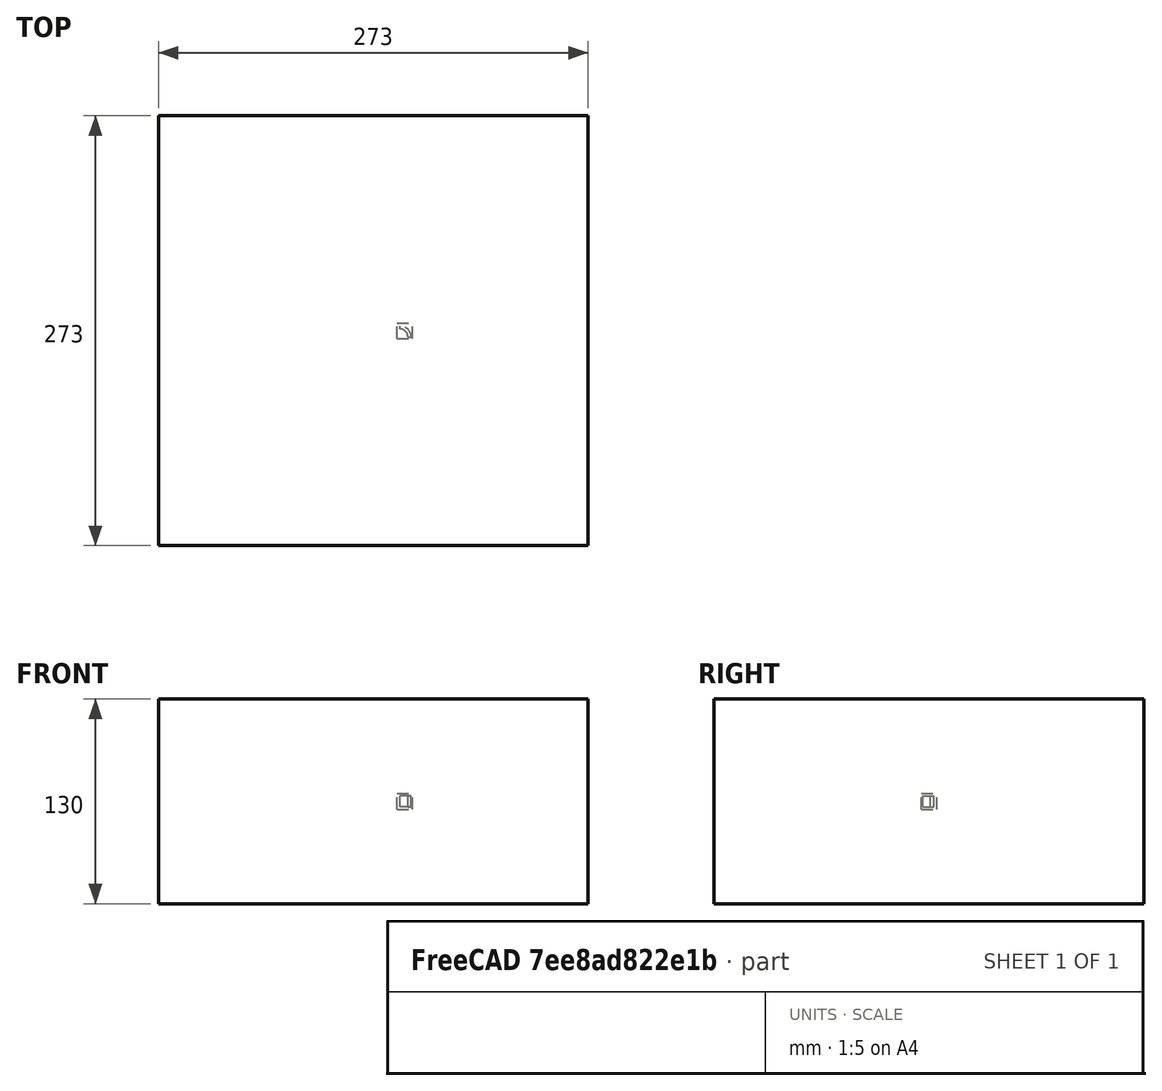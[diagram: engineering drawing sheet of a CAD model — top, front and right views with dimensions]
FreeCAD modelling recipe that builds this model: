
FCSTD DOCUMENT  (FreeCAD 0.21R33694 (Git))
Label: polarArray-of-Part
License: All rights reserved
LicenseURL: http://en.wikipedia.org/wiki/All_rights_reserved
objects: App::DocumentObjectGroupPython×1251, Part::FeaturePython×4, App::Part×4
note: 3 computed .brp shape members not serialized (recipe doc carries the construction recipe); baked Part::Feature solids carry a one-line shape summary decoded from their .brp

FEATURE [App::DocumentObjectGroupPython] HALFPI  # scripted group (container) (typed FeaturePython)
  name = HALFPI
  value = pi/2.
FEATURE [App::DocumentObjectGroupPython] PI  # scripted group (container) (typed FeaturePython)
  name = PI
  value = 1.*pi
FEATURE [App::DocumentObjectGroupPython] TWOPI  # scripted group (container) (typed FeaturePython)
  name = TWOPI
  value = 2.*pi
FEATURE [App::DocumentObjectGroupPython] Constants  # scripted group (container) (typed FeaturePython)
  Group = -> [HALFPI,PI,TWOPI]
FEATURE [App::DocumentObjectGroupPython] Variables  # scripted group (container) (typed FeaturePython)
FEATURE [App::DocumentObjectGroupPython] Quantities  # scripted group (container) (typed FeaturePython)
FEATURE [App::DocumentObjectGroupPython] Isotopes  # scripted group (container) (typed FeaturePython)
FEATURE [App::DocumentObjectGroupPython] Elements  # scripted group (container) (typed FeaturePython)
FEATURE [App::DocumentObjectGroupPython] Matrix  # scripted group (container) (typed FeaturePython)
FEATURE [App::DocumentObjectGroupPython] Surfaces  # scripted group (container) (typed FeaturePython)
FEATURE [App::DocumentObjectGroupPython] Opticals  # scripted group (container) (typed FeaturePython)
  Group = -> [Matrix,Surfaces]
FEATURE [App::DocumentObjectGroupPython] G4Isotopes  # scripted group (container) (typed FeaturePython)
FEATURE [App::DocumentObjectGroupPython] H_element  # scripted group (container) (typed FeaturePython)
  Z = 1
  atom_value = 1.008
  formula = H
  name = H_element
FEATURE [App::DocumentObjectGroupPython] He_element  # scripted group (container) (typed FeaturePython)
  Z = 2
  atom_value = 4.0026
  formula = He
  name = He_element
FEATURE [App::DocumentObjectGroupPython] Li_element  # scripted group (container) (typed FeaturePython)
  Z = 3
  atom_value = 6.94
  formula = Li
  name = Li_element
FEATURE [App::DocumentObjectGroupPython] Be_element  # scripted group (container) (typed FeaturePython)
  Z = 4
  atom_value = 9.01218
  formula = Be
  name = Be_element
FEATURE [App::DocumentObjectGroupPython] B_element  # scripted group (container) (typed FeaturePython)
  Z = 5
  atom_value = 10.81
  formula = B
  name = B_element
FEATURE [App::DocumentObjectGroupPython] C_element  # scripted group (container) (typed FeaturePython)
  Z = 6
  atom_value = 12.011
  formula = C
  name = C_element
FEATURE [App::DocumentObjectGroupPython] N_element  # scripted group (container) (typed FeaturePython)
  Z = 7
  atom_value = 14.007
  formula = N
  name = N_element
FEATURE [App::DocumentObjectGroupPython] O_element  # scripted group (container) (typed FeaturePython)
  Z = 8
  atom_value = 15.999
  formula = O
  name = O_element
FEATURE [App::DocumentObjectGroupPython] F_element  # scripted group (container) (typed FeaturePython)
  Z = 9
  atom_value = 18.9984
  formula = F
  name = F_element
FEATURE [App::DocumentObjectGroupPython] Ne_element  # scripted group (container) (typed FeaturePython)
  Z = 10
  atom_value = 20.1797
  formula = Ne
  name = Ne_element
FEATURE [App::DocumentObjectGroupPython] Na_element  # scripted group (container) (typed FeaturePython)
  Z = 11
  atom_value = 22.9898
  formula = Na
  name = Na_element
FEATURE [App::DocumentObjectGroupPython] Mg_element  # scripted group (container) (typed FeaturePython)
  Z = 12
  atom_value = 24.305
  formula = Mg
  name = Mg_element
FEATURE [App::DocumentObjectGroupPython] Al_element  # scripted group (container) (typed FeaturePython)
  Z = 13
  atom_value = 26.9815
  formula = Al
  name = Al_element
FEATURE [App::DocumentObjectGroupPython] Si_element  # scripted group (container) (typed FeaturePython)
  Z = 14
  atom_value = 28.085
  formula = Si
  name = Si_element
FEATURE [App::DocumentObjectGroupPython] P_element  # scripted group (container) (typed FeaturePython)
  Z = 15
  atom_value = 30.9738
  formula = P
  name = P_element
FEATURE [App::DocumentObjectGroupPython] S_element  # scripted group (container) (typed FeaturePython)
  Z = 16
  atom_value = 32.06
  formula = S
  name = S_element
FEATURE [App::DocumentObjectGroupPython] Cl_element  # scripted group (container) (typed FeaturePython)
  Z = 17
  atom_value = 35.45
  formula = Cl
  name = Cl_element
FEATURE [App::DocumentObjectGroupPython] Ar_element  # scripted group (container) (typed FeaturePython)
  Z = 18
  atom_value = 39.95
  formula = Ar
  name = Ar_element
FEATURE [App::DocumentObjectGroupPython] K_element  # scripted group (container) (typed FeaturePython)
  Z = 19
  atom_value = 39.0983
  formula = K
  name = K_element
FEATURE [App::DocumentObjectGroupPython] Ca_element  # scripted group (container) (typed FeaturePython)
  Z = 20
  atom_value = 40.078
  formula = Ca
  name = Ca_element
FEATURE [App::DocumentObjectGroupPython] Sc_element  # scripted group (container) (typed FeaturePython)
  Z = 21
  atom_value = 44.9559
  formula = Sc
  name = Sc_element
FEATURE [App::DocumentObjectGroupPython] Ti_element  # scripted group (container) (typed FeaturePython)
  Z = 22
  atom_value = 47.867
  formula = Ti
  name = Ti_element
FEATURE [App::DocumentObjectGroupPython] V_element  # scripted group (container) (typed FeaturePython)
  Z = 23
  atom_value = 50.9415
  formula = V
  name = V_element
FEATURE [App::DocumentObjectGroupPython] Cr_element  # scripted group (container) (typed FeaturePython)
  Z = 24
  atom_value = 51.9961
  formula = Cr
  name = Cr_element
FEATURE [App::DocumentObjectGroupPython] Mn_element  # scripted group (container) (typed FeaturePython)
  Z = 25
  atom_value = 54.938
  formula = Mn
  name = Mn_element
FEATURE [App::DocumentObjectGroupPython] Fe_element  # scripted group (container) (typed FeaturePython)
  Z = 26
  atom_value = 55.845
  formula = Fe
  name = Fe_element
FEATURE [App::DocumentObjectGroupPython] Co_element  # scripted group (container) (typed FeaturePython)
  Z = 27
  atom_value = 58.9332
  formula = Co
  name = Co_element
FEATURE [App::DocumentObjectGroupPython] Ni_element  # scripted group (container) (typed FeaturePython)
  Z = 28
  atom_value = 58.6934
  formula = Ni
  name = Ni_element
FEATURE [App::DocumentObjectGroupPython] Cu_element  # scripted group (container) (typed FeaturePython)
  Z = 29
  atom_value = 63.546
  formula = Cu
  name = Cu_element
FEATURE [App::DocumentObjectGroupPython] Zn_element  # scripted group (container) (typed FeaturePython)
  Z = 30
  atom_value = 65.38
  formula = Zn
  name = Zn_element
FEATURE [App::DocumentObjectGroupPython] Ga_element  # scripted group (container) (typed FeaturePython)
  Z = 31
  atom_value = 69.723
  formula = Ga
  name = Ga_element
FEATURE [App::DocumentObjectGroupPython] Ge_element  # scripted group (container) (typed FeaturePython)
  Z = 32
  atom_value = 72.63
  formula = Ge
  name = Ge_element
FEATURE [App::DocumentObjectGroupPython] As_element  # scripted group (container) (typed FeaturePython)
  Z = 33
  atom_value = 74.9216
  formula = As
  name = As_element
FEATURE [App::DocumentObjectGroupPython] Se_element  # scripted group (container) (typed FeaturePython)
  Z = 34
  atom_value = 78.971
  formula = Se
  name = Se_element
FEATURE [App::DocumentObjectGroupPython] Br_element  # scripted group (container) (typed FeaturePython)
  Z = 35
  atom_value = 79.904
  formula = Br
  name = Br_element
FEATURE [App::DocumentObjectGroupPython] Kr_element  # scripted group (container) (typed FeaturePython)
  Z = 36
  atom_value = 83.798
  formula = Kr
  name = Kr_element
FEATURE [App::DocumentObjectGroupPython] Rb_element  # scripted group (container) (typed FeaturePython)
  Z = 37
  atom_value = 85.4678
  formula = Rb
  name = Rb_element
FEATURE [App::DocumentObjectGroupPython] Sr_element  # scripted group (container) (typed FeaturePython)
  Z = 38
  atom_value = 87.62
  formula = Sr
  name = Sr_element
FEATURE [App::DocumentObjectGroupPython] Y_element  # scripted group (container) (typed FeaturePython)
  Z = 39
  atom_value = 88.9058
  formula = Y
  name = Y_element
FEATURE [App::DocumentObjectGroupPython] Zr_element  # scripted group (container) (typed FeaturePython)
  Z = 40
  atom_value = 91.224
  formula = Zr
  name = Zr_element
FEATURE [App::DocumentObjectGroupPython] Nb_element  # scripted group (container) (typed FeaturePython)
  Z = 41
  atom_value = 92.9064
  formula = Nb
  name = Nb_element
FEATURE [App::DocumentObjectGroupPython] Mo_element  # scripted group (container) (typed FeaturePython)
  Z = 42
  atom_value = 95.95
  formula = Mo
  name = Mo_element
FEATURE [App::DocumentObjectGroupPython] Tc_element  # scripted group (container) (typed FeaturePython)
  Z = 43
  atom_value = 97
  formula = Tc
  name = Tc_element
FEATURE [App::DocumentObjectGroupPython] Ru_element  # scripted group (container) (typed FeaturePython)
  Z = 44
  atom_value = 101.07
  formula = Ru
  name = Ru_element
FEATURE [App::DocumentObjectGroupPython] Rh_element  # scripted group (container) (typed FeaturePython)
  Z = 45
  atom_value = 102.905
  formula = Rh
  name = Rh_element
FEATURE [App::DocumentObjectGroupPython] Pd_element  # scripted group (container) (typed FeaturePython)
  Z = 46
  atom_value = 106.42
  formula = Pd
  name = Pd_element
FEATURE [App::DocumentObjectGroupPython] Ag_element  # scripted group (container) (typed FeaturePython)
  Z = 47
  atom_value = 107.868
  formula = Ag
  name = Ag_element
FEATURE [App::DocumentObjectGroupPython] Cd_element  # scripted group (container) (typed FeaturePython)
  Z = 48
  atom_value = 112.414
  formula = Cd
  name = Cd_element
FEATURE [App::DocumentObjectGroupPython] In_element  # scripted group (container) (typed FeaturePython)
  Z = 49
  atom_value = 114.818
  formula = In
  name = In_element
FEATURE [App::DocumentObjectGroupPython] Sn_element  # scripted group (container) (typed FeaturePython)
  Z = 50
  atom_value = 118.71
  formula = Sn
  name = Sn_element
FEATURE [App::DocumentObjectGroupPython] Sb_element  # scripted group (container) (typed FeaturePython)
  Z = 51
  atom_value = 121.76
  formula = Sb
  name = Sb_element
FEATURE [App::DocumentObjectGroupPython] Te_element  # scripted group (container) (typed FeaturePython)
  Z = 52
  atom_value = 127.6
  formula = Te
  name = Te_element
FEATURE [App::DocumentObjectGroupPython] I_element  # scripted group (container) (typed FeaturePython)
  Z = 53
  atom_value = 126.904
  formula = I
  name = I_element
FEATURE [App::DocumentObjectGroupPython] Xe_element  # scripted group (container) (typed FeaturePython)
  Z = 54
  atom_value = 131.293
  formula = Xe
  name = Xe_element
FEATURE [App::DocumentObjectGroupPython] Cs_element  # scripted group (container) (typed FeaturePython)
  Z = 55
  atom_value = 132.905
  formula = Cs
  name = Cs_element
FEATURE [App::DocumentObjectGroupPython] Ba_element  # scripted group (container) (typed FeaturePython)
  Z = 56
  atom_value = 137.327
  formula = Ba
  name = Ba_element
FEATURE [App::DocumentObjectGroupPython] La_element  # scripted group (container) (typed FeaturePython)
  Z = 57
  atom_value = 138.905
  formula = La
  name = La_element
FEATURE [App::DocumentObjectGroupPython] Ce_element  # scripted group (container) (typed FeaturePython)
  Z = 58
  atom_value = 140.116
  formula = Ce
  name = Ce_element
FEATURE [App::DocumentObjectGroupPython] Pr_element  # scripted group (container) (typed FeaturePython)
  Z = 59
  atom_value = 140.908
  formula = Pr
  name = Pr_element
FEATURE [App::DocumentObjectGroupPython] Nd_element  # scripted group (container) (typed FeaturePython)
  Z = 60
  atom_value = 144.242
  formula = Nd
  name = Nd_element
FEATURE [App::DocumentObjectGroupPython] Pm_element  # scripted group (container) (typed FeaturePython)
  Z = 61
  atom_value = 145
  formula = Pm
  name = Pm_element
FEATURE [App::DocumentObjectGroupPython] Sm_element  # scripted group (container) (typed FeaturePython)
  Z = 62
  atom_value = 150.36
  formula = Sm
  name = Sm_element
FEATURE [App::DocumentObjectGroupPython] Eu_element  # scripted group (container) (typed FeaturePython)
  Z = 63
  atom_value = 151.964
  formula = Eu
  name = Eu_element
FEATURE [App::DocumentObjectGroupPython] Gd_element  # scripted group (container) (typed FeaturePython)
  Z = 64
  atom_value = 157.25
  formula = Gd
  name = Gd_element
FEATURE [App::DocumentObjectGroupPython] Tb_element  # scripted group (container) (typed FeaturePython)
  Z = 65
  atom_value = 158.925
  formula = Tb
  name = Tb_element
FEATURE [App::DocumentObjectGroupPython] Dy_element  # scripted group (container) (typed FeaturePython)
  Z = 66
  atom_value = 162.5
  formula = Dy
  name = Dy_element
FEATURE [App::DocumentObjectGroupPython] Ho_element  # scripted group (container) (typed FeaturePython)
  Z = 67
  atom_value = 164.93
  formula = Ho
  name = Ho_element
FEATURE [App::DocumentObjectGroupPython] Er_element  # scripted group (container) (typed FeaturePython)
  Z = 68
  atom_value = 167.259
  formula = Er
  name = Er_element
FEATURE [App::DocumentObjectGroupPython] Tm_element  # scripted group (container) (typed FeaturePython)
  Z = 69
  atom_value = 168.934
  formula = Tm
  name = Tm_element
FEATURE [App::DocumentObjectGroupPython] Yb_element  # scripted group (container) (typed FeaturePython)
  Z = 70
  atom_value = 173.045
  formula = Yb
  name = Yb_element
FEATURE [App::DocumentObjectGroupPython] Lu_element  # scripted group (container) (typed FeaturePython)
  Z = 71
  atom_value = 174.967
  formula = Lu
  name = Lu_element
FEATURE [App::DocumentObjectGroupPython] Hf_element  # scripted group (container) (typed FeaturePython)
  Z = 72
  atom_value = 178.49
  formula = Hf
  name = Hf_element
FEATURE [App::DocumentObjectGroupPython] Ta_element  # scripted group (container) (typed FeaturePython)
  Z = 73
  atom_value = 180.948
  formula = Ta
  name = Ta_element
FEATURE [App::DocumentObjectGroupPython] W_element  # scripted group (container) (typed FeaturePython)
  Z = 74
  atom_value = 183.84
  formula = W
  name = W_element
FEATURE [App::DocumentObjectGroupPython] Re_element  # scripted group (container) (typed FeaturePython)
  Z = 75
  atom_value = 186.207
  formula = Re
  name = Re_element
FEATURE [App::DocumentObjectGroupPython] Os_element  # scripted group (container) (typed FeaturePython)
  Z = 76
  atom_value = 190.23
  formula = Os
  name = Os_element
FEATURE [App::DocumentObjectGroupPython] Ir_element  # scripted group (container) (typed FeaturePython)
  Z = 77
  atom_value = 192.217
  formula = Ir
  name = Ir_element
FEATURE [App::DocumentObjectGroupPython] Pt_element  # scripted group (container) (typed FeaturePython)
  Z = 78
  atom_value = 195.084
  formula = Pt
  name = Pt_element
FEATURE [App::DocumentObjectGroupPython] Au_element  # scripted group (container) (typed FeaturePython)
  Z = 79
  atom_value = 196.967
  formula = Au
  name = Au_element
FEATURE [App::DocumentObjectGroupPython] Hg_element  # scripted group (container) (typed FeaturePython)
  Z = 80
  atom_value = 200.592
  formula = Hg
  name = Hg_element
FEATURE [App::DocumentObjectGroupPython] Tl_element  # scripted group (container) (typed FeaturePython)
  Z = 81
  atom_value = 204.38
  formula = Tl
  name = Tl_element
FEATURE [App::DocumentObjectGroupPython] Pb_element  # scripted group (container) (typed FeaturePython)
  Z = 82
  atom_value = 207.2
  formula = Pb
  name = Pb_element
FEATURE [App::DocumentObjectGroupPython] Bi_element  # scripted group (container) (typed FeaturePython)
  Z = 83
  atom_value = 208.98
  formula = Bi
  name = Bi_element
FEATURE [App::DocumentObjectGroupPython] Po_element  # scripted group (container) (typed FeaturePython)
  Z = 84
  atom_value = 209
  formula = Po
  name = Po_element
FEATURE [App::DocumentObjectGroupPython] At_element  # scripted group (container) (typed FeaturePython)
  Z = 85
  atom_value = 210
  formula = At
  name = At_element
FEATURE [App::DocumentObjectGroupPython] Rn_element  # scripted group (container) (typed FeaturePython)
  Z = 86
  atom_value = 222
  formula = Rn
  name = Rn_element
FEATURE [App::DocumentObjectGroupPython] Fr_element  # scripted group (container) (typed FeaturePython)
  Z = 87
  atom_value = 223
  formula = Fr
  name = Fr_element
FEATURE [App::DocumentObjectGroupPython] Ra_element  # scripted group (container) (typed FeaturePython)
  Z = 88
  atom_value = 226
  formula = Ra
  name = Ra_element
FEATURE [App::DocumentObjectGroupPython] Ac_element  # scripted group (container) (typed FeaturePython)
  Z = 89
  atom_value = 227
  formula = Ac
  name = Ac_element
FEATURE [App::DocumentObjectGroupPython] Th_element  # scripted group (container) (typed FeaturePython)
  Z = 90
  atom_value = 232.038
  formula = Th
  name = Th_element
FEATURE [App::DocumentObjectGroupPython] Pa_element  # scripted group (container) (typed FeaturePython)
  Z = 91
  atom_value = 231.036
  formula = Pa
  name = Pa_element
FEATURE [App::DocumentObjectGroupPython] U_element  # scripted group (container) (typed FeaturePython)
  Z = 92
  atom_value = 238.029
  formula = U
  name = U_element
FEATURE [App::DocumentObjectGroupPython] Np_element  # scripted group (container) (typed FeaturePython)
  Z = 93
  atom_value = 237
  formula = Np
  name = Np_element
FEATURE [App::DocumentObjectGroupPython] Pu_element  # scripted group (container) (typed FeaturePython)
  Z = 94
  atom_value = 244
  formula = Pu
  name = Pu_element
FEATURE [App::DocumentObjectGroupPython] Am_element  # scripted group (container) (typed FeaturePython)
  Z = 95
  atom_value = 243
  formula = Am
  name = Am_element
FEATURE [App::DocumentObjectGroupPython] Cm_element  # scripted group (container) (typed FeaturePython)
  Z = 96
  atom_value = 247
  formula = Cm
  name = Cm_element
FEATURE [App::DocumentObjectGroupPython] Bk_element  # scripted group (container) (typed FeaturePython)
  Z = 97
  atom_value = 247
  formula = Bk
  name = Bk_element
FEATURE [App::DocumentObjectGroupPython] Cf_element  # scripted group (container) (typed FeaturePython)
  Z = 98
  atom_value = 251
  formula = Cf
  name = Cf_element
FEATURE [App::DocumentObjectGroupPython] G4Elements  # scripted group (container) (typed FeaturePython)
  Group = -> [H_element,He_element,Li_element,Be_element,B_element,C_element,N_element,O_element,F_element,Ne_element,Na_element,Mg_element,Al_element,Si_element,P_element,S_element,Cl_element,Ar_element,K_element,Ca_element,Sc_element,Ti_element,V_element,Cr_element,Mn_element,Fe_element,Co_element,Ni_element,Cu_element,Zn_element,Ga_element,Ge_element,As_element,Se_element,Br_element,Kr_element,Rb_element,+61 more]
FEATURE [App::DocumentObjectGroupPython] H_element001  label="H_element : 0.101"  # scripted group (container) (typed FeaturePython)
  n = 0.101327
FEATURE [App::DocumentObjectGroupPython] C_element001  label="C_element : 0.775"  # scripted group (container) (typed FeaturePython)
  n = 0.7755
FEATURE [App::DocumentObjectGroupPython] N_element001  label="N_element : 0.035"  # scripted group (container) (typed FeaturePython)
  n = 0.035057
FEATURE [App::DocumentObjectGroupPython] O_element001  label="O_element : 0.052"  # scripted group (container) (typed FeaturePython)
  n = 0.0523159
FEATURE [App::DocumentObjectGroupPython] F_element001  label="F_element : 0.017"  # scripted group (container) (typed FeaturePython)
  n = 0.017422
FEATURE [App::DocumentObjectGroupPython] Ca_element001  label="Ca_element : 0.018"  # scripted group (container) (typed FeaturePython)
  n = 0.018378
FEATURE [App::DocumentObjectGroupPython] G4_A_150_TISSUE  label="G4_A-150_TISSUE"  # scripted group (container) (typed FeaturePython)
  Dunit = g/cm3
  Dvalue = 1.127
  Group = -> [H_element001,C_element001,N_element001,O_element001,F_element001,Ca_element001]
  conduct = 2
  density = 1
  expand = 3
  formula = G4_A-150_TISSUE
  name = G4_A-150_TISSUE
  specific = 4
FEATURE [App::DocumentObjectGroupPython] C_element002  label="C_element : 3"  # scripted group (container) (typed FeaturePython)
  n = 3
  ref = C_element
FEATURE [App::DocumentObjectGroupPython] H_element002  label="H_element : 6"  # scripted group (container) (typed FeaturePython)
  n = 6
  ref = H_element
FEATURE [App::DocumentObjectGroupPython] O_element002  label="O_element : 1"  # scripted group (container) (typed FeaturePython)
  n = 1
  ref = O_element
FEATURE [App::DocumentObjectGroupPython] G4_ACETONE  # scripted group (container) (typed FeaturePython)
  Dunit = g/cm3
  Dvalue = 0.7899
  Group = -> [C_element002,H_element002,O_element002]
  conduct = 2
  density = 1
  expand = 3
  formula = G4_ACETONE
  name = G4_ACETONE
  specific = 4
FEATURE [App::DocumentObjectGroupPython] C_element003  label="C_element : 2"  # scripted group (container) (typed FeaturePython)
  n = 2
  ref = C_element
FEATURE [App::DocumentObjectGroupPython] H_element003  label="H_element : 2"  # scripted group (container) (typed FeaturePython)
  n = 2
  ref = H_element
FEATURE [App::DocumentObjectGroupPython] G4_ACETYLENE  # scripted group (container) (typed FeaturePython)
  Dunit = g/cm3
  Dvalue = 0.0010967
  Group = -> [C_element003,H_element003]
  conduct = 2
  density = 1
  expand = 3
  formula = G4_ACETYLENE
  name = G4_ACETYLENE
  specific = 4
FEATURE [App::DocumentObjectGroupPython] C_element004  label="C_element : 5"  # scripted group (container) (typed FeaturePython)
  n = 5
  ref = C_element
FEATURE [App::DocumentObjectGroupPython] H_element004  label="H_element : 5"  # scripted group (container) (typed FeaturePython)
  n = 5
  ref = H_element
FEATURE [App::DocumentObjectGroupPython] N_element002  label="N_element : 5"  # scripted group (container) (typed FeaturePython)
  n = 5
  ref = N_element
FEATURE [App::DocumentObjectGroupPython] G4_ADENINE  # scripted group (container) (typed FeaturePython)
  Dunit = g/cm3
  Dvalue = 1.6
  Group = -> [C_element004,H_element004,N_element002]
  conduct = 2
  density = 1
  expand = 3
  formula = G4_ADENINE
  name = G4_ADENINE
  specific = 4
FEATURE [App::DocumentObjectGroupPython] H_element005  label="H_element : 0.114"  # scripted group (container) (typed FeaturePython)
  n = 0.114
FEATURE [App::DocumentObjectGroupPython] C_element005  label="C_element : 0.598"  # scripted group (container) (typed FeaturePython)
  n = 0.598
FEATURE [App::DocumentObjectGroupPython] N_element003  label="N_element : 0.007"  # scripted group (container) (typed FeaturePython)
  n = 0.007
FEATURE [App::DocumentObjectGroupPython] O_element003  label="O_element : 0.278"  # scripted group (container) (typed FeaturePython)
  n = 0.278
FEATURE [App::DocumentObjectGroupPython] Na_element001  label="Na_element : 0.001"  # scripted group (container) (typed FeaturePython)
  n = 0.001
FEATURE [App::DocumentObjectGroupPython] S_element001  label="S_element : 0.001"  # scripted group (container) (typed FeaturePython)
  n = 0.001
FEATURE [App::DocumentObjectGroupPython] Cl_element001  label="Cl_element : 0.001"  # scripted group (container) (typed FeaturePython)
  n = 0.001
FEATURE [App::DocumentObjectGroupPython] G4_ADIPOSE_TISSUE_ICRP  # scripted group (container) (typed FeaturePython)
  Dunit = g/cm3
  Dvalue = 0.95
  Group = -> [H_element005,C_element005,N_element003,O_element003,Na_element001,S_element001,Cl_element001]
  conduct = 2
  density = 1
  expand = 3
  formula = G4_ADIPOSE_TISSUE_ICRP
  name = G4_ADIPOSE_TISSUE_ICRP
  specific = 4
FEATURE [App::DocumentObjectGroupPython] C_element006  label="C_element : 0.000"  # scripted group (container) (typed FeaturePython)
  n = 0.000124
FEATURE [App::DocumentObjectGroupPython] N_element004  label="N_element : 0.755"  # scripted group (container) (typed FeaturePython)
  n = 0.755268
FEATURE [App::DocumentObjectGroupPython] O_element004  label="O_element : 0.232"  # scripted group (container) (typed FeaturePython)
  n = 0.231781
FEATURE [App::DocumentObjectGroupPython] Ar_element001  label="Ar_element : 0.013"  # scripted group (container) (typed FeaturePython)
  n = 0.012827
FEATURE [App::DocumentObjectGroupPython] G4_AIR  # scripted group (container) (typed FeaturePython)
  Dunit = g/cm3
  Dvalue = 0.00120479
  Group = -> [C_element006,N_element004,O_element004,Ar_element001]
  conduct = 2
  density = 1
  expand = 3
  formula = G4_AIR
  name = G4_AIR
  specific = 4
FEATURE [App::DocumentObjectGroupPython] C_element007  label="C_element : 006"  # scripted group (container) (typed FeaturePython)
  n = 3
  ref = C_element
FEATURE [App::DocumentObjectGroupPython] H_element006  label="H_element : 7"  # scripted group (container) (typed FeaturePython)
  n = 7
  ref = H_element
FEATURE [App::DocumentObjectGroupPython] N_element005  label="N_element : 1"  # scripted group (container) (typed FeaturePython)
  n = 1
  ref = N_element
FEATURE [App::DocumentObjectGroupPython] O_element005  label="O_element : 2"  # scripted group (container) (typed FeaturePython)
  n = 2
  ref = O_element
FEATURE [App::DocumentObjectGroupPython] G4_ALANINE  # scripted group (container) (typed FeaturePython)
  Dunit = g/cm3
  Dvalue = 1.42
  Group = -> [C_element007,H_element006,N_element005,O_element005]
  conduct = 2
  density = 1
  expand = 3
  formula = G4_ALANINE
  name = G4_ALANINE
  specific = 4
FEATURE [App::DocumentObjectGroupPython] Al_element001  label="Al_element : 2"  # scripted group (container) (typed FeaturePython)
  n = 2
  ref = Al_element
FEATURE [App::DocumentObjectGroupPython] O_element006  label="O_element : 3"  # scripted group (container) (typed FeaturePython)
  n = 3
  ref = O_element
FEATURE [App::DocumentObjectGroupPython] G4_ALUMINUM_OXIDE  # scripted group (container) (typed FeaturePython)
  Dunit = g/cm3
  Dvalue = 3.97
  Group = -> [Al_element001,O_element006]
  conduct = 2
  density = 1
  expand = 3
  formula = G4_ALUMINUM_OXIDE
  name = G4_ALUMINUM_OXIDE
  specific = 4
FEATURE [App::DocumentObjectGroupPython] H_element007  label="H_element : 0.106"  # scripted group (container) (typed FeaturePython)
  n = 0.10593
FEATURE [App::DocumentObjectGroupPython] C_element008  label="C_element : 0.789"  # scripted group (container) (typed FeaturePython)
  n = 0.788974
FEATURE [App::DocumentObjectGroupPython] O_element007  label="O_element : 0.105"  # scripted group (container) (typed FeaturePython)
  n = 0.105096
FEATURE [App::DocumentObjectGroupPython] G4_AMBER  # scripted group (container) (typed FeaturePython)
  Dunit = g/cm3
  Dvalue = 1.1
  Group = -> [H_element007,C_element008,O_element007]
  conduct = 2
  density = 1
  expand = 3
  formula = G4_AMBER
  name = G4_AMBER
  specific = 4
FEATURE [App::DocumentObjectGroupPython] N_element006  label="N_element : 006"  # scripted group (container) (typed FeaturePython)
  n = 1
  ref = N_element
FEATURE [App::DocumentObjectGroupPython] H_element008  label="H_element : 3"  # scripted group (container) (typed FeaturePython)
  n = 3
  ref = H_element
FEATURE [App::DocumentObjectGroupPython] G4_AMMONIA  # scripted group (container) (typed FeaturePython)
  Dunit = g/cm3
  Dvalue = 0.000826019
  Group = -> [N_element006,H_element008]
  conduct = 2
  density = 1
  expand = 3
  formula = G4_AMMONIA
  name = G4_AMMONIA
  specific = 4
FEATURE [App::DocumentObjectGroupPython] C_element009  label="C_element : 6"  # scripted group (container) (typed FeaturePython)
  n = 6
  ref = C_element
FEATURE [App::DocumentObjectGroupPython] H_element009  label="H_element : 008"  # scripted group (container) (typed FeaturePython)
  n = 7
  ref = H_element
FEATURE [App::DocumentObjectGroupPython] N_element007  label="N_element : 007"  # scripted group (container) (typed FeaturePython)
  n = 1
  ref = N_element
FEATURE [App::DocumentObjectGroupPython] G4_ANILINE  # scripted group (container) (typed FeaturePython)
  Dunit = g/cm3
  Dvalue = 1.0235
  Group = -> [C_element009,H_element009,N_element007]
  conduct = 2
  density = 1
  expand = 3
  formula = G4_ANILINE
  name = G4_ANILINE
  specific = 4
FEATURE [App::DocumentObjectGroupPython] C_element010  label="C_element : 14"  # scripted group (container) (typed FeaturePython)
  n = 14
  ref = C_element
FEATURE [App::DocumentObjectGroupPython] H_element010  label="H_element : 10"  # scripted group (container) (typed FeaturePython)
  n = 10
  ref = H_element
FEATURE [App::DocumentObjectGroupPython] G4_ANTHRACENE  # scripted group (container) (typed FeaturePython)
  Dunit = g/cm3
  Dvalue = 1.283
  Group = -> [C_element010,H_element010]
  conduct = 2
  density = 1
  expand = 3
  formula = G4_ANTHRACENE
  name = G4_ANTHRACENE
  specific = 4
FEATURE [App::DocumentObjectGroupPython] H_element011  label="H_element : 0.065"  # scripted group (container) (typed FeaturePython)
  n = 0.0654709
FEATURE [App::DocumentObjectGroupPython] C_element011  label="C_element : 0.537"  # scripted group (container) (typed FeaturePython)
  n = 0.536944
FEATURE [App::DocumentObjectGroupPython] N_element008  label="N_element : 0.021"  # scripted group (container) (typed FeaturePython)
  n = 0.0215
FEATURE [App::DocumentObjectGroupPython] O_element008  label="O_element : 0.032"  # scripted group (container) (typed FeaturePython)
  n = 0.032085
FEATURE [App::DocumentObjectGroupPython] F_element002  label="F_element : 0.167"  # scripted group (container) (typed FeaturePython)
  n = 0.167411
FEATURE [App::DocumentObjectGroupPython] Ca_element002  label="Ca_element : 0.177"  # scripted group (container) (typed FeaturePython)
  n = 0.176589
FEATURE [App::DocumentObjectGroupPython] G4_B_100_BONE  label="G4_B-100_BONE"  # scripted group (container) (typed FeaturePython)
  Dunit = g/cm3
  Dvalue = 1.45
  Group = -> [H_element011,C_element011,N_element008,O_element008,F_element002,Ca_element002]
  conduct = 2
  density = 1
  expand = 3
  formula = G4_B-100_BONE
  name = G4_B-100_BONE
  specific = 4
FEATURE [App::DocumentObjectGroupPython] H_element012  label="H_element : 0.057"  # scripted group (container) (typed FeaturePython)
  n = 0.057441
FEATURE [App::DocumentObjectGroupPython] C_element012  label="C_element : 0.790"  # scripted group (container) (typed FeaturePython)
  n = 0.774591
FEATURE [App::DocumentObjectGroupPython] O_element009  label="O_element : 0.168"  # scripted group (container) (typed FeaturePython)
  n = 0.167968
FEATURE [App::DocumentObjectGroupPython] G4_BAKELITE  # scripted group (container) (typed FeaturePython)
  Dunit = g/cm3
  Dvalue = 1.25
  Group = -> [H_element012,C_element012,O_element009]
  conduct = 2
  density = 1
  expand = 3
  formula = G4_BAKELITE
  name = G4_BAKELITE
  specific = 4
FEATURE [App::DocumentObjectGroupPython] Ba_element001  label="Ba_element : 1"  # scripted group (container) (typed FeaturePython)
  n = 1
  ref = Ba_element
FEATURE [App::DocumentObjectGroupPython] F_element003  label="F_element : 2"  # scripted group (container) (typed FeaturePython)
  n = 2
  ref = F_element
FEATURE [App::DocumentObjectGroupPython] G4_BARIUM_FLUORIDE  # scripted group (container) (typed FeaturePython)
  Dunit = g/cm3
  Dvalue = 4.89
  Group = -> [Ba_element001,F_element003]
  conduct = 2
  density = 1
  expand = 3
  formula = G4_BARIUM_FLUORIDE
  name = G4_BARIUM_FLUORIDE
  specific = 4
FEATURE [App::DocumentObjectGroupPython] Ba_element002  label="Ba_element : 002"  # scripted group (container) (typed FeaturePython)
  n = 1
  ref = Ba_element
FEATURE [App::DocumentObjectGroupPython] S_element002  label="S_element : 1"  # scripted group (container) (typed FeaturePython)
  n = 1
  ref = S_element
FEATURE [App::DocumentObjectGroupPython] O_element010  label="O_element : 4"  # scripted group (container) (typed FeaturePython)
  n = 4
  ref = O_element
FEATURE [App::DocumentObjectGroupPython] G4_BARIUM_SULFATE  # scripted group (container) (typed FeaturePython)
  Dunit = g/cm3
  Dvalue = 4.5
  Group = -> [Ba_element002,S_element002,O_element010]
  conduct = 2
  density = 1
  expand = 3
  formula = G4_BARIUM_SULFATE
  name = G4_BARIUM_SULFATE
  specific = 4
FEATURE [App::DocumentObjectGroupPython] C_element013  label="C_element : 007"  # scripted group (container) (typed FeaturePython)
  n = 6
  ref = C_element
FEATURE [App::DocumentObjectGroupPython] H_element013  label="H_element : 009"  # scripted group (container) (typed FeaturePython)
  n = 6
  ref = H_element
FEATURE [App::DocumentObjectGroupPython] G4_BENZENE  # scripted group (container) (typed FeaturePython)
  Dunit = g/cm3
  Dvalue = 0.87865
  Group = -> [C_element013,H_element013]
  conduct = 2
  density = 1
  expand = 3
  formula = G4_BENZENE
  name = G4_BENZENE
  specific = 4
FEATURE [App::DocumentObjectGroupPython] Be_element001  label="Be_element : 1"  # scripted group (container) (typed FeaturePython)
  n = 1
  ref = Be_element
FEATURE [App::DocumentObjectGroupPython] O_element011  label="O_element : 005"  # scripted group (container) (typed FeaturePython)
  n = 1
  ref = O_element
FEATURE [App::DocumentObjectGroupPython] G4_BERYLLIUM_OXIDE  # scripted group (container) (typed FeaturePython)
  Dunit = g/cm3
  Dvalue = 3.01
  Group = -> [Be_element001,O_element011]
  conduct = 2
  density = 1
  expand = 3
  formula = G4_BERYLLIUM_OXIDE
  name = G4_BERYLLIUM_OXIDE
  specific = 4
FEATURE [App::DocumentObjectGroupPython] Bi_element001  label="Bi_element : 4"  # scripted group (container) (typed FeaturePython)
  n = 4
  ref = Bi_element
FEATURE [App::DocumentObjectGroupPython] Ge_element001  label="Ge_element : 3"  # scripted group (container) (typed FeaturePython)
  n = 3
  ref = Ge_element
FEATURE [App::DocumentObjectGroupPython] O_element012  label="O_element : 12"  # scripted group (container) (typed FeaturePython)
  n = 12
  ref = O_element
FEATURE [App::DocumentObjectGroupPython] G4_BGO  # scripted group (container) (typed FeaturePython)
  Dunit = g/cm3
  Dvalue = 7.13
  Group = -> [Bi_element001,Ge_element001,O_element012]
  conduct = 2
  density = 1
  expand = 3
  formula = G4_BGO
  name = G4_BGO
  specific = 4
FEATURE [App::DocumentObjectGroupPython] H_element014  label="H_element : 0.102"  # scripted group (container) (typed FeaturePython)
  n = 0.102
FEATURE [App::DocumentObjectGroupPython] C_element014  label="C_element : 0.110"  # scripted group (container) (typed FeaturePython)
  n = 0.11
FEATURE [App::DocumentObjectGroupPython] N_element009  label="N_element : 0.033"  # scripted group (container) (typed FeaturePython)
  n = 0.033
FEATURE [App::DocumentObjectGroupPython] O_element013  label="O_element : 0.745"  # scripted group (container) (typed FeaturePython)
  n = 0.745
FEATURE [App::DocumentObjectGroupPython] Na_element002  label="Na_element : 0.002"  # scripted group (container) (typed FeaturePython)
  n = 0.001
FEATURE [App::DocumentObjectGroupPython] P_element001  label="P_element : 0.001"  # scripted group (container) (typed FeaturePython)
  n = 0.001
FEATURE [App::DocumentObjectGroupPython] S_element003  label="S_element : 0.002"  # scripted group (container) (typed FeaturePython)
  n = 0.002
FEATURE [App::DocumentObjectGroupPython] Cl_element002  label="Cl_element : 0.003"  # scripted group (container) (typed FeaturePython)
  n = 0.003
FEATURE [App::DocumentObjectGroupPython] K_element001  label="K_element : 0.002"  # scripted group (container) (typed FeaturePython)
  n = 0.002
FEATURE [App::DocumentObjectGroupPython] Fe_element001  label="Fe_element : 0.001"  # scripted group (container) (typed FeaturePython)
  n = 0.001
FEATURE [App::DocumentObjectGroupPython] G4_BLOOD_ICRP  # scripted group (container) (typed FeaturePython)
  Dunit = g/cm3
  Dvalue = 1.06
  Group = -> [H_element014,C_element014,N_element009,O_element013,Na_element002,P_element001,S_element003,Cl_element002,K_element001,Fe_element001]
  conduct = 2
  density = 1
  expand = 3
  formula = G4_BLOOD_ICRP
  name = G4_BLOOD_ICRP
  specific = 4
FEATURE [App::DocumentObjectGroupPython] H_element015  label="H_element : 0.064"  # scripted group (container) (typed FeaturePython)
  n = 0.064
FEATURE [App::DocumentObjectGroupPython] C_element015  label="C_element : 0.278"  # scripted group (container) (typed FeaturePython)
  n = 0.278
FEATURE [App::DocumentObjectGroupPython] N_element010  label="N_element : 0.027"  # scripted group (container) (typed FeaturePython)
  n = 0.027
FEATURE [App::DocumentObjectGroupPython] O_element014  label="O_element : 0.410"  # scripted group (container) (typed FeaturePython)
  n = 0.41
FEATURE [App::DocumentObjectGroupPython] Mg_element001  label="Mg_element : 0.002"  # scripted group (container) (typed FeaturePython)
  n = 0.002
FEATURE [App::DocumentObjectGroupPython] P_element002  label="P_element : 0.070"  # scripted group (container) (typed FeaturePython)
  n = 0.07
FEATURE [App::DocumentObjectGroupPython] S_element004  label="S_element : 0.003"  # scripted group (container) (typed FeaturePython)
  n = 0.002
FEATURE [App::DocumentObjectGroupPython] Ca_element003  label="Ca_element : 0.147"  # scripted group (container) (typed FeaturePython)
  n = 0.147
FEATURE [App::DocumentObjectGroupPython] G4_BONE_COMPACT_ICRU  # scripted group (container) (typed FeaturePython)
  Dunit = g/cm3
  Dvalue = 1.85
  Group = -> [H_element015,C_element015,N_element010,O_element014,Mg_element001,P_element002,S_element004,Ca_element003]
  conduct = 2
  density = 1
  expand = 3
  formula = G4_BONE_COMPACT_ICRU
  name = G4_BONE_COMPACT_ICRU
  specific = 4
FEATURE [App::DocumentObjectGroupPython] H_element016  label="H_element : 0.034"  # scripted group (container) (typed FeaturePython)
  n = 0.034
FEATURE [App::DocumentObjectGroupPython] C_element016  label="C_element : 0.155"  # scripted group (container) (typed FeaturePython)
  n = 0.155
FEATURE [App::DocumentObjectGroupPython] N_element011  label="N_element : 0.042"  # scripted group (container) (typed FeaturePython)
  n = 0.042
FEATURE [App::DocumentObjectGroupPython] O_element015  label="O_element : 0.435"  # scripted group (container) (typed FeaturePython)
  n = 0.435
FEATURE [App::DocumentObjectGroupPython] Na_element003  label="Na_element : 0.003"  # scripted group (container) (typed FeaturePython)
  n = 0.001
FEATURE [App::DocumentObjectGroupPython] Mg_element002  label="Mg_element : 0.003"  # scripted group (container) (typed FeaturePython)
  n = 0.002
FEATURE [App::DocumentObjectGroupPython] P_element003  label="P_element : 0.103"  # scripted group (container) (typed FeaturePython)
  n = 0.103
FEATURE [App::DocumentObjectGroupPython] S_element005  label="S_element : 0.004"  # scripted group (container) (typed FeaturePython)
  n = 0.003
FEATURE [App::DocumentObjectGroupPython] Ca_element004  label="Ca_element : 0.225"  # scripted group (container) (typed FeaturePython)
  n = 0.225
FEATURE [App::DocumentObjectGroupPython] G4_BONE_CORTICAL_ICRP  # scripted group (container) (typed FeaturePython)
  Dunit = g/cm3
  Dvalue = 1.92
  Group = -> [H_element016,C_element016,N_element011,O_element015,Na_element003,Mg_element002,P_element003,S_element005,Ca_element004]
  conduct = 2
  density = 1
  expand = 3
  formula = G4_BONE_CORTICAL_ICRP
  name = G4_BONE_CORTICAL_ICRP
  specific = 4
FEATURE [App::DocumentObjectGroupPython] B_element001  label="B_element : 4"  # scripted group (container) (typed FeaturePython)
  n = 4
  ref = B_element
FEATURE [App::DocumentObjectGroupPython] C_element017  label="C_element : 1"  # scripted group (container) (typed FeaturePython)
  n = 1
  ref = C_element
FEATURE [App::DocumentObjectGroupPython] G4_BORON_CARBIDE  # scripted group (container) (typed FeaturePython)
  Dunit = g/cm3
  Dvalue = 2.52
  Group = -> [B_element001,C_element017]
  conduct = 2
  density = 1
  expand = 3
  formula = G4_BORON_CARBIDE
  name = G4_BORON_CARBIDE
  specific = 4
FEATURE [App::DocumentObjectGroupPython] B_element002  label="B_element : 2"  # scripted group (container) (typed FeaturePython)
  n = 2
  ref = B_element
FEATURE [App::DocumentObjectGroupPython] O_element016  label="O_element : 006"  # scripted group (container) (typed FeaturePython)
  n = 3
  ref = O_element
FEATURE [App::DocumentObjectGroupPython] G4_BORON_OXIDE  # scripted group (container) (typed FeaturePython)
  Dunit = g/cm3
  Dvalue = 1.812
  Group = -> [B_element002,O_element016]
  conduct = 2
  density = 1
  expand = 3
  formula = G4_BORON_OXIDE
  name = G4_BORON_OXIDE
  specific = 4
FEATURE [App::DocumentObjectGroupPython] H_element017  label="H_element : 0.107"  # scripted group (container) (typed FeaturePython)
  n = 0.107
FEATURE [App::DocumentObjectGroupPython] C_element018  label="C_element : 0.145"  # scripted group (container) (typed FeaturePython)
  n = 0.145
FEATURE [App::DocumentObjectGroupPython] N_element012  label="N_element : 0.022"  # scripted group (container) (typed FeaturePython)
  n = 0.022
FEATURE [App::DocumentObjectGroupPython] O_element017  label="O_element : 0.712"  # scripted group (container) (typed FeaturePython)
  n = 0.712
FEATURE [App::DocumentObjectGroupPython] Na_element004  label="Na_element : 0.004"  # scripted group (container) (typed FeaturePython)
  n = 0.002
FEATURE [App::DocumentObjectGroupPython] P_element004  label="P_element : 0.004"  # scripted group (container) (typed FeaturePython)
  n = 0.004
FEATURE [App::DocumentObjectGroupPython] S_element006  label="S_element : 0.005"  # scripted group (container) (typed FeaturePython)
  n = 0.002
FEATURE [App::DocumentObjectGroupPython] Cl_element003  label="Cl_element : 0.004"  # scripted group (container) (typed FeaturePython)
  n = 0.003
FEATURE [App::DocumentObjectGroupPython] K_element002  label="K_element : 0.003"  # scripted group (container) (typed FeaturePython)
  n = 0.003
FEATURE [App::DocumentObjectGroupPython] G4_BRAIN_ICRP  # scripted group (container) (typed FeaturePython)
  Dunit = g/cm3
  Dvalue = 1.04
  Group = -> [H_element017,C_element018,N_element012,O_element017,Na_element004,P_element004,S_element006,Cl_element003,K_element002]
  conduct = 2
  density = 1
  expand = 3
  formula = G4_BRAIN_ICRP
  name = G4_BRAIN_ICRP
  specific = 4
FEATURE [App::DocumentObjectGroupPython] C_element019  label="C_element : 4"  # scripted group (container) (typed FeaturePython)
  n = 4
  ref = C_element
FEATURE [App::DocumentObjectGroupPython] H_element018  label="H_element : 010"  # scripted group (container) (typed FeaturePython)
  n = 10
  ref = H_element
FEATURE [App::DocumentObjectGroupPython] G4_BUTANE  # scripted group (container) (typed FeaturePython)
  Dunit = g/cm3
  Dvalue = 0.00249343
  Group = -> [C_element019,H_element018]
  conduct = 2
  density = 1
  expand = 3
  formula = G4_BUTANE
  name = G4_BUTANE
  specific = 4
FEATURE [App::DocumentObjectGroupPython] C_element020  label="C_element : 008"  # scripted group (container) (typed FeaturePython)
  n = 4
  ref = C_element
FEATURE [App::DocumentObjectGroupPython] H_element019  label="H_element : 011"  # scripted group (container) (typed FeaturePython)
  n = 10
  ref = H_element
FEATURE [App::DocumentObjectGroupPython] O_element018  label="O_element : 007"  # scripted group (container) (typed FeaturePython)
  n = 1
  ref = O_element
FEATURE [App::DocumentObjectGroupPython] G4_N_BUTYL_ALCOHOL  label="G4_N-BUTYL_ALCOHOL"  # scripted group (container) (typed FeaturePython)
  Dunit = g/cm3
  Dvalue = 0.8098
  Group = -> [C_element020,H_element019,O_element018]
  conduct = 2
  density = 1
  expand = 3
  formula = G4_N-BUTYL_ALCOHOL
  name = G4_N-BUTYL_ALCOHOL
  specific = 4
FEATURE [App::DocumentObjectGroupPython] H_element020  label="H_element : 0.025"  # scripted group (container) (typed FeaturePython)
  n = 0.02468
FEATURE [App::DocumentObjectGroupPython] C_element021  label="C_element : 0.502"  # scripted group (container) (typed FeaturePython)
  n = 0.501611
FEATURE [App::DocumentObjectGroupPython] O_element019  label="O_element : 0.005"  # scripted group (container) (typed FeaturePython)
  n = 0.004527
FEATURE [App::DocumentObjectGroupPython] F_element004  label="F_element : 0.465"  # scripted group (container) (typed FeaturePython)
  n = 0.465209
FEATURE [App::DocumentObjectGroupPython] Si_element001  label="Si_element : 0.004"  # scripted group (container) (typed FeaturePython)
  n = 0.003973
FEATURE [App::DocumentObjectGroupPython] G4_C_552  label="G4_C-552"  # scripted group (container) (typed FeaturePython)
  Dunit = g/cm3
  Dvalue = 1.76
  Group = -> [H_element020,C_element021,O_element019,F_element004,Si_element001]
  conduct = 2
  density = 1
  expand = 3
  formula = G4_C-552
  name = G4_C-552
  specific = 4
FEATURE [App::DocumentObjectGroupPython] Cd_element001  label="Cd_element : 1"  # scripted group (container) (typed FeaturePython)
  n = 1
  ref = Cd_element
FEATURE [App::DocumentObjectGroupPython] Te_element001  label="Te_element : 1"  # scripted group (container) (typed FeaturePython)
  n = 1
  ref = Te_element
FEATURE [App::DocumentObjectGroupPython] G4_CADMIUM_TELLURIDE  # scripted group (container) (typed FeaturePython)
  Dunit = g/cm3
  Dvalue = 6.2
  Group = -> [Cd_element001,Te_element001]
  conduct = 2
  density = 1
  expand = 3
  formula = G4_CADMIUM_TELLURIDE
  name = G4_CADMIUM_TELLURIDE
  specific = 4
FEATURE [App::DocumentObjectGroupPython] Cd_element002  label="Cd_element : 002"  # scripted group (container) (typed FeaturePython)
  n = 1
  ref = Cd_element
FEATURE [App::DocumentObjectGroupPython] W_element001  label="W_element : 1"  # scripted group (container) (typed FeaturePython)
  n = 1
  ref = W_element
FEATURE [App::DocumentObjectGroupPython] O_element020  label="O_element : 008"  # scripted group (container) (typed FeaturePython)
  n = 4
  ref = O_element
FEATURE [App::DocumentObjectGroupPython] G4_CADMIUM_TUNGSTATE  # scripted group (container) (typed FeaturePython)
  Dunit = g/cm3
  Dvalue = 7.9
  Group = -> [Cd_element002,W_element001,O_element020]
  conduct = 2
  density = 1
  expand = 3
  formula = G4_CADMIUM_TUNGSTATE
  name = G4_CADMIUM_TUNGSTATE
  specific = 4
FEATURE [App::DocumentObjectGroupPython] Ca_element005  label="Ca_element : 1"  # scripted group (container) (typed FeaturePython)
  n = 1
  ref = Ca_element
FEATURE [App::DocumentObjectGroupPython] C_element022  label="C_element : 009"  # scripted group (container) (typed FeaturePython)
  n = 1
  ref = C_element
FEATURE [App::DocumentObjectGroupPython] O_element021  label="O_element : 009"  # scripted group (container) (typed FeaturePython)
  n = 3
  ref = O_element
FEATURE [App::DocumentObjectGroupPython] G4_CALCIUM_CARBONATE  # scripted group (container) (typed FeaturePython)
  Dunit = g/cm3
  Dvalue = 2.8
  Group = -> [Ca_element005,C_element022,O_element021]
  conduct = 2
  density = 1
  expand = 3
  formula = G4_CALCIUM_CARBONATE
  name = G4_CALCIUM_CARBONATE
  specific = 4
FEATURE [App::DocumentObjectGroupPython] Ca_element006  label="Ca_element : 002"  # scripted group (container) (typed FeaturePython)
  n = 1
  ref = Ca_element
FEATURE [App::DocumentObjectGroupPython] F_element005  label="F_element : 003"  # scripted group (container) (typed FeaturePython)
  n = 2
  ref = F_element
FEATURE [App::DocumentObjectGroupPython] G4_CALCIUM_FLUORIDE  # scripted group (container) (typed FeaturePython)
  Dunit = g/cm3
  Dvalue = 3.18
  Group = -> [Ca_element006,F_element005]
  conduct = 2
  density = 1
  expand = 3
  formula = G4_CALCIUM_FLUORIDE
  name = G4_CALCIUM_FLUORIDE
  specific = 4
FEATURE [App::DocumentObjectGroupPython] Ca_element007  label="Ca_element : 003"  # scripted group (container) (typed FeaturePython)
  n = 1
  ref = Ca_element
FEATURE [App::DocumentObjectGroupPython] O_element022  label="O_element : 010"  # scripted group (container) (typed FeaturePython)
  n = 1
  ref = O_element
FEATURE [App::DocumentObjectGroupPython] G4_CALCIUM_OXIDE  # scripted group (container) (typed FeaturePython)
  Dunit = g/cm3
  Dvalue = 3.3
  Group = -> [Ca_element007,O_element022]
  conduct = 2
  density = 1
  expand = 3
  formula = G4_CALCIUM_OXIDE
  name = G4_CALCIUM_OXIDE
  specific = 4
FEATURE [App::DocumentObjectGroupPython] Ca_element008  label="Ca_element : 004"  # scripted group (container) (typed FeaturePython)
  n = 1
  ref = Ca_element
FEATURE [App::DocumentObjectGroupPython] S_element007  label="S_element : 002"  # scripted group (container) (typed FeaturePython)
  n = 1
  ref = S_element
FEATURE [App::DocumentObjectGroupPython] O_element023  label="O_element : 011"  # scripted group (container) (typed FeaturePython)
  n = 4
  ref = O_element
FEATURE [App::DocumentObjectGroupPython] G4_CALCIUM_SULFATE  # scripted group (container) (typed FeaturePython)
  Dunit = g/cm3
  Dvalue = 2.96
  Group = -> [Ca_element008,S_element007,O_element023]
  conduct = 2
  density = 1
  expand = 3
  formula = G4_CALCIUM_SULFATE
  name = G4_CALCIUM_SULFATE
  specific = 4
FEATURE [App::DocumentObjectGroupPython] Ca_element009  label="Ca_element : 005"  # scripted group (container) (typed FeaturePython)
  n = 1
  ref = Ca_element
FEATURE [App::DocumentObjectGroupPython] W_element002  label="W_element : 002"  # scripted group (container) (typed FeaturePython)
  n = 1
  ref = W_element
FEATURE [App::DocumentObjectGroupPython] O_element024  label="O_element : 012"  # scripted group (container) (typed FeaturePython)
  n = 4
  ref = O_element
FEATURE [App::DocumentObjectGroupPython] G4_CALCIUM_TUNGSTATE  # scripted group (container) (typed FeaturePython)
  Dunit = g/cm3
  Dvalue = 6.062
  Group = -> [Ca_element009,W_element002,O_element024]
  conduct = 2
  density = 1
  expand = 3
  formula = G4_CALCIUM_TUNGSTATE
  name = G4_CALCIUM_TUNGSTATE
  specific = 4
FEATURE [App::DocumentObjectGroupPython] C_element023  label="C_element : 010"  # scripted group (container) (typed FeaturePython)
  n = 1
  ref = C_element
FEATURE [App::DocumentObjectGroupPython] O_element025  label="O_element : 013"  # scripted group (container) (typed FeaturePython)
  n = 2
  ref = O_element
FEATURE [App::DocumentObjectGroupPython] G4_CARBON_DIOXIDE  # scripted group (container) (typed FeaturePython)
  Dunit = g/cm3
  Dvalue = 0.00184212
  Group = -> [C_element023,O_element025]
  conduct = 2
  density = 1
  expand = 3
  formula = G4_CARBON_DIOXIDE
  name = G4_CARBON_DIOXIDE
  specific = 4
FEATURE [App::DocumentObjectGroupPython] C_element024  label="C_element : 011"  # scripted group (container) (typed FeaturePython)
  n = 1
  ref = C_element
FEATURE [App::DocumentObjectGroupPython] Cl_element004  label="Cl_element : 4"  # scripted group (container) (typed FeaturePython)
  n = 4
  ref = Cl_element
FEATURE [App::DocumentObjectGroupPython] G4_CARBON_TETRACHLORIDE  # scripted group (container) (typed FeaturePython)
  Dunit = g/cm3
  Dvalue = 1.594
  Group = -> [C_element024,Cl_element004]
  conduct = 2
  density = 1
  expand = 3
  formula = G4_CARBON_TETRACHLORIDE
  name = G4_CARBON_TETRACHLORIDE
  specific = 4
FEATURE [App::DocumentObjectGroupPython] C_element025  label="C_element : 012"  # scripted group (container) (typed FeaturePython)
  n = 6
  ref = C_element
FEATURE [App::DocumentObjectGroupPython] H_element021  label="H_element : 012"  # scripted group (container) (typed FeaturePython)
  n = 10
  ref = H_element
FEATURE [App::DocumentObjectGroupPython] O_element026  label="O_element : 5"  # scripted group (container) (typed FeaturePython)
  n = 5
  ref = O_element
FEATURE [App::DocumentObjectGroupPython] G4_CELLULOSE_CELLOPHANE  # scripted group (container) (typed FeaturePython)
  Dunit = g/cm3
  Dvalue = 1.42
  Group = -> [C_element025,H_element021,O_element026]
  conduct = 2
  density = 1
  expand = 3
  formula = G4_CELLULOSE_CELLOPHANE
  name = G4_CELLULOSE_CELLOPHANE
  specific = 4
FEATURE [App::DocumentObjectGroupPython] H_element022  label="H_element : 0.067"  # scripted group (container) (typed FeaturePython)
  n = 0.067125
FEATURE [App::DocumentObjectGroupPython] C_element026  label="C_element : 0.545"  # scripted group (container) (typed FeaturePython)
  n = 0.545403
FEATURE [App::DocumentObjectGroupPython] O_element027  label="O_element : 0.387"  # scripted group (container) (typed FeaturePython)
  n = 0.387472
FEATURE [App::DocumentObjectGroupPython] G4_CELLULOSE_BUTYRATE  # scripted group (container) (typed FeaturePython)
  Dunit = g/cm3
  Dvalue = 1.2
  Group = -> [H_element022,C_element026,O_element027]
  conduct = 2
  density = 1
  expand = 3
  formula = G4_CELLULOSE_BUTYRATE
  name = G4_CELLULOSE_BUTYRATE
  specific = 4
FEATURE [App::DocumentObjectGroupPython] H_element023  label="H_element : 0.029"  # scripted group (container) (typed FeaturePython)
  n = 0.029216
FEATURE [App::DocumentObjectGroupPython] C_element027  label="C_element : 0.271"  # scripted group (container) (typed FeaturePython)
  n = 0.271296
FEATURE [App::DocumentObjectGroupPython] N_element013  label="N_element : 0.121"  # scripted group (container) (typed FeaturePython)
  n = 0.121276
FEATURE [App::DocumentObjectGroupPython] O_element028  label="O_element : 0.578"  # scripted group (container) (typed FeaturePython)
  n = 0.578212
FEATURE [App::DocumentObjectGroupPython] G4_CELLULOSE_NITRATE  # scripted group (container) (typed FeaturePython)
  Dunit = g/cm3
  Dvalue = 1.49
  Group = -> [H_element023,C_element027,N_element013,O_element028]
  conduct = 2
  density = 1
  expand = 3
  formula = G4_CELLULOSE_NITRATE
  name = G4_CELLULOSE_NITRATE
  specific = 4
FEATURE [App::DocumentObjectGroupPython] H_element024  label="H_element : 0.108"  # scripted group (container) (typed FeaturePython)
  n = 0.107596
FEATURE [App::DocumentObjectGroupPython] N_element014  label="N_element : 0.001"  # scripted group (container) (typed FeaturePython)
  n = 0.0008
FEATURE [App::DocumentObjectGroupPython] O_element029  label="O_element : 0.875"  # scripted group (container) (typed FeaturePython)
  n = 0.874976
FEATURE [App::DocumentObjectGroupPython] S_element008  label="S_element : 0.015"  # scripted group (container) (typed FeaturePython)
  n = 0.014627
FEATURE [App::DocumentObjectGroupPython] Ce_element001  label="Ce_element : 0.002"  # scripted group (container) (typed FeaturePython)
  n = 0.002001
FEATURE [App::DocumentObjectGroupPython] G4_CERIC_SULFATE  # scripted group (container) (typed FeaturePython)
  Dunit = g/cm3
  Dvalue = 1.03
  Group = -> [H_element024,N_element014,O_element029,S_element008,Ce_element001]
  conduct = 2
  density = 1
  expand = 3
  formula = G4_CERIC_SULFATE
  name = G4_CERIC_SULFATE
  specific = 4
FEATURE [App::DocumentObjectGroupPython] Cs_element001  label="Cs_element : 1"  # scripted group (container) (typed FeaturePython)
  n = 1
  ref = Cs_element
FEATURE [App::DocumentObjectGroupPython] F_element006  label="F_element : 1"  # scripted group (container) (typed FeaturePython)
  n = 1
  ref = F_element
FEATURE [App::DocumentObjectGroupPython] G4_CESIUM_FLUORIDE  # scripted group (container) (typed FeaturePython)
  Dunit = g/cm3
  Dvalue = 4.115
  Group = -> [Cs_element001,F_element006]
  conduct = 2
  density = 1
  expand = 3
  formula = G4_CESIUM_FLUORIDE
  name = G4_CESIUM_FLUORIDE
  specific = 4
FEATURE [App::DocumentObjectGroupPython] Cs_element002  label="Cs_element : 002"  # scripted group (container) (typed FeaturePython)
  n = 1
  ref = Cs_element
FEATURE [App::DocumentObjectGroupPython] I_element001  label="I_element : 1"  # scripted group (container) (typed FeaturePython)
  n = 1
  ref = I_element
FEATURE [App::DocumentObjectGroupPython] G4_CESIUM_IODIDE  # scripted group (container) (typed FeaturePython)
  Dunit = g/cm3
  Dvalue = 4.51
  Group = -> [Cs_element002,I_element001]
  conduct = 2
  density = 1
  expand = 3
  formula = G4_CESIUM_IODIDE
  name = G4_CESIUM_IODIDE
  specific = 4
FEATURE [App::DocumentObjectGroupPython] C_element028  label="C_element : 013"  # scripted group (container) (typed FeaturePython)
  n = 6
  ref = C_element
FEATURE [App::DocumentObjectGroupPython] H_element025  label="H_element : 013"  # scripted group (container) (typed FeaturePython)
  n = 5
  ref = H_element
FEATURE [App::DocumentObjectGroupPython] Cl_element005  label="Cl_element : 1"  # scripted group (container) (typed FeaturePython)
  n = 1
  ref = Cl_element
FEATURE [App::DocumentObjectGroupPython] G4_CHLOROBENZENE  # scripted group (container) (typed FeaturePython)
  Dunit = g/cm3
  Dvalue = 1.1058
  Group = -> [C_element028,H_element025,Cl_element005]
  conduct = 2
  density = 1
  expand = 3
  formula = G4_CHLOROBENZENE
  name = G4_CHLOROBENZENE
  specific = 4
FEATURE [App::DocumentObjectGroupPython] C_element029  label="C_element : 014"  # scripted group (container) (typed FeaturePython)
  n = 1
  ref = C_element
FEATURE [App::DocumentObjectGroupPython] H_element026  label="H_element : 1"  # scripted group (container) (typed FeaturePython)
  n = 1
  ref = H_element
FEATURE [App::DocumentObjectGroupPython] Cl_element006  label="Cl_element : 3"  # scripted group (container) (typed FeaturePython)
  n = 3
  ref = Cl_element
FEATURE [App::DocumentObjectGroupPython] G4_CHLOROFORM  # scripted group (container) (typed FeaturePython)
  Dunit = g/cm3
  Dvalue = 1.4832
  Group = -> [C_element029,H_element026,Cl_element006]
  conduct = 2
  density = 1
  expand = 3
  formula = G4_CHLOROFORM
  name = G4_CHLOROFORM
  specific = 4
FEATURE [App::DocumentObjectGroupPython] H_element027  label="H_element : 0.010"  # scripted group (container) (typed FeaturePython)
  n = 0.01
FEATURE [App::DocumentObjectGroupPython] C_element030  label="C_element : 0.001"  # scripted group (container) (typed FeaturePython)
  n = 0.001
FEATURE [App::DocumentObjectGroupPython] O_element030  label="O_element : 0.529"  # scripted group (container) (typed FeaturePython)
  n = 0.529107
FEATURE [App::DocumentObjectGroupPython] Na_element005  label="Na_element : 0.016"  # scripted group (container) (typed FeaturePython)
  n = 0.016
FEATURE [App::DocumentObjectGroupPython] Mg_element003  label="Mg_element : 0.004"  # scripted group (container) (typed FeaturePython)
  n = 0.002
FEATURE [App::DocumentObjectGroupPython] Al_element002  label="Al_element : 0.034"  # scripted group (container) (typed FeaturePython)
  n = 0.033872
FEATURE [App::DocumentObjectGroupPython] Si_element002  label="Si_element : 0.337"  # scripted group (container) (typed FeaturePython)
  n = 0.337021
FEATURE [App::DocumentObjectGroupPython] K_element003  label="K_element : 0.013"  # scripted group (container) (typed FeaturePython)
  n = 0.013
FEATURE [App::DocumentObjectGroupPython] Ca_element010  label="Ca_element : 0.044"  # scripted group (container) (typed FeaturePython)
  n = 0.044
FEATURE [App::DocumentObjectGroupPython] Fe_element002  label="Fe_element : 0.014"  # scripted group (container) (typed FeaturePython)
  n = 0.014
FEATURE [App::DocumentObjectGroupPython] G4_CONCRETE  # scripted group (container) (typed FeaturePython)
  Dunit = g/cm3
  Dvalue = 2.3
  Group = -> [H_element027,C_element030,O_element030,Na_element005,Mg_element003,Al_element002,Si_element002,K_element003,Ca_element010,Fe_element002]
  conduct = 2
  density = 1
  expand = 3
  formula = G4_CONCRETE
  name = G4_CONCRETE
  specific = 4
FEATURE [App::DocumentObjectGroupPython] C_element031  label="C_element : 015"  # scripted group (container) (typed FeaturePython)
  n = 6
  ref = C_element
FEATURE [App::DocumentObjectGroupPython] H_element028  label="H_element : 12"  # scripted group (container) (typed FeaturePython)
  n = 12
  ref = H_element
FEATURE [App::DocumentObjectGroupPython] G4_CYCLOHEXANE  # scripted group (container) (typed FeaturePython)
  Dunit = g/cm3
  Dvalue = 0.779
  Group = -> [C_element031,H_element028]
  conduct = 2
  density = 1
  expand = 3
  formula = G4_CYCLOHEXANE
  name = G4_CYCLOHEXANE
  specific = 4
FEATURE [App::DocumentObjectGroupPython] C_element032  label="C_element : 016"  # scripted group (container) (typed FeaturePython)
  n = 6
  ref = C_element
FEATURE [App::DocumentObjectGroupPython] H_element029  label="H_element : 4"  # scripted group (container) (typed FeaturePython)
  n = 4
  ref = H_element
FEATURE [App::DocumentObjectGroupPython] Cl_element007  label="Cl_element : 2"  # scripted group (container) (typed FeaturePython)
  n = 2
  ref = Cl_element
FEATURE [App::DocumentObjectGroupPython] G4_1_2_DICHLOROBENZENE  label="G4_1.2-DICHLOROBENZENE"  # scripted group (container) (typed FeaturePython)
  Dunit = g/cm3
  Dvalue = 1.3048
  Group = -> [C_element032,H_element029,Cl_element007]
  conduct = 2
  density = 1
  expand = 3
  formula = G4_1.2-DICHLOROBENZENE
  name = G4_1.2-DICHLOROBENZENE
  specific = 4
FEATURE [App::DocumentObjectGroupPython] C_element033  label="C_element : 017"  # scripted group (container) (typed FeaturePython)
  n = 4
  ref = C_element
FEATURE [App::DocumentObjectGroupPython] H_element030  label="H_element : 8"  # scripted group (container) (typed FeaturePython)
  n = 8
  ref = H_element
FEATURE [App::DocumentObjectGroupPython] O_element031  label="O_element : 014"  # scripted group (container) (typed FeaturePython)
  n = 1
  ref = O_element
FEATURE [App::DocumentObjectGroupPython] Cl_element008  label="Cl_element : 005"  # scripted group (container) (typed FeaturePython)
  n = 2
  ref = Cl_element
FEATURE [App::DocumentObjectGroupPython] G4_DICHLORODIETHYL_ETHER  # scripted group (container) (typed FeaturePython)
  Dunit = g/cm3
  Dvalue = 1.2199
  Group = -> [C_element033,H_element030,O_element031,Cl_element008]
  conduct = 2
  density = 1
  expand = 3
  formula = G4_DICHLORODIETHYL_ETHER
  name = G4_DICHLORODIETHYL_ETHER
  specific = 4
FEATURE [App::DocumentObjectGroupPython] C_element034  label="C_element : 018"  # scripted group (container) (typed FeaturePython)
  n = 2
  ref = C_element
FEATURE [App::DocumentObjectGroupPython] H_element031  label="H_element : 014"  # scripted group (container) (typed FeaturePython)
  n = 4
  ref = H_element
FEATURE [App::DocumentObjectGroupPython] Cl_element009  label="Cl_element : 006"  # scripted group (container) (typed FeaturePython)
  n = 2
  ref = Cl_element
FEATURE [App::DocumentObjectGroupPython] G4_1_2_DICHLOROETHANE  label="G4_1.2-DICHLOROETHANE"  # scripted group (container) (typed FeaturePython)
  Dunit = g/cm3
  Dvalue = 1.2351
  Group = -> [C_element034,H_element031,Cl_element009]
  conduct = 2
  density = 1
  expand = 3
  formula = G4_1.2-DICHLOROETHANE
  name = G4_1.2-DICHLOROETHANE
  specific = 4
FEATURE [App::DocumentObjectGroupPython] C_element035  label="C_element : 019"  # scripted group (container) (typed FeaturePython)
  n = 4
  ref = C_element
FEATURE [App::DocumentObjectGroupPython] H_element032  label="H_element : 015"  # scripted group (container) (typed FeaturePython)
  n = 10
  ref = H_element
FEATURE [App::DocumentObjectGroupPython] O_element032  label="O_element : 015"  # scripted group (container) (typed FeaturePython)
  n = 1
  ref = O_element
FEATURE [App::DocumentObjectGroupPython] G4_DIETHYL_ETHER  # scripted group (container) (typed FeaturePython)
  Dunit = g/cm3
  Dvalue = 0.71378
  Group = -> [C_element035,H_element032,O_element032]
  conduct = 2
  density = 1
  expand = 3
  formula = G4_DIETHYL_ETHER
  name = G4_DIETHYL_ETHER
  specific = 4
FEATURE [App::DocumentObjectGroupPython] C_element036  label="C_element : 020"  # scripted group (container) (typed FeaturePython)
  n = 3
  ref = C_element
FEATURE [App::DocumentObjectGroupPython] H_element033  label="H_element : 016"  # scripted group (container) (typed FeaturePython)
  n = 7
  ref = H_element
FEATURE [App::DocumentObjectGroupPython] N_element015  label="N_element : 008"  # scripted group (container) (typed FeaturePython)
  n = 1
  ref = N_element
FEATURE [App::DocumentObjectGroupPython] O_element033  label="O_element : 016"  # scripted group (container) (typed FeaturePython)
  n = 1
  ref = O_element
FEATURE [App::DocumentObjectGroupPython] G4_N_N_DIMETHYL_FORMAMIDE  label="G4_N.N-DIMETHYL_FORMAMIDE"  # scripted group (container) (typed FeaturePython)
  Dunit = g/cm3
  Dvalue = 0.9487
  Group = -> [C_element036,H_element033,N_element015,O_element033]
  conduct = 2
  density = 1
  expand = 3
  formula = G4_N.N-DIMETHYL_FORMAMIDE
  name = G4_N.N-DIMETHYL_FORMAMIDE
  specific = 4
FEATURE [App::DocumentObjectGroupPython] C_element037  label="C_element : 021"  # scripted group (container) (typed FeaturePython)
  n = 2
  ref = C_element
FEATURE [App::DocumentObjectGroupPython] H_element034  label="H_element : 017"  # scripted group (container) (typed FeaturePython)
  n = 6
  ref = H_element
FEATURE [App::DocumentObjectGroupPython] O_element034  label="O_element : 017"  # scripted group (container) (typed FeaturePython)
  n = 1
  ref = O_element
FEATURE [App::DocumentObjectGroupPython] S_element009  label="S_element : 003"  # scripted group (container) (typed FeaturePython)
  n = 1
  ref = S_element
FEATURE [App::DocumentObjectGroupPython] G4_DIMETHYL_SULFOXIDE  # scripted group (container) (typed FeaturePython)
  Dunit = g/cm3
  Dvalue = 1.1014
  Group = -> [C_element037,H_element034,O_element034,S_element009]
  conduct = 2
  density = 1
  expand = 3
  formula = G4_DIMETHYL_SULFOXIDE
  name = G4_DIMETHYL_SULFOXIDE
  specific = 4
FEATURE [App::DocumentObjectGroupPython] C_element038  label="C_element : 022"  # scripted group (container) (typed FeaturePython)
  n = 2
  ref = C_element
FEATURE [App::DocumentObjectGroupPython] H_element035  label="H_element : 018"  # scripted group (container) (typed FeaturePython)
  n = 6
  ref = H_element
FEATURE [App::DocumentObjectGroupPython] G4_ETHANE  # scripted group (container) (typed FeaturePython)
  Dunit = g/cm3
  Dvalue = 0.00125324
  Group = -> [C_element038,H_element035]
  conduct = 2
  density = 1
  expand = 3
  formula = G4_ETHANE
  name = G4_ETHANE
  specific = 4
FEATURE [App::DocumentObjectGroupPython] C_element039  label="C_element : 023"  # scripted group (container) (typed FeaturePython)
  n = 2
  ref = C_element
FEATURE [App::DocumentObjectGroupPython] H_element036  label="H_element : 019"  # scripted group (container) (typed FeaturePython)
  n = 6
  ref = H_element
FEATURE [App::DocumentObjectGroupPython] O_element035  label="O_element : 018"  # scripted group (container) (typed FeaturePython)
  n = 1
  ref = O_element
FEATURE [App::DocumentObjectGroupPython] G4_ETHYL_ALCOHOL  # scripted group (container) (typed FeaturePython)
  Dunit = g/cm3
  Dvalue = 0.7893
  Group = -> [C_element039,H_element036,O_element035]
  conduct = 2
  density = 1
  expand = 3
  formula = G4_ETHYL_ALCOHOL
  name = G4_ETHYL_ALCOHOL
  specific = 4
FEATURE [App::DocumentObjectGroupPython] H_element037  label="H_element : 0.090"  # scripted group (container) (typed FeaturePython)
  n = 0.090027
FEATURE [App::DocumentObjectGroupPython] C_element040  label="C_element : 0.585"  # scripted group (container) (typed FeaturePython)
  n = 0.585182
FEATURE [App::DocumentObjectGroupPython] O_element036  label="O_element : 0.325"  # scripted group (container) (typed FeaturePython)
  n = 0.324791
FEATURE [App::DocumentObjectGroupPython] G4_ETHYL_CELLULOSE  # scripted group (container) (typed FeaturePython)
  Dunit = g/cm3
  Dvalue = 1.13
  Group = -> [H_element037,C_element040,O_element036]
  conduct = 2
  density = 1
  expand = 3
  formula = G4_ETHYL_CELLULOSE
  name = G4_ETHYL_CELLULOSE
  specific = 4
FEATURE [App::DocumentObjectGroupPython] C_element041  label="C_element : 024"  # scripted group (container) (typed FeaturePython)
  n = 2
  ref = C_element
FEATURE [App::DocumentObjectGroupPython] H_element038  label="H_element : 020"  # scripted group (container) (typed FeaturePython)
  n = 4
  ref = H_element
FEATURE [App::DocumentObjectGroupPython] G4_ETHYLENE  # scripted group (container) (typed FeaturePython)
  Dunit = g/cm3
  Dvalue = 0.00117497
  Group = -> [C_element041,H_element038]
  conduct = 2
  density = 1
  expand = 3
  formula = G4_ETHYLENE
  name = G4_ETHYLENE
  specific = 4
FEATURE [App::DocumentObjectGroupPython] H_element039  label="H_element : 0.096"  # scripted group (container) (typed FeaturePython)
  n = 0.096
FEATURE [App::DocumentObjectGroupPython] C_element042  label="C_element : 0.195"  # scripted group (container) (typed FeaturePython)
  n = 0.195
FEATURE [App::DocumentObjectGroupPython] N_element016  label="N_element : 0.057"  # scripted group (container) (typed FeaturePython)
  n = 0.057
FEATURE [App::DocumentObjectGroupPython] O_element037  label="O_element : 0.646"  # scripted group (container) (typed FeaturePython)
  n = 0.646
FEATURE [App::DocumentObjectGroupPython] Na_element006  label="Na_element : 0.017"  # scripted group (container) (typed FeaturePython)
  n = 0.001
FEATURE [App::DocumentObjectGroupPython] P_element005  label="P_element : 0.104"  # scripted group (container) (typed FeaturePython)
  n = 0.001
FEATURE [App::DocumentObjectGroupPython] S_element010  label="S_element : 0.016"  # scripted group (container) (typed FeaturePython)
  n = 0.003
FEATURE [App::DocumentObjectGroupPython] Cl_element010  label="Cl_element : 0.005"  # scripted group (container) (typed FeaturePython)
  n = 0.001
FEATURE [App::DocumentObjectGroupPython] G4_EYE_LENS_ICRP  # scripted group (container) (typed FeaturePython)
  Dunit = g/cm3
  Dvalue = 1.07
  Group = -> [H_element039,C_element042,N_element016,O_element037,Na_element006,P_element005,S_element010,Cl_element010]
  conduct = 2
  density = 1
  expand = 3
  formula = G4_EYE_LENS_ICRP
  name = G4_EYE_LENS_ICRP
  specific = 4
FEATURE [App::DocumentObjectGroupPython] Fe_element003  label="Fe_element : 2"  # scripted group (container) (typed FeaturePython)
  n = 2
  ref = Fe_element
FEATURE [App::DocumentObjectGroupPython] O_element038  label="O_element : 019"  # scripted group (container) (typed FeaturePython)
  n = 3
  ref = O_element
FEATURE [App::DocumentObjectGroupPython] G4_FERRIC_OXIDE  # scripted group (container) (typed FeaturePython)
  Dunit = g/cm3
  Dvalue = 5.2
  Group = -> [Fe_element003,O_element038]
  conduct = 2
  density = 1
  expand = 3
  formula = G4_FERRIC_OXIDE
  name = G4_FERRIC_OXIDE
  specific = 4
FEATURE [App::DocumentObjectGroupPython] Fe_element004  label="Fe_element : 1"  # scripted group (container) (typed FeaturePython)
  n = 1
  ref = Fe_element
FEATURE [App::DocumentObjectGroupPython] B_element003  label="B_element : 1"  # scripted group (container) (typed FeaturePython)
  n = 1
  ref = B_element
FEATURE [App::DocumentObjectGroupPython] G4_FERROBORIDE  # scripted group (container) (typed FeaturePython)
  Dunit = g/cm3
  Dvalue = 7.15
  Group = -> [Fe_element004,B_element003]
  conduct = 2
  density = 1
  expand = 3
  formula = G4_FERROBORIDE
  name = G4_FERROBORIDE
  specific = 4
FEATURE [App::DocumentObjectGroupPython] Fe_element005  label="Fe_element : 003"  # scripted group (container) (typed FeaturePython)
  n = 1
  ref = Fe_element
FEATURE [App::DocumentObjectGroupPython] O_element039  label="O_element : 020"  # scripted group (container) (typed FeaturePython)
  n = 1
  ref = O_element
FEATURE [App::DocumentObjectGroupPython] G4_FERROUS_OXIDE  # scripted group (container) (typed FeaturePython)
  Dunit = g/cm3
  Dvalue = 5.7
  Group = -> [Fe_element005,O_element039]
  conduct = 2
  density = 1
  expand = 3
  formula = G4_FERROUS_OXIDE
  name = G4_FERROUS_OXIDE
  specific = 4
FEATURE [App::DocumentObjectGroupPython] H_element040  label="H_element : 0.115"  # scripted group (container) (typed FeaturePython)
  n = 0.108259
FEATURE [App::DocumentObjectGroupPython] N_element017  label="N_element : 0.000"  # scripted group (container) (typed FeaturePython)
  n = 2.7e-05
FEATURE [App::DocumentObjectGroupPython] O_element040  label="O_element : 0.879"  # scripted group (container) (typed FeaturePython)
  n = 0.878636
FEATURE [App::DocumentObjectGroupPython] Na_element007  label="Na_element : 0.000"  # scripted group (container) (typed FeaturePython)
  n = 2.2e-05
FEATURE [App::DocumentObjectGroupPython] S_element011  label="S_element : 0.013"  # scripted group (container) (typed FeaturePython)
  n = 0.012968
FEATURE [App::DocumentObjectGroupPython] Cl_element011  label="Cl_element : 0.000"  # scripted group (container) (typed FeaturePython)
  n = 3.4e-05
FEATURE [App::DocumentObjectGroupPython] Fe_element006  label="Fe_element : 0.000"  # scripted group (container) (typed FeaturePython)
  n = 5.4e-05
FEATURE [App::DocumentObjectGroupPython] G4_FERROUS_SULFATE  # scripted group (container) (typed FeaturePython)
  Dunit = g/cm3
  Dvalue = 1.024
  Group = -> [H_element040,N_element017,O_element040,Na_element007,S_element011,Cl_element011,Fe_element006]
  conduct = 2
  density = 1
  expand = 3
  formula = G4_FERROUS_SULFATE
  name = G4_FERROUS_SULFATE
  specific = 4
FEATURE [App::DocumentObjectGroupPython] C_element043  label="C_element : 0.099"  # scripted group (container) (typed FeaturePython)
  n = 0.099335
FEATURE [App::DocumentObjectGroupPython] F_element007  label="F_element : 0.314"  # scripted group (container) (typed FeaturePython)
  n = 0.314247
FEATURE [App::DocumentObjectGroupPython] Cl_element012  label="Cl_element : 0.586"  # scripted group (container) (typed FeaturePython)
  n = 0.586418
FEATURE [App::DocumentObjectGroupPython] G4_FREON_12  label="G4_FREON-12"  # scripted group (container) (typed FeaturePython)
  Dunit = g/cm3
  Dvalue = 1.12
  Group = -> [C_element043,F_element007,Cl_element012]
  conduct = 2
  density = 1
  expand = 3
  formula = G4_FREON-12
  name = G4_FREON-12
  specific = 4
FEATURE [App::DocumentObjectGroupPython] C_element044  label="C_element : 0.057"  # scripted group (container) (typed FeaturePython)
  n = 0.057245
FEATURE [App::DocumentObjectGroupPython] F_element008  label="F_element : 0.181"  # scripted group (container) (typed FeaturePython)
  n = 0.181096
FEATURE [App::DocumentObjectGroupPython] Br_element001  label="Br_element : 0.762"  # scripted group (container) (typed FeaturePython)
  n = 0.761659
FEATURE [App::DocumentObjectGroupPython] G4_FREON_12B2  label="G4_FREON-12B2"  # scripted group (container) (typed FeaturePython)
  Dunit = g/cm3
  Dvalue = 1.8
  Group = -> [C_element044,F_element008,Br_element001]
  conduct = 2
  density = 1
  expand = 3
  formula = G4_FREON-12B2
  name = G4_FREON-12B2
  specific = 4
FEATURE [App::DocumentObjectGroupPython] C_element045  label="C_element : 0.115"  # scripted group (container) (typed FeaturePython)
  n = 0.114983
FEATURE [App::DocumentObjectGroupPython] F_element009  label="F_element : 0.546"  # scripted group (container) (typed FeaturePython)
  n = 0.545621
FEATURE [App::DocumentObjectGroupPython] Cl_element013  label="Cl_element : 0.339"  # scripted group (container) (typed FeaturePython)
  n = 0.339396
FEATURE [App::DocumentObjectGroupPython] G4_FREON_13  label="G4_FREON-13"  # scripted group (container) (typed FeaturePython)
  Dunit = g/cm3
  Dvalue = 0.95
  Group = -> [C_element045,F_element009,Cl_element013]
  conduct = 2
  density = 1
  expand = 3
  formula = G4_FREON-13
  name = G4_FREON-13
  specific = 4
FEATURE [App::DocumentObjectGroupPython] C_element046  label="C_element : 025"  # scripted group (container) (typed FeaturePython)
  n = 1
  ref = C_element
FEATURE [App::DocumentObjectGroupPython] F_element010  label="F_element : 3"  # scripted group (container) (typed FeaturePython)
  n = 3
  ref = F_element
FEATURE [App::DocumentObjectGroupPython] Br_element002  label="Br_element : 1"  # scripted group (container) (typed FeaturePython)
  n = 1
  ref = Br_element
FEATURE [App::DocumentObjectGroupPython] G4_FREON_13B1  label="G4_FREON-13B1"  # scripted group (container) (typed FeaturePython)
  Dunit = g/cm3
  Dvalue = 1.5
  Group = -> [C_element046,F_element010,Br_element002]
  conduct = 2
  density = 1
  expand = 3
  formula = G4_FREON-13B1
  name = G4_FREON-13B1
  specific = 4
FEATURE [App::DocumentObjectGroupPython] C_element047  label="C_element : 0.061"  # scripted group (container) (typed FeaturePython)
  n = 0.061309
FEATURE [App::DocumentObjectGroupPython] F_element011  label="F_element : 0.291"  # scripted group (container) (typed FeaturePython)
  n = 0.290924
FEATURE [App::DocumentObjectGroupPython] I_element002  label="I_element : 0.648"  # scripted group (container) (typed FeaturePython)
  n = 0.647767
FEATURE [App::DocumentObjectGroupPython] G4_FREON_13I1  label="G4_FREON-13I1"  # scripted group (container) (typed FeaturePython)
  Dunit = g/cm3
  Dvalue = 1.8
  Group = -> [C_element047,F_element011,I_element002]
  conduct = 2
  density = 1
  expand = 3
  formula = G4_FREON-13I1
  name = G4_FREON-13I1
  specific = 4
FEATURE [App::DocumentObjectGroupPython] Gd_element001  label="Gd_element : 2"  # scripted group (container) (typed FeaturePython)
  n = 2
  ref = Gd_element
FEATURE [App::DocumentObjectGroupPython] O_element041  label="O_element : 021"  # scripted group (container) (typed FeaturePython)
  n = 2
  ref = O_element
FEATURE [App::DocumentObjectGroupPython] S_element012  label="S_element : 004"  # scripted group (container) (typed FeaturePython)
  n = 1
  ref = S_element
FEATURE [App::DocumentObjectGroupPython] G4_GADOLINIUM_OXYSULFIDE  # scripted group (container) (typed FeaturePython)
  Dunit = g/cm3
  Dvalue = 7.44
  Group = -> [Gd_element001,O_element041,S_element012]
  conduct = 2
  density = 1
  expand = 3
  formula = G4_GADOLINIUM_OXYSULFIDE
  name = G4_GADOLINIUM_OXYSULFIDE
  specific = 4
FEATURE [App::DocumentObjectGroupPython] Ga_element001  label="Ga_element : 1"  # scripted group (container) (typed FeaturePython)
  n = 1
  ref = Ga_element
FEATURE [App::DocumentObjectGroupPython] As_element001  label="As_element : 1"  # scripted group (container) (typed FeaturePython)
  n = 1
  ref = As_element
FEATURE [App::DocumentObjectGroupPython] G4_GALLIUM_ARSENIDE  # scripted group (container) (typed FeaturePython)
  Dunit = g/cm3
  Dvalue = 5.31
  Group = -> [Ga_element001,As_element001]
  conduct = 2
  density = 1
  expand = 3
  formula = G4_GALLIUM_ARSENIDE
  name = G4_GALLIUM_ARSENIDE
  specific = 4
FEATURE [App::DocumentObjectGroupPython] H_element041  label="H_element : 0.081"  # scripted group (container) (typed FeaturePython)
  n = 0.08118
FEATURE [App::DocumentObjectGroupPython] C_element048  label="C_element : 0.416"  # scripted group (container) (typed FeaturePython)
  n = 0.41606
FEATURE [App::DocumentObjectGroupPython] N_element018  label="N_element : 0.111"  # scripted group (container) (typed FeaturePython)
  n = 0.11124
FEATURE [App::DocumentObjectGroupPython] O_element042  label="O_element : 0.381"  # scripted group (container) (typed FeaturePython)
  n = 0.38064
FEATURE [App::DocumentObjectGroupPython] S_element013  label="S_element : 0.011"  # scripted group (container) (typed FeaturePython)
  n = 0.01088
FEATURE [App::DocumentObjectGroupPython] G4_GEL_PHOTO_EMULSION  # scripted group (container) (typed FeaturePython)
  Dunit = g/cm3
  Dvalue = 1.2914
  Group = -> [H_element041,C_element048,N_element018,O_element042,S_element013]
  conduct = 2
  density = 1
  expand = 3
  formula = G4_GEL_PHOTO_EMULSION
  name = G4_GEL_PHOTO_EMULSION
  specific = 4
FEATURE [App::DocumentObjectGroupPython] B_element004  label="B_element : 0.040"  # scripted group (container) (typed FeaturePython)
  n = 0.0400639
FEATURE [App::DocumentObjectGroupPython] O_element043  label="O_element : 0.540"  # scripted group (container) (typed FeaturePython)
  n = 0.539561
FEATURE [App::DocumentObjectGroupPython] Na_element008  label="Na_element : 0.028"  # scripted group (container) (typed FeaturePython)
  n = 0.0281909
FEATURE [App::DocumentObjectGroupPython] Al_element003  label="Al_element : 0.012"  # scripted group (container) (typed FeaturePython)
  n = 0.011644
FEATURE [App::DocumentObjectGroupPython] Si_element003  label="Si_element : 0.377"  # scripted group (container) (typed FeaturePython)
  n = 0.377219
FEATURE [App::DocumentObjectGroupPython] K_element004  label="K_element : 0.014"  # scripted group (container) (typed FeaturePython)
  n = 0.00332099
FEATURE [App::DocumentObjectGroupPython] G4_Pyrex_Glass  # scripted group (container) (typed FeaturePython)
  Dunit = g/cm3
  Dvalue = 2.23
  Group = -> [B_element004,O_element043,Na_element008,Al_element003,Si_element003,K_element004]
  conduct = 2
  density = 1
  expand = 3
  formula = G4_Pyrex_Glass
  name = G4_Pyrex_Glass
  specific = 4
FEATURE [App::DocumentObjectGroupPython] O_element044  label="O_element : 0.156"  # scripted group (container) (typed FeaturePython)
  n = 0.156453
FEATURE [App::DocumentObjectGroupPython] Si_element004  label="Si_element : 0.081"  # scripted group (container) (typed FeaturePython)
  n = 0.080866
FEATURE [App::DocumentObjectGroupPython] Ti_element001  label="Ti_element : 0.008"  # scripted group (container) (typed FeaturePython)
  n = 0.008092
FEATURE [App::DocumentObjectGroupPython] As_element002  label="As_element : 0.003"  # scripted group (container) (typed FeaturePython)
  n = 0.002651
FEATURE [App::DocumentObjectGroupPython] Pb_element001  label="Pb_element : 0.752"  # scripted group (container) (typed FeaturePython)
  n = 0.751938
FEATURE [App::DocumentObjectGroupPython] G4_GLASS_LEAD  # scripted group (container) (typed FeaturePython)
  Dunit = g/cm3
  Dvalue = 6.22
  Group = -> [O_element044,Si_element004,Ti_element001,As_element002,Pb_element001]
  conduct = 2
  density = 1
  expand = 3
  formula = G4_GLASS_LEAD
  name = G4_GLASS_LEAD
  specific = 4
FEATURE [App::DocumentObjectGroupPython] O_element045  label="O_element : 0.460"  # scripted group (container) (typed FeaturePython)
  n = 0.4598
FEATURE [App::DocumentObjectGroupPython] Na_element009  label="Na_element : 0.096"  # scripted group (container) (typed FeaturePython)
  n = 0.0964411
FEATURE [App::DocumentObjectGroupPython] Si_element005  label="Si_element : 0.378"  # scripted group (container) (typed FeaturePython)
  n = 0.336553
FEATURE [App::DocumentObjectGroupPython] Ca_element011  label="Ca_element : 0.107"  # scripted group (container) (typed FeaturePython)
  n = 0.107205
FEATURE [App::DocumentObjectGroupPython] G4_GLASS_PLATE  # scripted group (container) (typed FeaturePython)
  Dunit = g/cm3
  Dvalue = 2.4
  Group = -> [O_element045,Na_element009,Si_element005,Ca_element011]
  conduct = 2
  density = 1
  expand = 3
  formula = G4_GLASS_PLATE
  name = G4_GLASS_PLATE
  specific = 4
FEATURE [App::DocumentObjectGroupPython] C_element049  label="C_element : 026"  # scripted group (container) (typed FeaturePython)
  n = 5
  ref = C_element
FEATURE [App::DocumentObjectGroupPython] H_element042  label="H_element : 021"  # scripted group (container) (typed FeaturePython)
  n = 10
  ref = H_element
FEATURE [App::DocumentObjectGroupPython] N_element019  label="N_element : 2"  # scripted group (container) (typed FeaturePython)
  n = 2
  ref = N_element
FEATURE [App::DocumentObjectGroupPython] O_element046  label="O_element : 022"  # scripted group (container) (typed FeaturePython)
  n = 3
  ref = O_element
FEATURE [App::DocumentObjectGroupPython] G4_GLUTAMINE  # scripted group (container) (typed FeaturePython)
  Dunit = g/cm3
  Dvalue = 1.46
  Group = -> [C_element049,H_element042,N_element019,O_element046]
  conduct = 2
  density = 1
  expand = 3
  formula = G4_GLUTAMINE
  name = G4_GLUTAMINE
  specific = 4
FEATURE [App::DocumentObjectGroupPython] C_element050  label="C_element : 027"  # scripted group (container) (typed FeaturePython)
  n = 3
  ref = C_element
FEATURE [App::DocumentObjectGroupPython] H_element043  label="H_element : 022"  # scripted group (container) (typed FeaturePython)
  n = 8
  ref = H_element
FEATURE [App::DocumentObjectGroupPython] O_element047  label="O_element : 023"  # scripted group (container) (typed FeaturePython)
  n = 3
  ref = O_element
FEATURE [App::DocumentObjectGroupPython] G4_GLYCEROL  # scripted group (container) (typed FeaturePython)
  Dunit = g/cm3
  Dvalue = 1.2613
  Group = -> [C_element050,H_element043,O_element047]
  conduct = 2
  density = 1
  expand = 3
  formula = G4_GLYCEROL
  name = G4_GLYCEROL
  specific = 4
FEATURE [App::DocumentObjectGroupPython] C_element051  label="C_element : 028"  # scripted group (container) (typed FeaturePython)
  n = 5
  ref = C_element
FEATURE [App::DocumentObjectGroupPython] H_element044  label="H_element : 023"  # scripted group (container) (typed FeaturePython)
  n = 5
  ref = H_element
FEATURE [App::DocumentObjectGroupPython] N_element020  label="N_element : 009"  # scripted group (container) (typed FeaturePython)
  n = 5
  ref = N_element
FEATURE [App::DocumentObjectGroupPython] O_element048  label="O_element : 024"  # scripted group (container) (typed FeaturePython)
  n = 1
  ref = O_element
FEATURE [App::DocumentObjectGroupPython] G4_GUANINE  # scripted group (container) (typed FeaturePython)
  Dunit = g/cm3
  Dvalue = 2.2
  Group = -> [C_element051,H_element044,N_element020,O_element048]
  conduct = 2
  density = 1
  expand = 3
  formula = G4_GUANINE
  name = G4_GUANINE
  specific = 4
FEATURE [App::DocumentObjectGroupPython] Ca_element012  label="Ca_element : 006"  # scripted group (container) (typed FeaturePython)
  n = 1
  ref = Ca_element
FEATURE [App::DocumentObjectGroupPython] S_element014  label="S_element : 005"  # scripted group (container) (typed FeaturePython)
  n = 1
  ref = S_element
FEATURE [App::DocumentObjectGroupPython] O_element049  label="O_element : 6"  # scripted group (container) (typed FeaturePython)
  n = 6
  ref = O_element
FEATURE [App::DocumentObjectGroupPython] H_element045  label="H_element : 024"  # scripted group (container) (typed FeaturePython)
  n = 4
  ref = H_element
FEATURE [App::DocumentObjectGroupPython] G4_GYPSUM  # scripted group (container) (typed FeaturePython)
  Dunit = g/cm3
  Dvalue = 2.32
  Group = -> [Ca_element012,S_element014,O_element049,H_element045]
  conduct = 2
  density = 1
  expand = 3
  formula = G4_GYPSUM
  name = G4_GYPSUM
  specific = 4
FEATURE [App::DocumentObjectGroupPython] C_element052  label="C_element : 7"  # scripted group (container) (typed FeaturePython)
  n = 7
  ref = C_element
FEATURE [App::DocumentObjectGroupPython] H_element046  label="H_element : 16"  # scripted group (container) (typed FeaturePython)
  n = 16
  ref = H_element
FEATURE [App::DocumentObjectGroupPython] G4_N_HEPTANE  label="G4_N-HEPTANE"  # scripted group (container) (typed FeaturePython)
  Dunit = g/cm3
  Dvalue = 0.68376
  Group = -> [C_element052,H_element046]
  conduct = 2
  density = 1
  expand = 3
  formula = G4_N-HEPTANE
  name = G4_N-HEPTANE
  specific = 4
FEATURE [App::DocumentObjectGroupPython] C_element053  label="C_element : 029"  # scripted group (container) (typed FeaturePython)
  n = 6
  ref = C_element
FEATURE [App::DocumentObjectGroupPython] H_element047  label="H_element : 14"  # scripted group (container) (typed FeaturePython)
  n = 14
  ref = H_element
FEATURE [App::DocumentObjectGroupPython] G4_N_HEXANE  label="G4_N-HEXANE"  # scripted group (container) (typed FeaturePython)
  Dunit = g/cm3
  Dvalue = 0.6603
  Group = -> [C_element053,H_element047]
  conduct = 2
  density = 1
  expand = 3
  formula = G4_N-HEXANE
  name = G4_N-HEXANE
  specific = 4
FEATURE [App::DocumentObjectGroupPython] C_element054  label="C_element : 22"  # scripted group (container) (typed FeaturePython)
  n = 22
  ref = C_element
FEATURE [App::DocumentObjectGroupPython] H_element048  label="H_element : 025"  # scripted group (container) (typed FeaturePython)
  n = 10
  ref = H_element
FEATURE [App::DocumentObjectGroupPython] N_element021  label="N_element : 010"  # scripted group (container) (typed FeaturePython)
  n = 2
  ref = N_element
FEATURE [App::DocumentObjectGroupPython] O_element050  label="O_element : 025"  # scripted group (container) (typed FeaturePython)
  n = 5
  ref = O_element
FEATURE [App::DocumentObjectGroupPython] G4_KAPTON  # scripted group (container) (typed FeaturePython)
  Dunit = g/cm3
  Dvalue = 1.42
  Group = -> [C_element054,H_element048,N_element021,O_element050]
  conduct = 2
  density = 1
  expand = 3
  formula = G4_KAPTON
  name = G4_KAPTON
  specific = 4
FEATURE [App::DocumentObjectGroupPython] La_element001  label="La_element : 1"  # scripted group (container) (typed FeaturePython)
  n = 1
  ref = La_element
FEATURE [App::DocumentObjectGroupPython] Br_element003  label="Br_element : 002"  # scripted group (container) (typed FeaturePython)
  n = 1
  ref = Br_element
FEATURE [App::DocumentObjectGroupPython] O_element051  label="O_element : 026"  # scripted group (container) (typed FeaturePython)
  n = 1
  ref = O_element
FEATURE [App::DocumentObjectGroupPython] G4_LANTHANUM_OXYBROMIDE  # scripted group (container) (typed FeaturePython)
  Dunit = g/cm3
  Dvalue = 6.28
  Group = -> [La_element001,Br_element003,O_element051]
  conduct = 2
  density = 1
  expand = 3
  formula = G4_LANTHANUM_OXYBROMIDE
  name = G4_LANTHANUM_OXYBROMIDE
  specific = 4
FEATURE [App::DocumentObjectGroupPython] La_element002  label="La_element : 2"  # scripted group (container) (typed FeaturePython)
  n = 2
  ref = La_element
FEATURE [App::DocumentObjectGroupPython] O_element052  label="O_element : 027"  # scripted group (container) (typed FeaturePython)
  n = 2
  ref = O_element
FEATURE [App::DocumentObjectGroupPython] S_element015  label="S_element : 006"  # scripted group (container) (typed FeaturePython)
  n = 1
  ref = S_element
FEATURE [App::DocumentObjectGroupPython] G4_LANTHANUM_OXYSULFIDE  # scripted group (container) (typed FeaturePython)
  Dunit = g/cm3
  Dvalue = 5.86
  Group = -> [La_element002,O_element052,S_element015]
  conduct = 2
  density = 1
  expand = 3
  formula = G4_LANTHANUM_OXYSULFIDE
  name = G4_LANTHANUM_OXYSULFIDE
  specific = 4
FEATURE [App::DocumentObjectGroupPython] O_element053  label="O_element : 0.072"  # scripted group (container) (typed FeaturePython)
  n = 0.071682
FEATURE [App::DocumentObjectGroupPython] Pb_element002  label="Pb_element : 0.928"  # scripted group (container) (typed FeaturePython)
  n = 0.928318
FEATURE [App::DocumentObjectGroupPython] G4_LEAD_OXIDE  # scripted group (container) (typed FeaturePython)
  Dunit = g/cm3
  Dvalue = 9.53
  Group = -> [O_element053,Pb_element002]
  conduct = 2
  density = 1
  expand = 3
  formula = G4_LEAD_OXIDE
  name = G4_LEAD_OXIDE
  specific = 4
FEATURE [App::DocumentObjectGroupPython] Li_element001  label="Li_element : 1"  # scripted group (container) (typed FeaturePython)
  n = 1
  ref = Li_element
FEATURE [App::DocumentObjectGroupPython] N_element022  label="N_element : 011"  # scripted group (container) (typed FeaturePython)
  n = 1
  ref = N_element
FEATURE [App::DocumentObjectGroupPython] H_element049  label="H_element : 026"  # scripted group (container) (typed FeaturePython)
  n = 2
  ref = H_element
FEATURE [App::DocumentObjectGroupPython] G4_LITHIUM_AMIDE  # scripted group (container) (typed FeaturePython)
  Dunit = g/cm3
  Dvalue = 1.178
  Group = -> [Li_element001,N_element022,H_element049]
  conduct = 2
  density = 1
  expand = 3
  formula = G4_LITHIUM_AMIDE
  name = G4_LITHIUM_AMIDE
  specific = 4
FEATURE [App::DocumentObjectGroupPython] Li_element002  label="Li_element : 2"  # scripted group (container) (typed FeaturePython)
  n = 2
  ref = Li_element
FEATURE [App::DocumentObjectGroupPython] C_element055  label="C_element : 030"  # scripted group (container) (typed FeaturePython)
  n = 1
  ref = C_element
FEATURE [App::DocumentObjectGroupPython] O_element054  label="O_element : 028"  # scripted group (container) (typed FeaturePython)
  n = 3
  ref = O_element
FEATURE [App::DocumentObjectGroupPython] G4_LITHIUM_CARBONATE  # scripted group (container) (typed FeaturePython)
  Dunit = g/cm3
  Dvalue = 2.11
  Group = -> [Li_element002,C_element055,O_element054]
  conduct = 2
  density = 1
  expand = 3
  formula = G4_LITHIUM_CARBONATE
  name = G4_LITHIUM_CARBONATE
  specific = 4
FEATURE [App::DocumentObjectGroupPython] Li_element003  label="Li_element : 003"  # scripted group (container) (typed FeaturePython)
  n = 1
  ref = Li_element
FEATURE [App::DocumentObjectGroupPython] F_element012  label="F_element : 004"  # scripted group (container) (typed FeaturePython)
  n = 1
  ref = F_element
FEATURE [App::DocumentObjectGroupPython] G4_LITHIUM_FLUORIDE  # scripted group (container) (typed FeaturePython)
  Dunit = g/cm3
  Dvalue = 2.635
  Group = -> [Li_element003,F_element012]
  conduct = 2
  density = 1
  expand = 3
  formula = G4_LITHIUM_FLUORIDE
  name = G4_LITHIUM_FLUORIDE
  specific = 4
FEATURE [App::DocumentObjectGroupPython] Li_element004  label="Li_element : 004"  # scripted group (container) (typed FeaturePython)
  n = 1
  ref = Li_element
FEATURE [App::DocumentObjectGroupPython] H_element050  label="H_element : 027"  # scripted group (container) (typed FeaturePython)
  n = 1
  ref = H_element
FEATURE [App::DocumentObjectGroupPython] G4_LITHIUM_HYDRIDE  # scripted group (container) (typed FeaturePython)
  Dunit = g/cm3
  Dvalue = 0.82
  Group = -> [Li_element004,H_element050]
  conduct = 2
  density = 1
  expand = 3
  formula = G4_LITHIUM_HYDRIDE
  name = G4_LITHIUM_HYDRIDE
  specific = 4
FEATURE [App::DocumentObjectGroupPython] Li_element005  label="Li_element : 005"  # scripted group (container) (typed FeaturePython)
  n = 1
  ref = Li_element
FEATURE [App::DocumentObjectGroupPython] I_element003  label="I_element : 002"  # scripted group (container) (typed FeaturePython)
  n = 1
  ref = I_element
FEATURE [App::DocumentObjectGroupPython] G4_LITHIUM_IODIDE  # scripted group (container) (typed FeaturePython)
  Dunit = g/cm3
  Dvalue = 3.494
  Group = -> [Li_element005,I_element003]
  conduct = 2
  density = 1
  expand = 3
  formula = G4_LITHIUM_IODIDE
  name = G4_LITHIUM_IODIDE
  specific = 4
FEATURE [App::DocumentObjectGroupPython] Li_element006  label="Li_element : 006"  # scripted group (container) (typed FeaturePython)
  n = 2
  ref = Li_element
FEATURE [App::DocumentObjectGroupPython] O_element055  label="O_element : 029"  # scripted group (container) (typed FeaturePython)
  n = 1
  ref = O_element
FEATURE [App::DocumentObjectGroupPython] G4_LITHIUM_OXIDE  # scripted group (container) (typed FeaturePython)
  Dunit = g/cm3
  Dvalue = 2.013
  Group = -> [Li_element006,O_element055]
  conduct = 2
  density = 1
  expand = 3
  formula = G4_LITHIUM_OXIDE
  name = G4_LITHIUM_OXIDE
  specific = 4
FEATURE [App::DocumentObjectGroupPython] Li_element007  label="Li_element : 007"  # scripted group (container) (typed FeaturePython)
  n = 2
  ref = Li_element
FEATURE [App::DocumentObjectGroupPython] B_element005  label="B_element : 005"  # scripted group (container) (typed FeaturePython)
  n = 4
  ref = B_element
FEATURE [App::DocumentObjectGroupPython] O_element056  label="O_element : 7"  # scripted group (container) (typed FeaturePython)
  n = 7
  ref = O_element
FEATURE [App::DocumentObjectGroupPython] G4_LITHIUM_TETRABORATE  # scripted group (container) (typed FeaturePython)
  Dunit = g/cm3
  Dvalue = 2.44
  Group = -> [Li_element007,B_element005,O_element056]
  conduct = 2
  density = 1
  expand = 3
  formula = G4_LITHIUM_TETRABORATE
  name = G4_LITHIUM_TETRABORATE
  specific = 4
FEATURE [App::DocumentObjectGroupPython] H_element051  label="H_element : 0.105"  # scripted group (container) (typed FeaturePython)
  n = 0.105
FEATURE [App::DocumentObjectGroupPython] C_element056  label="C_element : 0.083"  # scripted group (container) (typed FeaturePython)
  n = 0.083
FEATURE [App::DocumentObjectGroupPython] N_element023  label="N_element : 0.023"  # scripted group (container) (typed FeaturePython)
  n = 0.023
FEATURE [App::DocumentObjectGroupPython] O_element057  label="O_element : 0.779"  # scripted group (container) (typed FeaturePython)
  n = 0.779
FEATURE [App::DocumentObjectGroupPython] Na_element010  label="Na_element : 0.097"  # scripted group (container) (typed FeaturePython)
  n = 0.002
FEATURE [App::DocumentObjectGroupPython] P_element006  label="P_element : 0.105"  # scripted group (container) (typed FeaturePython)
  n = 0.001
FEATURE [App::DocumentObjectGroupPython] S_element016  label="S_element : 0.017"  # scripted group (container) (typed FeaturePython)
  n = 0.002
FEATURE [App::DocumentObjectGroupPython] Cl_element014  label="Cl_element : 0.587"  # scripted group (container) (typed FeaturePython)
  n = 0.003
FEATURE [App::DocumentObjectGroupPython] K_element005  label="K_element : 0.015"  # scripted group (container) (typed FeaturePython)
  n = 0.002
FEATURE [App::DocumentObjectGroupPython] G4_LUNG_ICRP  # scripted group (container) (typed FeaturePython)
  Dunit = g/cm3
  Dvalue = 1.04
  Group = -> [H_element051,C_element056,N_element023,O_element057,Na_element010,P_element006,S_element016,Cl_element014,K_element005]
  conduct = 2
  density = 1
  expand = 3
  formula = G4_LUNG_ICRP
  name = G4_LUNG_ICRP
  specific = 4
FEATURE [App::DocumentObjectGroupPython] H_element052  label="H_element : 0.116"  # scripted group (container) (typed FeaturePython)
  n = 0.114318
FEATURE [App::DocumentObjectGroupPython] C_element057  label="C_element : 0.656"  # scripted group (container) (typed FeaturePython)
  n = 0.655824
FEATURE [App::DocumentObjectGroupPython] O_element058  label="O_element : 0.092"  # scripted group (container) (typed FeaturePython)
  n = 0.0921831
FEATURE [App::DocumentObjectGroupPython] Mg_element004  label="Mg_element : 0.135"  # scripted group (container) (typed FeaturePython)
  n = 0.134792
FEATURE [App::DocumentObjectGroupPython] Ca_element013  label="Ca_element : 0.003"  # scripted group (container) (typed FeaturePython)
  n = 0.002883
FEATURE [App::DocumentObjectGroupPython] G4_M3_WAX  # scripted group (container) (typed FeaturePython)
  Dunit = g/cm3
  Dvalue = 1.05
  Group = -> [H_element052,C_element057,O_element058,Mg_element004,Ca_element013]
  conduct = 2
  density = 1
  expand = 3
  formula = G4_M3_WAX
  name = G4_M3_WAX
  specific = 4
FEATURE [App::DocumentObjectGroupPython] Mg_element005  label="Mg_element : 1"  # scripted group (container) (typed FeaturePython)
  n = 1
  ref = Mg_element
FEATURE [App::DocumentObjectGroupPython] C_element058  label="C_element : 031"  # scripted group (container) (typed FeaturePython)
  n = 1
  ref = C_element
FEATURE [App::DocumentObjectGroupPython] O_element059  label="O_element : 030"  # scripted group (container) (typed FeaturePython)
  n = 3
  ref = O_element
FEATURE [App::DocumentObjectGroupPython] G4_MAGNESIUM_CARBONATE  # scripted group (container) (typed FeaturePython)
  Dunit = g/cm3
  Dvalue = 2.958
  Group = -> [Mg_element005,C_element058,O_element059]
  conduct = 2
  density = 1
  expand = 3
  formula = G4_MAGNESIUM_CARBONATE
  name = G4_MAGNESIUM_CARBONATE
  specific = 4
FEATURE [App::DocumentObjectGroupPython] Mg_element006  label="Mg_element : 002"  # scripted group (container) (typed FeaturePython)
  n = 1
  ref = Mg_element
FEATURE [App::DocumentObjectGroupPython] F_element013  label="F_element : 005"  # scripted group (container) (typed FeaturePython)
  n = 2
  ref = F_element
FEATURE [App::DocumentObjectGroupPython] G4_MAGNESIUM_FLUORIDE  # scripted group (container) (typed FeaturePython)
  Dunit = g/cm3
  Dvalue = 3
  Group = -> [Mg_element006,F_element013]
  conduct = 2
  density = 1
  expand = 3
  formula = G4_MAGNESIUM_FLUORIDE
  name = G4_MAGNESIUM_FLUORIDE
  specific = 4
FEATURE [App::DocumentObjectGroupPython] Mg_element007  label="Mg_element : 003"  # scripted group (container) (typed FeaturePython)
  n = 1
  ref = Mg_element
FEATURE [App::DocumentObjectGroupPython] O_element060  label="O_element : 031"  # scripted group (container) (typed FeaturePython)
  n = 1
  ref = O_element
FEATURE [App::DocumentObjectGroupPython] G4_MAGNESIUM_OXIDE  # scripted group (container) (typed FeaturePython)
  Dunit = g/cm3
  Dvalue = 3.58
  Group = -> [Mg_element007,O_element060]
  conduct = 2
  density = 1
  expand = 3
  formula = G4_MAGNESIUM_OXIDE
  name = G4_MAGNESIUM_OXIDE
  specific = 4
FEATURE [App::DocumentObjectGroupPython] Mg_element008  label="Mg_element : 004"  # scripted group (container) (typed FeaturePython)
  n = 1
  ref = Mg_element
FEATURE [App::DocumentObjectGroupPython] B_element006  label="B_element : 006"  # scripted group (container) (typed FeaturePython)
  n = 4
  ref = B_element
FEATURE [App::DocumentObjectGroupPython] O_element061  label="O_element : 032"  # scripted group (container) (typed FeaturePython)
  n = 7
  ref = O_element
FEATURE [App::DocumentObjectGroupPython] G4_MAGNESIUM_TETRABORATE  # scripted group (container) (typed FeaturePython)
  Dunit = g/cm3
  Dvalue = 2.53
  Group = -> [Mg_element008,B_element006,O_element061]
  conduct = 2
  density = 1
  expand = 3
  formula = G4_MAGNESIUM_TETRABORATE
  name = G4_MAGNESIUM_TETRABORATE
  specific = 4
FEATURE [App::DocumentObjectGroupPython] Hg_element001  label="Hg_element : 1"  # scripted group (container) (typed FeaturePython)
  n = 1
  ref = Hg_element
FEATURE [App::DocumentObjectGroupPython] I_element004  label="I_element : 2"  # scripted group (container) (typed FeaturePython)
  n = 2
  ref = I_element
FEATURE [App::DocumentObjectGroupPython] G4_MERCURIC_IODIDE  # scripted group (container) (typed FeaturePython)
  Dunit = g/cm3
  Dvalue = 6.36
  Group = -> [Hg_element001,I_element004]
  conduct = 2
  density = 1
  expand = 3
  formula = G4_MERCURIC_IODIDE
  name = G4_MERCURIC_IODIDE
  specific = 4
FEATURE [App::DocumentObjectGroupPython] C_element059  label="C_element : 032"  # scripted group (container) (typed FeaturePython)
  n = 1
  ref = C_element
FEATURE [App::DocumentObjectGroupPython] H_element053  label="H_element : 028"  # scripted group (container) (typed FeaturePython)
  n = 4
  ref = H_element
FEATURE [App::DocumentObjectGroupPython] G4_METHANE  # scripted group (container) (typed FeaturePython)
  Dunit = g/cm3
  Dvalue = 0.000667151
  Group = -> [C_element059,H_element053]
  conduct = 2
  density = 1
  expand = 3
  formula = G4_METHANE
  name = G4_METHANE
  specific = 4
FEATURE [App::DocumentObjectGroupPython] C_element060  label="C_element : 033"  # scripted group (container) (typed FeaturePython)
  n = 1
  ref = C_element
FEATURE [App::DocumentObjectGroupPython] H_element054  label="H_element : 029"  # scripted group (container) (typed FeaturePython)
  n = 4
  ref = H_element
FEATURE [App::DocumentObjectGroupPython] O_element062  label="O_element : 033"  # scripted group (container) (typed FeaturePython)
  n = 1
  ref = O_element
FEATURE [App::DocumentObjectGroupPython] G4_METHANOL  # scripted group (container) (typed FeaturePython)
  Dunit = g/cm3
  Dvalue = 0.7914
  Group = -> [C_element060,H_element054,O_element062]
  conduct = 2
  density = 1
  expand = 3
  formula = G4_METHANOL
  name = G4_METHANOL
  specific = 4
FEATURE [App::DocumentObjectGroupPython] H_element055  label="H_element : 0.134"  # scripted group (container) (typed FeaturePython)
  n = 0.13404
FEATURE [App::DocumentObjectGroupPython] C_element061  label="C_element : 0.778"  # scripted group (container) (typed FeaturePython)
  n = 0.77796
FEATURE [App::DocumentObjectGroupPython] O_element063  label="O_element : 0.035"  # scripted group (container) (typed FeaturePython)
  n = 0.03502
FEATURE [App::DocumentObjectGroupPython] Mg_element009  label="Mg_element : 0.039"  # scripted group (container) (typed FeaturePython)
  n = 0.038594
FEATURE [App::DocumentObjectGroupPython] Ti_element002  label="Ti_element : 0.014"  # scripted group (container) (typed FeaturePython)
  n = 0.014386
FEATURE [App::DocumentObjectGroupPython] G4_MIX_D_WAX  # scripted group (container) (typed FeaturePython)
  Dunit = g/cm3
  Dvalue = 0.99
  Group = -> [H_element055,C_element061,O_element063,Mg_element009,Ti_element002]
  conduct = 2
  density = 1
  expand = 3
  formula = G4_MIX_D_WAX
  name = G4_MIX_D_WAX
  specific = 4
FEATURE [App::DocumentObjectGroupPython] H_element056  label="H_element : 0.135"  # scripted group (container) (typed FeaturePython)
  n = 0.081192
FEATURE [App::DocumentObjectGroupPython] C_element062  label="C_element : 0.583"  # scripted group (container) (typed FeaturePython)
  n = 0.583442
FEATURE [App::DocumentObjectGroupPython] N_element024  label="N_element : 0.018"  # scripted group (container) (typed FeaturePython)
  n = 0.017798
FEATURE [App::DocumentObjectGroupPython] O_element064  label="O_element : 0.186"  # scripted group (container) (typed FeaturePython)
  n = 0.186381
FEATURE [App::DocumentObjectGroupPython] Mg_element010  label="Mg_element : 0.130"  # scripted group (container) (typed FeaturePython)
  n = 0.130287
FEATURE [App::DocumentObjectGroupPython] Cl_element015  label="Cl_element : 0.588"  # scripted group (container) (typed FeaturePython)
  n = 0.0009
FEATURE [App::DocumentObjectGroupPython] G4_MS20_TISSUE  # scripted group (container) (typed FeaturePython)
  Dunit = g/cm3
  Dvalue = 1
  Group = -> [H_element056,C_element062,N_element024,O_element064,Mg_element010,Cl_element015]
  conduct = 2
  density = 1
  expand = 3
  formula = G4_MS20_TISSUE
  name = G4_MS20_TISSUE
  specific = 4
FEATURE [App::DocumentObjectGroupPython] H_element057  label="H_element : 0.136"  # scripted group (container) (typed FeaturePython)
  n = 0.102
FEATURE [App::DocumentObjectGroupPython] C_element063  label="C_element : 0.143"  # scripted group (container) (typed FeaturePython)
  n = 0.143
FEATURE [App::DocumentObjectGroupPython] N_element025  label="N_element : 0.034"  # scripted group (container) (typed FeaturePython)
  n = 0.034
FEATURE [App::DocumentObjectGroupPython] O_element065  label="O_element : 0.710"  # scripted group (container) (typed FeaturePython)
  n = 0.71
FEATURE [App::DocumentObjectGroupPython] Na_element011  label="Na_element : 0.098"  # scripted group (container) (typed FeaturePython)
  n = 0.001
FEATURE [App::DocumentObjectGroupPython] P_element007  label="P_element : 0.002"  # scripted group (container) (typed FeaturePython)
  n = 0.002
FEATURE [App::DocumentObjectGroupPython] S_element017  label="S_element : 0.018"  # scripted group (container) (typed FeaturePython)
  n = 0.003
FEATURE [App::DocumentObjectGroupPython] Cl_element016  label="Cl_element : 0.589"  # scripted group (container) (typed FeaturePython)
  n = 0.001
FEATURE [App::DocumentObjectGroupPython] K_element006  label="K_element : 0.004"  # scripted group (container) (typed FeaturePython)
  n = 0.004
FEATURE [App::DocumentObjectGroupPython] G4_MUSCLE_SKELETAL_ICRP  # scripted group (container) (typed FeaturePython)
  Dunit = g/cm3
  Dvalue = 1.05
  Group = -> [H_element057,C_element063,N_element025,O_element065,Na_element011,P_element007,S_element017,Cl_element016,K_element006]
  conduct = 2
  density = 1
  expand = 3
  formula = G4_MUSCLE_SKELETAL_ICRP
  name = G4_MUSCLE_SKELETAL_ICRP
  specific = 4
FEATURE [App::DocumentObjectGroupPython] H_element058  label="H_element : 0.137"  # scripted group (container) (typed FeaturePython)
  n = 0.102102
FEATURE [App::DocumentObjectGroupPython] C_element064  label="C_element : 0.123"  # scripted group (container) (typed FeaturePython)
  n = 0.123123
FEATURE [App::DocumentObjectGroupPython] N_element026  label="N_element : 0.756"  # scripted group (container) (typed FeaturePython)
  n = 0.035035
FEATURE [App::DocumentObjectGroupPython] O_element066  label="O_element : 0.730"  # scripted group (container) (typed FeaturePython)
  n = 0.72973
FEATURE [App::DocumentObjectGroupPython] Na_element012  label="Na_element : 0.099"  # scripted group (container) (typed FeaturePython)
  n = 0.001001
FEATURE [App::DocumentObjectGroupPython] P_element008  label="P_element : 0.106"  # scripted group (container) (typed FeaturePython)
  n = 0.002002
FEATURE [App::DocumentObjectGroupPython] S_element018  label="S_element : 0.019"  # scripted group (container) (typed FeaturePython)
  n = 0.004004
FEATURE [App::DocumentObjectGroupPython] K_element007  label="K_element : 0.016"  # scripted group (container) (typed FeaturePython)
  n = 0.003003
FEATURE [App::DocumentObjectGroupPython] G4_MUSCLE_STRIATED_ICRU  # scripted group (container) (typed FeaturePython)
  Dunit = g/cm3
  Dvalue = 1.04
  Group = -> [H_element058,C_element064,N_element026,O_element066,Na_element012,P_element008,S_element018,K_element007]
  conduct = 2
  density = 1
  expand = 3
  formula = G4_MUSCLE_STRIATED_ICRU
  name = G4_MUSCLE_STRIATED_ICRU
  specific = 4
FEATURE [App::DocumentObjectGroupPython] H_element059  label="H_element : 0.098"  # scripted group (container) (typed FeaturePython)
  n = 0.0982341
FEATURE [App::DocumentObjectGroupPython] C_element065  label="C_element : 0.156"  # scripted group (container) (typed FeaturePython)
  n = 0.156214
FEATURE [App::DocumentObjectGroupPython] N_element027  label="N_element : 0.757"  # scripted group (container) (typed FeaturePython)
  n = 0.035451
FEATURE [App::DocumentObjectGroupPython] O_element067  label="O_element : 0.880"  # scripted group (container) (typed FeaturePython)
  n = 0.710101
FEATURE [App::DocumentObjectGroupPython] G4_MUSCLE_WITH_SUCROSE  # scripted group (container) (typed FeaturePython)
  Dunit = g/cm3
  Dvalue = 1.11
  Group = -> [H_element059,C_element065,N_element027,O_element067]
  conduct = 2
  density = 1
  expand = 3
  formula = G4_MUSCLE_WITH_SUCROSE
  name = G4_MUSCLE_WITH_SUCROSE
  specific = 4
FEATURE [App::DocumentObjectGroupPython] H_element060  label="H_element : 0.138"  # scripted group (container) (typed FeaturePython)
  n = 0.101969
FEATURE [App::DocumentObjectGroupPython] C_element066  label="C_element : 0.120"  # scripted group (container) (typed FeaturePython)
  n = 0.120058
FEATURE [App::DocumentObjectGroupPython] N_element028  label="N_element : 0.758"  # scripted group (container) (typed FeaturePython)
  n = 0.035451
FEATURE [App::DocumentObjectGroupPython] O_element068  label="O_element : 0.743"  # scripted group (container) (typed FeaturePython)
  n = 0.742522
FEATURE [App::DocumentObjectGroupPython] G4_MUSCLE_WITHOUT_SUCROSE  # scripted group (container) (typed FeaturePython)
  Dunit = g/cm3
  Dvalue = 1.07
  Group = -> [H_element060,C_element066,N_element028,O_element068]
  conduct = 2
  density = 1
  expand = 3
  formula = G4_MUSCLE_WITHOUT_SUCROSE
  name = G4_MUSCLE_WITHOUT_SUCROSE
  specific = 4
FEATURE [App::DocumentObjectGroupPython] C_element067  label="C_element : 10"  # scripted group (container) (typed FeaturePython)
  n = 10
  ref = C_element
FEATURE [App::DocumentObjectGroupPython] H_element061  label="H_element : 030"  # scripted group (container) (typed FeaturePython)
  n = 8
  ref = H_element
FEATURE [App::DocumentObjectGroupPython] G4_NAPHTHALENE  # scripted group (container) (typed FeaturePython)
  Dunit = g/cm3
  Dvalue = 1.145
  Group = -> [C_element067,H_element061]
  conduct = 2
  density = 1
  expand = 3
  formula = G4_NAPHTHALENE
  name = G4_NAPHTHALENE
  specific = 4
FEATURE [App::DocumentObjectGroupPython] C_element068  label="C_element : 034"  # scripted group (container) (typed FeaturePython)
  n = 6
  ref = C_element
FEATURE [App::DocumentObjectGroupPython] H_element062  label="H_element : 031"  # scripted group (container) (typed FeaturePython)
  n = 5
  ref = H_element
FEATURE [App::DocumentObjectGroupPython] N_element029  label="N_element : 012"  # scripted group (container) (typed FeaturePython)
  n = 1
  ref = N_element
FEATURE [App::DocumentObjectGroupPython] O_element069  label="O_element : 034"  # scripted group (container) (typed FeaturePython)
  n = 2
  ref = O_element
FEATURE [App::DocumentObjectGroupPython] G4_NITROBENZENE  # scripted group (container) (typed FeaturePython)
  Dunit = g/cm3
  Dvalue = 1.19867
  Group = -> [C_element068,H_element062,N_element029,O_element069]
  conduct = 2
  density = 1
  expand = 3
  formula = G4_NITROBENZENE
  name = G4_NITROBENZENE
  specific = 4
FEATURE [App::DocumentObjectGroupPython] N_element030  label="N_element : 013"  # scripted group (container) (typed FeaturePython)
  n = 2
  ref = N_element
FEATURE [App::DocumentObjectGroupPython] O_element070  label="O_element : 035"  # scripted group (container) (typed FeaturePython)
  n = 1
  ref = O_element
FEATURE [App::DocumentObjectGroupPython] G4_NITROUS_OXIDE  # scripted group (container) (typed FeaturePython)
  Dunit = g/cm3
  Dvalue = 0.00183094
  Group = -> [N_element030,O_element070]
  conduct = 2
  density = 1
  expand = 3
  formula = G4_NITROUS_OXIDE
  name = G4_NITROUS_OXIDE
  specific = 4
FEATURE [App::DocumentObjectGroupPython] H_element063  label="H_element : 0.104"  # scripted group (container) (typed FeaturePython)
  n = 0.103509
FEATURE [App::DocumentObjectGroupPython] C_element069  label="C_element : 0.648"  # scripted group (container) (typed FeaturePython)
  n = 0.648416
FEATURE [App::DocumentObjectGroupPython] N_element031  label="N_element : 0.100"  # scripted group (container) (typed FeaturePython)
  n = 0.0995361
FEATURE [App::DocumentObjectGroupPython] O_element071  label="O_element : 0.149"  # scripted group (container) (typed FeaturePython)
  n = 0.148539
FEATURE [App::DocumentObjectGroupPython] G4_NYLON_8062  label="G4_NYLON-8062"  # scripted group (container) (typed FeaturePython)
  Dunit = g/cm3
  Dvalue = 1.08
  Group = -> [H_element063,C_element069,N_element031,O_element071]
  conduct = 2
  density = 1
  expand = 3
  formula = G4_NYLON-8062
  name = G4_NYLON-8062
  specific = 4
FEATURE [App::DocumentObjectGroupPython] C_element070  label="C_element : 035"  # scripted group (container) (typed FeaturePython)
  n = 6
  ref = C_element
FEATURE [App::DocumentObjectGroupPython] H_element064  label="H_element : 11"  # scripted group (container) (typed FeaturePython)
  n = 11
  ref = H_element
FEATURE [App::DocumentObjectGroupPython] N_element032  label="N_element : 014"  # scripted group (container) (typed FeaturePython)
  n = 1
  ref = N_element
FEATURE [App::DocumentObjectGroupPython] O_element072  label="O_element : 036"  # scripted group (container) (typed FeaturePython)
  n = 1
  ref = O_element
FEATURE [App::DocumentObjectGroupPython] G4_NYLON_6_6  label="G4_NYLON-6-6"  # scripted group (container) (typed FeaturePython)
  Dunit = g/cm3
  Dvalue = 1.14
  Group = -> [C_element070,H_element064,N_element032,O_element072]
  conduct = 2
  density = 1
  expand = 3
  formula = G4_NYLON-6-6
  name = G4_NYLON-6-6
  specific = 4
FEATURE [App::DocumentObjectGroupPython] H_element065  label="H_element : 0.139"  # scripted group (container) (typed FeaturePython)
  n = 0.107062
FEATURE [App::DocumentObjectGroupPython] C_element071  label="C_element : 0.680"  # scripted group (container) (typed FeaturePython)
  n = 0.680449
FEATURE [App::DocumentObjectGroupPython] N_element033  label="N_element : 0.099"  # scripted group (container) (typed FeaturePython)
  n = 0.099189
FEATURE [App::DocumentObjectGroupPython] O_element073  label="O_element : 0.113"  # scripted group (container) (typed FeaturePython)
  n = 0.1133
FEATURE [App::DocumentObjectGroupPython] G4_NYLON_6_10  label="G4_NYLON-6-10"  # scripted group (container) (typed FeaturePython)
  Dunit = g/cm3
  Dvalue = 1.14
  Group = -> [H_element065,C_element071,N_element033,O_element073]
  conduct = 2
  density = 1
  expand = 3
  formula = G4_NYLON-6-10
  name = G4_NYLON-6-10
  specific = 4
FEATURE [App::DocumentObjectGroupPython] H_element066  label="H_element : 0.140"  # scripted group (container) (typed FeaturePython)
  n = 0.115476
FEATURE [App::DocumentObjectGroupPython] C_element072  label="C_element : 0.721"  # scripted group (container) (typed FeaturePython)
  n = 0.720818
FEATURE [App::DocumentObjectGroupPython] N_element034  label="N_element : 0.076"  # scripted group (container) (typed FeaturePython)
  n = 0.0764169
FEATURE [App::DocumentObjectGroupPython] O_element074  label="O_element : 0.087"  # scripted group (container) (typed FeaturePython)
  n = 0.0872889
FEATURE [App::DocumentObjectGroupPython] G4_NYLON_11_RILSAN  label="G4_NYLON-11_RILSAN"  # scripted group (container) (typed FeaturePython)
  Dunit = g/cm3
  Dvalue = 1.425
  Group = -> [H_element066,C_element072,N_element034,O_element074]
  conduct = 2
  density = 1
  expand = 3
  formula = G4_NYLON-11_RILSAN
  name = G4_NYLON-11_RILSAN
  specific = 4
FEATURE [App::DocumentObjectGroupPython] C_element073  label="C_element : 8"  # scripted group (container) (typed FeaturePython)
  n = 8
  ref = C_element
FEATURE [App::DocumentObjectGroupPython] H_element067  label="H_element : 18"  # scripted group (container) (typed FeaturePython)
  n = 18
  ref = H_element
FEATURE [App::DocumentObjectGroupPython] G4_OCTANE  # scripted group (container) (typed FeaturePython)
  Dunit = g/cm3
  Dvalue = 0.7026
  Group = -> [C_element073,H_element067]
  conduct = 2
  density = 1
  expand = 3
  formula = G4_OCTANE
  name = G4_OCTANE
  specific = 4
FEATURE [App::DocumentObjectGroupPython] C_element074  label="C_element : 25"  # scripted group (container) (typed FeaturePython)
  n = 25
  ref = C_element
FEATURE [App::DocumentObjectGroupPython] H_element068  label="H_element : 52"  # scripted group (container) (typed FeaturePython)
  n = 52
  ref = H_element
FEATURE [App::DocumentObjectGroupPython] G4_PARAFFIN  # scripted group (container) (typed FeaturePython)
  Dunit = g/cm3
  Dvalue = 0.93
  Group = -> [C_element074,H_element068]
  conduct = 2
  density = 1
  expand = 3
  formula = G4_PARAFFIN
  name = G4_PARAFFIN
  specific = 4
FEATURE [App::DocumentObjectGroupPython] C_element075  label="C_element : 036"  # scripted group (container) (typed FeaturePython)
  n = 5
  ref = C_element
FEATURE [App::DocumentObjectGroupPython] H_element069  label="H_element : 032"  # scripted group (container) (typed FeaturePython)
  n = 12
  ref = H_element
FEATURE [App::DocumentObjectGroupPython] G4_N_PENTANE  label="G4_N-PENTANE"  # scripted group (container) (typed FeaturePython)
  Dunit = g/cm3
  Dvalue = 0.6262
  Group = -> [C_element075,H_element069]
  conduct = 2
  density = 1
  expand = 3
  formula = G4_N-PENTANE
  name = G4_N-PENTANE
  specific = 4
FEATURE [App::DocumentObjectGroupPython] H_element070  label="H_element : 0.014"  # scripted group (container) (typed FeaturePython)
  n = 0.0141
FEATURE [App::DocumentObjectGroupPython] C_element076  label="C_element : 0.072"  # scripted group (container) (typed FeaturePython)
  n = 0.072261
FEATURE [App::DocumentObjectGroupPython] N_element035  label="N_element : 0.019"  # scripted group (container) (typed FeaturePython)
  n = 0.01932
FEATURE [App::DocumentObjectGroupPython] O_element075  label="O_element : 0.066"  # scripted group (container) (typed FeaturePython)
  n = 0.066101
FEATURE [App::DocumentObjectGroupPython] S_element019  label="S_element : 0.020"  # scripted group (container) (typed FeaturePython)
  n = 0.00189
FEATURE [App::DocumentObjectGroupPython] Br_element004  label="Br_element : 0.349"  # scripted group (container) (typed FeaturePython)
  n = 0.349103
FEATURE [App::DocumentObjectGroupPython] Ag_element001  label="Ag_element : 0.474"  # scripted group (container) (typed FeaturePython)
  n = 0.474105
FEATURE [App::DocumentObjectGroupPython] I_element005  label="I_element : 0.003"  # scripted group (container) (typed FeaturePython)
  n = 0.00312
FEATURE [App::DocumentObjectGroupPython] G4_PHOTO_EMULSION  # scripted group (container) (typed FeaturePython)
  Dunit = g/cm3
  Dvalue = 3.815
  Group = -> [H_element070,C_element076,N_element035,O_element075,S_element019,Br_element004,Ag_element001,I_element005]
  conduct = 2
  density = 1
  expand = 3
  formula = G4_PHOTO_EMULSION
  name = G4_PHOTO_EMULSION
  specific = 4
FEATURE [App::DocumentObjectGroupPython] C_element077  label="C_element : 9"  # scripted group (container) (typed FeaturePython)
  n = 9
  ref = C_element
FEATURE [App::DocumentObjectGroupPython] H_element071  label="H_element : 033"  # scripted group (container) (typed FeaturePython)
  n = 10
  ref = H_element
FEATURE [App::DocumentObjectGroupPython] G4_PLASTIC_SC_VINYLTOLUENE  # scripted group (container) (typed FeaturePython)
  Dunit = g/cm3
  Dvalue = 1.032
  Group = -> [C_element077,H_element071]
  conduct = 2
  density = 1
  expand = 3
  formula = G4_PLASTIC_SC_VINYLTOLUENE
  name = G4_PLASTIC_SC_VINYLTOLUENE
  specific = 4
FEATURE [App::DocumentObjectGroupPython] Pu_element001  label="Pu_element : 1"  # scripted group (container) (typed FeaturePython)
  n = 1
  ref = Pu_element
FEATURE [App::DocumentObjectGroupPython] O_element076  label="O_element : 037"  # scripted group (container) (typed FeaturePython)
  n = 2
  ref = O_element
FEATURE [App::DocumentObjectGroupPython] G4_PLUTONIUM_DIOXIDE  # scripted group (container) (typed FeaturePython)
  Dunit = g/cm3
  Dvalue = 11.46
  Group = -> [Pu_element001,O_element076]
  conduct = 2
  density = 1
  expand = 3
  formula = G4_PLUTONIUM_DIOXIDE
  name = G4_PLUTONIUM_DIOXIDE
  specific = 4
FEATURE [App::DocumentObjectGroupPython] C_element078  label="C_element : 037"  # scripted group (container) (typed FeaturePython)
  n = 3
  ref = C_element
FEATURE [App::DocumentObjectGroupPython] H_element072  label="H_element : 034"  # scripted group (container) (typed FeaturePython)
  n = 3
  ref = H_element
FEATURE [App::DocumentObjectGroupPython] N_element036  label="N_element : 015"  # scripted group (container) (typed FeaturePython)
  n = 1
  ref = N_element
FEATURE [App::DocumentObjectGroupPython] G4_POLYACRYLONITRILE  # scripted group (container) (typed FeaturePython)
  Dunit = g/cm3
  Dvalue = 1.17
  Group = -> [C_element078,H_element072,N_element036]
  conduct = 2
  density = 1
  expand = 3
  formula = G4_POLYACRYLONITRILE
  name = G4_POLYACRYLONITRILE
  specific = 4
FEATURE [App::DocumentObjectGroupPython] C_element079  label="C_element : 16"  # scripted group (container) (typed FeaturePython)
  n = 16
  ref = C_element
FEATURE [App::DocumentObjectGroupPython] H_element073  label="H_element : 035"  # scripted group (container) (typed FeaturePython)
  n = 14
  ref = H_element
FEATURE [App::DocumentObjectGroupPython] O_element077  label="O_element : 038"  # scripted group (container) (typed FeaturePython)
  n = 3
  ref = O_element
FEATURE [App::DocumentObjectGroupPython] G4_POLYCARBONATE  # scripted group (container) (typed FeaturePython)
  Dunit = g/cm3
  Dvalue = 1.2
  Group = -> [C_element079,H_element073,O_element077]
  conduct = 2
  density = 1
  expand = 3
  formula = G4_POLYCARBONATE
  name = G4_POLYCARBONATE
  specific = 4
FEATURE [App::DocumentObjectGroupPython] C_element080  label="C_element : 038"  # scripted group (container) (typed FeaturePython)
  n = 8
  ref = C_element
FEATURE [App::DocumentObjectGroupPython] H_element074  label="H_element : 036"  # scripted group (container) (typed FeaturePython)
  n = 7
  ref = H_element
FEATURE [App::DocumentObjectGroupPython] Cl_element017  label="Cl_element : 007"  # scripted group (container) (typed FeaturePython)
  n = 1
  ref = Cl_element
FEATURE [App::DocumentObjectGroupPython] G4_POLYCHLOROSTYRENE  # scripted group (container) (typed FeaturePython)
  Dunit = g/cm3
  Dvalue = 1.3
  Group = -> [C_element080,H_element074,Cl_element017]
  conduct = 2
  density = 1
  expand = 3
  formula = G4_POLYCHLOROSTYRENE
  name = G4_POLYCHLOROSTYRENE
  specific = 4
FEATURE [App::DocumentObjectGroupPython] C_element081  label="C_element : 039"  # scripted group (container) (typed FeaturePython)
  n = 1
  ref = C_element
FEATURE [App::DocumentObjectGroupPython] H_element075  label="H_element : 037"  # scripted group (container) (typed FeaturePython)
  n = 2
  ref = H_element
FEATURE [App::DocumentObjectGroupPython] G4_POLYETHYLENE  # scripted group (container) (typed FeaturePython)
  Dunit = g/cm3
  Dvalue = 0.94
  Group = -> [C_element081,H_element075]
  conduct = 2
  density = 1
  expand = 3
  formula = G4_POLYETHYLENE
  name = G4_POLYETHYLENE
  specific = 4
FEATURE [App::DocumentObjectGroupPython] C_element082  label="C_element : 040"  # scripted group (container) (typed FeaturePython)
  n = 10
  ref = C_element
FEATURE [App::DocumentObjectGroupPython] H_element076  label="H_element : 038"  # scripted group (container) (typed FeaturePython)
  n = 8
  ref = H_element
FEATURE [App::DocumentObjectGroupPython] O_element078  label="O_element : 039"  # scripted group (container) (typed FeaturePython)
  n = 4
  ref = O_element
FEATURE [App::DocumentObjectGroupPython] G4_MYLAR  # scripted group (container) (typed FeaturePython)
  Dunit = g/cm3
  Dvalue = 1.4
  Group = -> [C_element082,H_element076,O_element078]
  conduct = 2
  density = 1
  expand = 3
  formula = G4_MYLAR
  name = G4_MYLAR
  specific = 4
FEATURE [App::DocumentObjectGroupPython] C_element083  label="C_element : 041"  # scripted group (container) (typed FeaturePython)
  n = 5
  ref = C_element
FEATURE [App::DocumentObjectGroupPython] H_element077  label="H_element : 039"  # scripted group (container) (typed FeaturePython)
  n = 8
  ref = H_element
FEATURE [App::DocumentObjectGroupPython] O_element079  label="O_element : 040"  # scripted group (container) (typed FeaturePython)
  n = 2
  ref = O_element
FEATURE [App::DocumentObjectGroupPython] G4_PLEXIGLASS  # scripted group (container) (typed FeaturePython)
  Dunit = g/cm3
  Dvalue = 1.19
  Group = -> [C_element083,H_element077,O_element079]
  conduct = 2
  density = 1
  expand = 3
  formula = G4_PLEXIGLASS
  name = G4_PLEXIGLASS
  specific = 4
FEATURE [App::DocumentObjectGroupPython] C_element084  label="C_element : 042"  # scripted group (container) (typed FeaturePython)
  n = 1
  ref = C_element
FEATURE [App::DocumentObjectGroupPython] H_element078  label="H_element : 040"  # scripted group (container) (typed FeaturePython)
  n = 2
  ref = H_element
FEATURE [App::DocumentObjectGroupPython] O_element080  label="O_element : 041"  # scripted group (container) (typed FeaturePython)
  n = 1
  ref = O_element
FEATURE [App::DocumentObjectGroupPython] G4_POLYOXYMETHYLENE  # scripted group (container) (typed FeaturePython)
  Dunit = g/cm3
  Dvalue = 1.425
  Group = -> [C_element084,H_element078,O_element080]
  conduct = 2
  density = 1
  expand = 3
  formula = G4_POLYOXYMETHYLENE
  name = G4_POLYOXYMETHYLENE
  specific = 4
FEATURE [App::DocumentObjectGroupPython] C_element085  label="C_element : 043"  # scripted group (container) (typed FeaturePython)
  n = 2
  ref = C_element
FEATURE [App::DocumentObjectGroupPython] H_element079  label="H_element : 041"  # scripted group (container) (typed FeaturePython)
  n = 4
  ref = H_element
FEATURE [App::DocumentObjectGroupPython] G4_POLYPROPYLENE  # scripted group (container) (typed FeaturePython)
  Dunit = g/cm3
  Dvalue = 0.9
  Group = -> [C_element085,H_element079]
  conduct = 2
  density = 1
  expand = 3
  formula = G4_POLYPROPYLENE
  name = G4_POLYPROPYLENE
  specific = 4
FEATURE [App::DocumentObjectGroupPython] C_element086  label="C_element : 044"  # scripted group (container) (typed FeaturePython)
  n = 8
  ref = C_element
FEATURE [App::DocumentObjectGroupPython] H_element080  label="H_element : 042"  # scripted group (container) (typed FeaturePython)
  n = 8
  ref = H_element
FEATURE [App::DocumentObjectGroupPython] G4_POLYSTYRENE  # scripted group (container) (typed FeaturePython)
  Dunit = g/cm3
  Dvalue = 1.06
  Group = -> [C_element086,H_element080]
  conduct = 2
  density = 1
  expand = 3
  formula = G4_POLYSTYRENE
  name = G4_POLYSTYRENE
  specific = 4
FEATURE [App::DocumentObjectGroupPython] C_element087  label="C_element : 045"  # scripted group (container) (typed FeaturePython)
  n = 2
  ref = C_element
FEATURE [App::DocumentObjectGroupPython] F_element014  label="F_element : 4"  # scripted group (container) (typed FeaturePython)
  n = 4
  ref = F_element
FEATURE [App::DocumentObjectGroupPython] G4_TEFLON  # scripted group (container) (typed FeaturePython)
  Dunit = g/cm3
  Dvalue = 2.2
  Group = -> [C_element087,F_element014]
  conduct = 2
  density = 1
  expand = 3
  formula = G4_TEFLON
  name = G4_TEFLON
  specific = 4
FEATURE [App::DocumentObjectGroupPython] C_element088  label="C_element : 046"  # scripted group (container) (typed FeaturePython)
  n = 2
  ref = C_element
FEATURE [App::DocumentObjectGroupPython] F_element015  label="F_element : 006"  # scripted group (container) (typed FeaturePython)
  n = 3
  ref = F_element
FEATURE [App::DocumentObjectGroupPython] Cl_element018  label="Cl_element : 008"  # scripted group (container) (typed FeaturePython)
  n = 1
  ref = Cl_element
FEATURE [App::DocumentObjectGroupPython] G4_POLYTRIFLUOROCHLOROETHYLENE  # scripted group (container) (typed FeaturePython)
  Dunit = g/cm3
  Dvalue = 2.1
  Group = -> [C_element088,F_element015,Cl_element018]
  conduct = 2
  density = 1
  expand = 3
  formula = G4_POLYTRIFLUOROCHLOROETHYLENE
  name = G4_POLYTRIFLUOROCHLOROETHYLENE
  specific = 4
FEATURE [App::DocumentObjectGroupPython] C_element089  label="C_element : 047"  # scripted group (container) (typed FeaturePython)
  n = 4
  ref = C_element
FEATURE [App::DocumentObjectGroupPython] H_element081  label="H_element : 043"  # scripted group (container) (typed FeaturePython)
  n = 6
  ref = H_element
FEATURE [App::DocumentObjectGroupPython] O_element081  label="O_element : 042"  # scripted group (container) (typed FeaturePython)
  n = 2
  ref = O_element
FEATURE [App::DocumentObjectGroupPython] G4_POLYVINYL_ACETATE  # scripted group (container) (typed FeaturePython)
  Dunit = g/cm3
  Dvalue = 1.19
  Group = -> [C_element089,H_element081,O_element081]
  conduct = 2
  density = 1
  expand = 3
  formula = G4_POLYVINYL_ACETATE
  name = G4_POLYVINYL_ACETATE
  specific = 4
FEATURE [App::DocumentObjectGroupPython] C_element090  label="C_element : 048"  # scripted group (container) (typed FeaturePython)
  n = 2
  ref = C_element
FEATURE [App::DocumentObjectGroupPython] H_element082  label="H_element : 044"  # scripted group (container) (typed FeaturePython)
  n = 4
  ref = H_element
FEATURE [App::DocumentObjectGroupPython] O_element082  label="O_element : 043"  # scripted group (container) (typed FeaturePython)
  n = 1
  ref = O_element
FEATURE [App::DocumentObjectGroupPython] G4_POLYVINYL_ALCOHOL  # scripted group (container) (typed FeaturePython)
  Dunit = g/cm3
  Dvalue = 1.3
  Group = -> [C_element090,H_element082,O_element082]
  conduct = 2
  density = 1
  expand = 3
  formula = G4_POLYVINYL_ALCOHOL
  name = G4_POLYVINYL_ALCOHOL
  specific = 4
FEATURE [App::DocumentObjectGroupPython] C_element091  label="C_element : 049"  # scripted group (container) (typed FeaturePython)
  n = 8
  ref = C_element
FEATURE [App::DocumentObjectGroupPython] H_element083  label="H_element : 045"  # scripted group (container) (typed FeaturePython)
  n = 14
  ref = H_element
FEATURE [App::DocumentObjectGroupPython] O_element083  label="O_element : 044"  # scripted group (container) (typed FeaturePython)
  n = 2
  ref = O_element
FEATURE [App::DocumentObjectGroupPython] G4_POLYVINYL_BUTYRAL  # scripted group (container) (typed FeaturePython)
  Dunit = g/cm3
  Dvalue = 1.12
  Group = -> [C_element091,H_element083,O_element083]
  conduct = 2
  density = 1
  expand = 3
  formula = G4_POLYVINYL_BUTYRAL
  name = G4_POLYVINYL_BUTYRAL
  specific = 4
FEATURE [App::DocumentObjectGroupPython] C_element092  label="C_element : 050"  # scripted group (container) (typed FeaturePython)
  n = 2
  ref = C_element
FEATURE [App::DocumentObjectGroupPython] H_element084  label="H_element : 046"  # scripted group (container) (typed FeaturePython)
  n = 3
  ref = H_element
FEATURE [App::DocumentObjectGroupPython] Cl_element019  label="Cl_element : 009"  # scripted group (container) (typed FeaturePython)
  n = 1
  ref = Cl_element
FEATURE [App::DocumentObjectGroupPython] G4_POLYVINYL_CHLORIDE  # scripted group (container) (typed FeaturePython)
  Dunit = g/cm3
  Dvalue = 1.3
  Group = -> [C_element092,H_element084,Cl_element019]
  conduct = 2
  density = 1
  expand = 3
  formula = G4_POLYVINYL_CHLORIDE
  name = G4_POLYVINYL_CHLORIDE
  specific = 4
FEATURE [App::DocumentObjectGroupPython] C_element093  label="C_element : 051"  # scripted group (container) (typed FeaturePython)
  n = 2
  ref = C_element
FEATURE [App::DocumentObjectGroupPython] H_element085  label="H_element : 047"  # scripted group (container) (typed FeaturePython)
  n = 2
  ref = H_element
FEATURE [App::DocumentObjectGroupPython] Cl_element020  label="Cl_element : 010"  # scripted group (container) (typed FeaturePython)
  n = 2
  ref = Cl_element
FEATURE [App::DocumentObjectGroupPython] G4_POLYVINYLIDENE_CHLORIDE  # scripted group (container) (typed FeaturePython)
  Dunit = g/cm3
  Dvalue = 1.7
  Group = -> [C_element093,H_element085,Cl_element020]
  conduct = 2
  density = 1
  expand = 3
  formula = G4_POLYVINYLIDENE_CHLORIDE
  name = G4_POLYVINYLIDENE_CHLORIDE
  specific = 4
FEATURE [App::DocumentObjectGroupPython] C_element094  label="C_element : 052"  # scripted group (container) (typed FeaturePython)
  n = 2
  ref = C_element
FEATURE [App::DocumentObjectGroupPython] H_element086  label="H_element : 048"  # scripted group (container) (typed FeaturePython)
  n = 2
  ref = H_element
FEATURE [App::DocumentObjectGroupPython] F_element016  label="F_element : 007"  # scripted group (container) (typed FeaturePython)
  n = 2
  ref = F_element
FEATURE [App::DocumentObjectGroupPython] G4_POLYVINYLIDENE_FLUORIDE  # scripted group (container) (typed FeaturePython)
  Dunit = g/cm3
  Dvalue = 1.76
  Group = -> [C_element094,H_element086,F_element016]
  conduct = 2
  density = 1
  expand = 3
  formula = G4_POLYVINYLIDENE_FLUORIDE
  name = G4_POLYVINYLIDENE_FLUORIDE
  specific = 4
FEATURE [App::DocumentObjectGroupPython] C_element095  label="C_element : 053"  # scripted group (container) (typed FeaturePython)
  n = 6
  ref = C_element
FEATURE [App::DocumentObjectGroupPython] H_element087  label="H_element : 9"  # scripted group (container) (typed FeaturePython)
  n = 9
  ref = H_element
FEATURE [App::DocumentObjectGroupPython] N_element037  label="N_element : 016"  # scripted group (container) (typed FeaturePython)
  n = 1
  ref = N_element
FEATURE [App::DocumentObjectGroupPython] O_element084  label="O_element : 045"  # scripted group (container) (typed FeaturePython)
  n = 1
  ref = O_element
FEATURE [App::DocumentObjectGroupPython] G4_POLYVINYL_PYRROLIDONE  # scripted group (container) (typed FeaturePython)
  Dunit = g/cm3
  Dvalue = 1.25
  Group = -> [C_element095,H_element087,N_element037,O_element084]
  conduct = 2
  density = 1
  expand = 3
  formula = G4_POLYVINYL_PYRROLIDONE
  name = G4_POLYVINYL_PYRROLIDONE
  specific = 4
FEATURE [App::DocumentObjectGroupPython] K_element008  label="K_element : 1"  # scripted group (container) (typed FeaturePython)
  n = 1
  ref = K_element
FEATURE [App::DocumentObjectGroupPython] I_element006  label="I_element : 003"  # scripted group (container) (typed FeaturePython)
  n = 1
  ref = I_element
FEATURE [App::DocumentObjectGroupPython] G4_POTASSIUM_IODIDE  # scripted group (container) (typed FeaturePython)
  Dunit = g/cm3
  Dvalue = 3.13
  Group = -> [K_element008,I_element006]
  conduct = 2
  density = 1
  expand = 3
  formula = G4_POTASSIUM_IODIDE
  name = G4_POTASSIUM_IODIDE
  specific = 4
FEATURE [App::DocumentObjectGroupPython] K_element009  label="K_element : 2"  # scripted group (container) (typed FeaturePython)
  n = 2
  ref = K_element
FEATURE [App::DocumentObjectGroupPython] O_element085  label="O_element : 046"  # scripted group (container) (typed FeaturePython)
  n = 1
  ref = O_element
FEATURE [App::DocumentObjectGroupPython] G4_POTASSIUM_OXIDE  # scripted group (container) (typed FeaturePython)
  Dunit = g/cm3
  Dvalue = 2.32
  Group = -> [K_element009,O_element085]
  conduct = 2
  density = 1
  expand = 3
  formula = G4_POTASSIUM_OXIDE
  name = G4_POTASSIUM_OXIDE
  specific = 4
FEATURE [App::DocumentObjectGroupPython] C_element096  label="C_element : 054"  # scripted group (container) (typed FeaturePython)
  n = 3
  ref = C_element
FEATURE [App::DocumentObjectGroupPython] H_element088  label="H_element : 049"  # scripted group (container) (typed FeaturePython)
  n = 8
  ref = H_element
FEATURE [App::DocumentObjectGroupPython] G4_PROPANE  # scripted group (container) (typed FeaturePython)
  Dunit = g/cm3
  Dvalue = 0.00187939
  Group = -> [C_element096,H_element088]
  conduct = 2
  density = 1
  expand = 3
  formula = G4_PROPANE
  name = G4_PROPANE
  specific = 4
FEATURE [App::DocumentObjectGroupPython] C_element097  label="C_element : 055"  # scripted group (container) (typed FeaturePython)
  n = 3
  ref = C_element
FEATURE [App::DocumentObjectGroupPython] H_element089  label="H_element : 050"  # scripted group (container) (typed FeaturePython)
  n = 8
  ref = H_element
FEATURE [App::DocumentObjectGroupPython] G4_lPROPANE  # scripted group (container) (typed FeaturePython)
  Dunit = g/cm3
  Dvalue = 0.43
  Group = -> [C_element097,H_element089]
  conduct = 2
  density = 1
  expand = 3
  formula = G4_lPROPANE
  name = G4_lPROPANE
  specific = 4
FEATURE [App::DocumentObjectGroupPython] C_element098  label="C_element : 056"  # scripted group (container) (typed FeaturePython)
  n = 3
  ref = C_element
FEATURE [App::DocumentObjectGroupPython] H_element090  label="H_element : 051"  # scripted group (container) (typed FeaturePython)
  n = 8
  ref = H_element
FEATURE [App::DocumentObjectGroupPython] O_element086  label="O_element : 047"  # scripted group (container) (typed FeaturePython)
  n = 1
  ref = O_element
FEATURE [App::DocumentObjectGroupPython] G4_N_PROPYL_ALCOHOL  label="G4_N-PROPYL_ALCOHOL"  # scripted group (container) (typed FeaturePython)
  Dunit = g/cm3
  Dvalue = 0.8035
  Group = -> [C_element098,H_element090,O_element086]
  conduct = 2
  density = 1
  expand = 3
  formula = G4_N-PROPYL_ALCOHOL
  name = G4_N-PROPYL_ALCOHOL
  specific = 4
FEATURE [App::DocumentObjectGroupPython] C_element099  label="C_element : 057"  # scripted group (container) (typed FeaturePython)
  n = 5
  ref = C_element
FEATURE [App::DocumentObjectGroupPython] H_element091  label="H_element : 052"  # scripted group (container) (typed FeaturePython)
  n = 5
  ref = H_element
FEATURE [App::DocumentObjectGroupPython] N_element038  label="N_element : 017"  # scripted group (container) (typed FeaturePython)
  n = 1
  ref = N_element
FEATURE [App::DocumentObjectGroupPython] G4_PYRIDINE  # scripted group (container) (typed FeaturePython)
  Dunit = g/cm3
  Dvalue = 0.9819
  Group = -> [C_element099,H_element091,N_element038]
  conduct = 2
  density = 1
  expand = 3
  formula = G4_PYRIDINE
  name = G4_PYRIDINE
  specific = 4
FEATURE [App::DocumentObjectGroupPython] H_element092  label="H_element : 0.144"  # scripted group (container) (typed FeaturePython)
  n = 0.143711
FEATURE [App::DocumentObjectGroupPython] C_element100  label="C_element : 0.856"  # scripted group (container) (typed FeaturePython)
  n = 0.856289
FEATURE [App::DocumentObjectGroupPython] G4_RUBBER_BUTYL  # scripted group (container) (typed FeaturePython)
  Dunit = g/cm3
  Dvalue = 0.92
  Group = -> [H_element092,C_element100]
  conduct = 2
  density = 1
  expand = 3
  formula = G4_RUBBER_BUTYL
  name = G4_RUBBER_BUTYL
  specific = 4
FEATURE [App::DocumentObjectGroupPython] H_element093  label="H_element : 0.118"  # scripted group (container) (typed FeaturePython)
  n = 0.118371
FEATURE [App::DocumentObjectGroupPython] C_element101  label="C_element : 0.882"  # scripted group (container) (typed FeaturePython)
  n = 0.881629
FEATURE [App::DocumentObjectGroupPython] G4_RUBBER_NATURAL  # scripted group (container) (typed FeaturePython)
  Dunit = g/cm3
  Dvalue = 0.92
  Group = -> [H_element093,C_element101]
  conduct = 2
  density = 1
  expand = 3
  formula = G4_RUBBER_NATURAL
  name = G4_RUBBER_NATURAL
  specific = 4
FEATURE [App::DocumentObjectGroupPython] H_element094  label="H_element : 0.145"  # scripted group (container) (typed FeaturePython)
  n = 0.05692
FEATURE [App::DocumentObjectGroupPython] C_element102  label="C_element : 0.543"  # scripted group (container) (typed FeaturePython)
  n = 0.542646
FEATURE [App::DocumentObjectGroupPython] Cl_element021  label="Cl_element : 0.400"  # scripted group (container) (typed FeaturePython)
  n = 0.400434
FEATURE [App::DocumentObjectGroupPython] G4_RUBBER_NEOPRENE  # scripted group (container) (typed FeaturePython)
  Dunit = g/cm3
  Dvalue = 1.23
  Group = -> [H_element094,C_element102,Cl_element021]
  conduct = 2
  density = 1
  expand = 3
  formula = G4_RUBBER_NEOPRENE
  name = G4_RUBBER_NEOPRENE
  specific = 4
FEATURE [App::DocumentObjectGroupPython] Si_element006  label="Si_element : 1"  # scripted group (container) (typed FeaturePython)
  n = 1
  ref = Si_element
FEATURE [App::DocumentObjectGroupPython] O_element087  label="O_element : 048"  # scripted group (container) (typed FeaturePython)
  n = 2
  ref = O_element
FEATURE [App::DocumentObjectGroupPython] G4_SILICON_DIOXIDE  # scripted group (container) (typed FeaturePython)
  Dunit = g/cm3
  Dvalue = 2.32
  Group = -> [Si_element006,O_element087]
  conduct = 2
  density = 1
  expand = 3
  formula = G4_SILICON_DIOXIDE
  name = G4_SILICON_DIOXIDE
  specific = 4
FEATURE [App::DocumentObjectGroupPython] Ag_element002  label="Ag_element : 1"  # scripted group (container) (typed FeaturePython)
  n = 1
  ref = Ag_element
FEATURE [App::DocumentObjectGroupPython] Br_element005  label="Br_element : 003"  # scripted group (container) (typed FeaturePython)
  n = 1
  ref = Br_element
FEATURE [App::DocumentObjectGroupPython] G4_SILVER_BROMIDE  # scripted group (container) (typed FeaturePython)
  Dunit = g/cm3
  Dvalue = 6.473
  Group = -> [Ag_element002,Br_element005]
  conduct = 2
  density = 1
  expand = 3
  formula = G4_SILVER_BROMIDE
  name = G4_SILVER_BROMIDE
  specific = 4
FEATURE [App::DocumentObjectGroupPython] Ag_element003  label="Ag_element : 002"  # scripted group (container) (typed FeaturePython)
  n = 1
  ref = Ag_element
FEATURE [App::DocumentObjectGroupPython] Cl_element022  label="Cl_element : 011"  # scripted group (container) (typed FeaturePython)
  n = 1
  ref = Cl_element
FEATURE [App::DocumentObjectGroupPython] G4_SILVER_CHLORIDE  # scripted group (container) (typed FeaturePython)
  Dunit = g/cm3
  Dvalue = 5.56
  Group = -> [Ag_element003,Cl_element022]
  conduct = 2
  density = 1
  expand = 3
  formula = G4_SILVER_CHLORIDE
  name = G4_SILVER_CHLORIDE
  specific = 4
FEATURE [App::DocumentObjectGroupPython] Br_element006  label="Br_element : 0.423"  # scripted group (container) (typed FeaturePython)
  n = 0.422895
FEATURE [App::DocumentObjectGroupPython] Ag_element004  label="Ag_element : 0.574"  # scripted group (container) (typed FeaturePython)
  n = 0.573748
FEATURE [App::DocumentObjectGroupPython] I_element007  label="I_element : 0.649"  # scripted group (container) (typed FeaturePython)
  n = 0.003357
FEATURE [App::DocumentObjectGroupPython] G4_SILVER_HALIDES  # scripted group (container) (typed FeaturePython)
  Dunit = g/cm3
  Dvalue = 6.47
  Group = -> [Br_element006,Ag_element004,I_element007]
  conduct = 2
  density = 1
  expand = 3
  formula = G4_SILVER_HALIDES
  name = G4_SILVER_HALIDES
  specific = 4
FEATURE [App::DocumentObjectGroupPython] Ag_element005  label="Ag_element : 003"  # scripted group (container) (typed FeaturePython)
  n = 1
  ref = Ag_element
FEATURE [App::DocumentObjectGroupPython] I_element008  label="I_element : 004"  # scripted group (container) (typed FeaturePython)
  n = 1
  ref = I_element
FEATURE [App::DocumentObjectGroupPython] G4_SILVER_IODIDE  # scripted group (container) (typed FeaturePython)
  Dunit = g/cm3
  Dvalue = 6.01
  Group = -> [Ag_element005,I_element008]
  conduct = 2
  density = 1
  expand = 3
  formula = G4_SILVER_IODIDE
  name = G4_SILVER_IODIDE
  specific = 4
FEATURE [App::DocumentObjectGroupPython] H_element095  label="H_element : 0.100"  # scripted group (container) (typed FeaturePython)
  n = 0.1
FEATURE [App::DocumentObjectGroupPython] C_element103  label="C_element : 0.204"  # scripted group (container) (typed FeaturePython)
  n = 0.204
FEATURE [App::DocumentObjectGroupPython] N_element039  label="N_element : 0.759"  # scripted group (container) (typed FeaturePython)
  n = 0.042
FEATURE [App::DocumentObjectGroupPython] O_element088  label="O_element : 0.645"  # scripted group (container) (typed FeaturePython)
  n = 0.645
FEATURE [App::DocumentObjectGroupPython] Na_element013  label="Na_element : 0.100"  # scripted group (container) (typed FeaturePython)
  n = 0.002
FEATURE [App::DocumentObjectGroupPython] P_element009  label="P_element : 0.107"  # scripted group (container) (typed FeaturePython)
  n = 0.001
FEATURE [App::DocumentObjectGroupPython] S_element020  label="S_element : 0.021"  # scripted group (container) (typed FeaturePython)
  n = 0.002
FEATURE [App::DocumentObjectGroupPython] Cl_element023  label="Cl_element : 0.590"  # scripted group (container) (typed FeaturePython)
  n = 0.003
FEATURE [App::DocumentObjectGroupPython] K_element010  label="K_element : 0.001"  # scripted group (container) (typed FeaturePython)
  n = 0.001
FEATURE [App::DocumentObjectGroupPython] G4_SKIN_ICRP  # scripted group (container) (typed FeaturePython)
  Dunit = g/cm3
  Dvalue = 1.09
  Group = -> [H_element095,C_element103,N_element039,O_element088,Na_element013,P_element009,S_element020,Cl_element023,K_element010]
  conduct = 2
  density = 1
  expand = 3
  formula = G4_SKIN_ICRP
  name = G4_SKIN_ICRP
  specific = 4
FEATURE [App::DocumentObjectGroupPython] Na_element014  label="Na_element : 2"  # scripted group (container) (typed FeaturePython)
  n = 2
  ref = Na_element
FEATURE [App::DocumentObjectGroupPython] C_element104  label="C_element : 058"  # scripted group (container) (typed FeaturePython)
  n = 1
  ref = C_element
FEATURE [App::DocumentObjectGroupPython] O_element089  label="O_element : 049"  # scripted group (container) (typed FeaturePython)
  n = 3
  ref = O_element
FEATURE [App::DocumentObjectGroupPython] G4_SODIUM_CARBONATE  # scripted group (container) (typed FeaturePython)
  Dunit = g/cm3
  Dvalue = 2.532
  Group = -> [Na_element014,C_element104,O_element089]
  conduct = 2
  density = 1
  expand = 3
  formula = G4_SODIUM_CARBONATE
  name = G4_SODIUM_CARBONATE
  specific = 4
FEATURE [App::DocumentObjectGroupPython] Na_element015  label="Na_element : 1"  # scripted group (container) (typed FeaturePython)
  n = 1
  ref = Na_element
FEATURE [App::DocumentObjectGroupPython] I_element009  label="I_element : 005"  # scripted group (container) (typed FeaturePython)
  n = 1
  ref = I_element
FEATURE [App::DocumentObjectGroupPython] G4_SODIUM_IODIDE  # scripted group (container) (typed FeaturePython)
  Dunit = g/cm3
  Dvalue = 3.667
  Group = -> [Na_element015,I_element009]
  conduct = 2
  density = 1
  expand = 3
  formula = G4_SODIUM_IODIDE
  name = G4_SODIUM_IODIDE
  specific = 4
FEATURE [App::DocumentObjectGroupPython] Na_element016  label="Na_element : 003"  # scripted group (container) (typed FeaturePython)
  n = 2
  ref = Na_element
FEATURE [App::DocumentObjectGroupPython] O_element090  label="O_element : 050"  # scripted group (container) (typed FeaturePython)
  n = 1
  ref = O_element
FEATURE [App::DocumentObjectGroupPython] G4_SODIUM_MONOXIDE  # scripted group (container) (typed FeaturePython)
  Dunit = g/cm3
  Dvalue = 2.27
  Group = -> [Na_element016,O_element090]
  conduct = 2
  density = 1
  expand = 3
  formula = G4_SODIUM_MONOXIDE
  name = G4_SODIUM_MONOXIDE
  specific = 4
FEATURE [App::DocumentObjectGroupPython] Na_element017  label="Na_element : 004"  # scripted group (container) (typed FeaturePython)
  n = 1
  ref = Na_element
FEATURE [App::DocumentObjectGroupPython] N_element040  label="N_element : 018"  # scripted group (container) (typed FeaturePython)
  n = 1
  ref = N_element
FEATURE [App::DocumentObjectGroupPython] O_element091  label="O_element : 051"  # scripted group (container) (typed FeaturePython)
  n = 3
  ref = O_element
FEATURE [App::DocumentObjectGroupPython] G4_SODIUM_NITRATE  # scripted group (container) (typed FeaturePython)
  Dunit = g/cm3
  Dvalue = 2.261
  Group = -> [Na_element017,N_element040,O_element091]
  conduct = 2
  density = 1
  expand = 3
  formula = G4_SODIUM_NITRATE
  name = G4_SODIUM_NITRATE
  specific = 4
FEATURE [App::DocumentObjectGroupPython] C_element105  label="C_element : 059"  # scripted group (container) (typed FeaturePython)
  n = 14
  ref = C_element
FEATURE [App::DocumentObjectGroupPython] H_element096  label="H_element : 053"  # scripted group (container) (typed FeaturePython)
  n = 12
  ref = H_element
FEATURE [App::DocumentObjectGroupPython] G4_STILBENE  # scripted group (container) (typed FeaturePython)
  Dunit = g/cm3
  Dvalue = 0.9707
  Group = -> [C_element105,H_element096]
  conduct = 2
  density = 1
  expand = 3
  formula = G4_STILBENE
  name = G4_STILBENE
  specific = 4
FEATURE [App::DocumentObjectGroupPython] C_element106  label="C_element : 12"  # scripted group (container) (typed FeaturePython)
  n = 12
  ref = C_element
FEATURE [App::DocumentObjectGroupPython] H_element097  label="H_element : 22"  # scripted group (container) (typed FeaturePython)
  n = 22
  ref = H_element
FEATURE [App::DocumentObjectGroupPython] O_element092  label="O_element : 11"  # scripted group (container) (typed FeaturePython)
  n = 11
  ref = O_element
FEATURE [App::DocumentObjectGroupPython] G4_SUCROSE  # scripted group (container) (typed FeaturePython)
  Dunit = g/cm3
  Dvalue = 1.5805
  Group = -> [C_element106,H_element097,O_element092]
  conduct = 2
  density = 1
  expand = 3
  formula = G4_SUCROSE
  name = G4_SUCROSE
  specific = 4
FEATURE [App::DocumentObjectGroupPython] C_element107  label="C_element : 18"  # scripted group (container) (typed FeaturePython)
  n = 18
  ref = C_element
FEATURE [App::DocumentObjectGroupPython] H_element098  label="H_element : 054"  # scripted group (container) (typed FeaturePython)
  n = 14
  ref = H_element
FEATURE [App::DocumentObjectGroupPython] G4_TERPHENYL  # scripted group (container) (typed FeaturePython)
  Dunit = g/cm3
  Dvalue = 1.24
  Group = -> [C_element107,H_element098]
  conduct = 2
  density = 1
  expand = 3
  formula = G4_TERPHENYL
  name = G4_TERPHENYL
  specific = 4
FEATURE [App::DocumentObjectGroupPython] H_element099  label="H_element : 0.146"  # scripted group (container) (typed FeaturePython)
  n = 0.106
FEATURE [App::DocumentObjectGroupPython] C_element108  label="C_element : 0.883"  # scripted group (container) (typed FeaturePython)
  n = 0.099
FEATURE [App::DocumentObjectGroupPython] N_element041  label="N_element : 0.020"  # scripted group (container) (typed FeaturePython)
  n = 0.02
FEATURE [App::DocumentObjectGroupPython] O_element093  label="O_element : 0.766"  # scripted group (container) (typed FeaturePython)
  n = 0.766
FEATURE [App::DocumentObjectGroupPython] Na_element018  label="Na_element : 0.101"  # scripted group (container) (typed FeaturePython)
  n = 0.002
FEATURE [App::DocumentObjectGroupPython] P_element010  label="P_element : 0.108"  # scripted group (container) (typed FeaturePython)
  n = 0.001
FEATURE [App::DocumentObjectGroupPython] S_element021  label="S_element : 0.022"  # scripted group (container) (typed FeaturePython)
  n = 0.002
FEATURE [App::DocumentObjectGroupPython] Cl_element024  label="Cl_element : 0.002"  # scripted group (container) (typed FeaturePython)
  n = 0.002
FEATURE [App::DocumentObjectGroupPython] K_element011  label="K_element : 0.017"  # scripted group (container) (typed FeaturePython)
  n = 0.002
FEATURE [App::DocumentObjectGroupPython] G4_TESTIS_ICRP  # scripted group (container) (typed FeaturePython)
  Dunit = g/cm3
  Dvalue = 1.04
  Group = -> [H_element099,C_element108,N_element041,O_element093,Na_element018,P_element010,S_element021,Cl_element024,K_element011]
  conduct = 2
  density = 1
  expand = 3
  formula = G4_TESTIS_ICRP
  name = G4_TESTIS_ICRP
  specific = 4
FEATURE [App::DocumentObjectGroupPython] C_element109  label="C_element : 060"  # scripted group (container) (typed FeaturePython)
  n = 2
  ref = C_element
FEATURE [App::DocumentObjectGroupPython] Cl_element025  label="Cl_element : 012"  # scripted group (container) (typed FeaturePython)
  n = 4
  ref = Cl_element
FEATURE [App::DocumentObjectGroupPython] G4_TETRACHLOROETHYLENE  # scripted group (container) (typed FeaturePython)
  Dunit = g/cm3
  Dvalue = 1.625
  Group = -> [C_element109,Cl_element025]
  conduct = 2
  density = 1
  expand = 3
  formula = G4_TETRACHLOROETHYLENE
  name = G4_TETRACHLOROETHYLENE
  specific = 4
FEATURE [App::DocumentObjectGroupPython] Tl_element001  label="Tl_element : 1"  # scripted group (container) (typed FeaturePython)
  n = 1
  ref = Tl_element
FEATURE [App::DocumentObjectGroupPython] Cl_element026  label="Cl_element : 013"  # scripted group (container) (typed FeaturePython)
  n = 1
  ref = Cl_element
FEATURE [App::DocumentObjectGroupPython] G4_THALLIUM_CHLORIDE  # scripted group (container) (typed FeaturePython)
  Dunit = g/cm3
  Dvalue = 7.004
  Group = -> [Tl_element001,Cl_element026]
  conduct = 2
  density = 1
  expand = 3
  formula = G4_THALLIUM_CHLORIDE
  name = G4_THALLIUM_CHLORIDE
  specific = 4
FEATURE [App::DocumentObjectGroupPython] H_element100  label="H_element : 0.147"  # scripted group (container) (typed FeaturePython)
  n = 0.105
FEATURE [App::DocumentObjectGroupPython] C_element110  label="C_element : 0.256"  # scripted group (container) (typed FeaturePython)
  n = 0.256
FEATURE [App::DocumentObjectGroupPython] N_element042  label="N_element : 0.760"  # scripted group (container) (typed FeaturePython)
  n = 0.027
FEATURE [App::DocumentObjectGroupPython] O_element094  label="O_element : 0.602"  # scripted group (container) (typed FeaturePython)
  n = 0.602
FEATURE [App::DocumentObjectGroupPython] Na_element019  label="Na_element : 0.102"  # scripted group (container) (typed FeaturePython)
  n = 0.001
FEATURE [App::DocumentObjectGroupPython] P_element011  label="P_element : 0.109"  # scripted group (container) (typed FeaturePython)
  n = 0.002
FEATURE [App::DocumentObjectGroupPython] S_element022  label="S_element : 0.023"  # scripted group (container) (typed FeaturePython)
  n = 0.003
FEATURE [App::DocumentObjectGroupPython] Cl_element027  label="Cl_element : 0.591"  # scripted group (container) (typed FeaturePython)
  n = 0.002
FEATURE [App::DocumentObjectGroupPython] K_element012  label="K_element : 0.018"  # scripted group (container) (typed FeaturePython)
  n = 0.002
FEATURE [App::DocumentObjectGroupPython] G4_TISSUE_SOFT_ICRP  # scripted group (container) (typed FeaturePython)
  Dunit = g/cm3
  Dvalue = 1.03
  Group = -> [H_element100,C_element110,N_element042,O_element094,Na_element019,P_element011,S_element022,Cl_element027,K_element012]
  conduct = 2
  density = 1
  expand = 3
  formula = G4_TISSUE_SOFT_ICRP
  name = G4_TISSUE_SOFT_ICRP
  specific = 4
FEATURE [App::DocumentObjectGroupPython] H_element101  label="H_element : 0.148"  # scripted group (container) (typed FeaturePython)
  n = 0.101
FEATURE [App::DocumentObjectGroupPython] C_element111  label="C_element : 0.111"  # scripted group (container) (typed FeaturePython)
  n = 0.111
FEATURE [App::DocumentObjectGroupPython] N_element043  label="N_element : 0.026"  # scripted group (container) (typed FeaturePython)
  n = 0.026
FEATURE [App::DocumentObjectGroupPython] O_element095  label="O_element : 0.762"  # scripted group (container) (typed FeaturePython)
  n = 0.762
FEATURE [App::DocumentObjectGroupPython] G4_TISSUE_SOFT_ICRU_4  label="G4_TISSUE_SOFT_ICRU-4"  # scripted group (container) (typed FeaturePython)
  Dunit = g/cm3
  Dvalue = 1
  Group = -> [H_element101,C_element111,N_element043,O_element095]
  conduct = 2
  density = 1
  expand = 3
  formula = G4_TISSUE_SOFT_ICRU-4
  name = G4_TISSUE_SOFT_ICRU-4
  specific = 4
FEATURE [App::DocumentObjectGroupPython] H_element102  label="H_element : 0.149"  # scripted group (container) (typed FeaturePython)
  n = 0.101869
FEATURE [App::DocumentObjectGroupPython] C_element112  label="C_element : 0.456"  # scripted group (container) (typed FeaturePython)
  n = 0.456179
FEATURE [App::DocumentObjectGroupPython] N_element044  label="N_element : 0.761"  # scripted group (container) (typed FeaturePython)
  n = 0.035172
FEATURE [App::DocumentObjectGroupPython] O_element096  label="O_element : 0.407"  # scripted group (container) (typed FeaturePython)
  n = 0.40678
FEATURE [App::DocumentObjectGroupPython] G4_TISSUE_METHANE  label="G4_TISSUE-METHANE"  # scripted group (container) (typed FeaturePython)
  Dunit = g/cm3
  Dvalue = 0.00106409
  Group = -> [H_element102,C_element112,N_element044,O_element096]
  conduct = 2
  density = 1
  expand = 3
  formula = G4_TISSUE-METHANE
  name = G4_TISSUE-METHANE
  specific = 4
FEATURE [App::DocumentObjectGroupPython] H_element103  label="H_element : 0.103"  # scripted group (container) (typed FeaturePython)
  n = 0.102672
FEATURE [App::DocumentObjectGroupPython] C_element113  label="C_element : 0.569"  # scripted group (container) (typed FeaturePython)
  n = 0.56894
FEATURE [App::DocumentObjectGroupPython] N_element045  label="N_element : 0.762"  # scripted group (container) (typed FeaturePython)
  n = 0.035022
FEATURE [App::DocumentObjectGroupPython] O_element097  label="O_element : 0.293"  # scripted group (container) (typed FeaturePython)
  n = 0.293366
FEATURE [App::DocumentObjectGroupPython] G4_TISSUE_PROPANE  label="G4_TISSUE-PROPANE"  # scripted group (container) (typed FeaturePython)
  Dunit = g/cm3
  Dvalue = 0.00182628
  Group = -> [H_element103,C_element113,N_element045,O_element097]
  conduct = 2
  density = 1
  expand = 3
  formula = G4_TISSUE-PROPANE
  name = G4_TISSUE-PROPANE
  specific = 4
FEATURE [App::DocumentObjectGroupPython] Ti_element003  label="Ti_element : 1"  # scripted group (container) (typed FeaturePython)
  n = 1
  ref = Ti_element
FEATURE [App::DocumentObjectGroupPython] O_element098  label="O_element : 052"  # scripted group (container) (typed FeaturePython)
  n = 2
  ref = O_element
FEATURE [App::DocumentObjectGroupPython] G4_TITANIUM_DIOXIDE  # scripted group (container) (typed FeaturePython)
  Dunit = g/cm3
  Dvalue = 4.26
  Group = -> [Ti_element003,O_element098]
  conduct = 2
  density = 1
  expand = 3
  formula = G4_TITANIUM_DIOXIDE
  name = G4_TITANIUM_DIOXIDE
  specific = 4
FEATURE [App::DocumentObjectGroupPython] C_element114  label="C_element : 061"  # scripted group (container) (typed FeaturePython)
  n = 7
  ref = C_element
FEATURE [App::DocumentObjectGroupPython] H_element104  label="H_element : 055"  # scripted group (container) (typed FeaturePython)
  n = 8
  ref = H_element
FEATURE [App::DocumentObjectGroupPython] G4_TOLUENE  # scripted group (container) (typed FeaturePython)
  Dunit = g/cm3
  Dvalue = 0.8669
  Group = -> [C_element114,H_element104]
  conduct = 2
  density = 1
  expand = 3
  formula = G4_TOLUENE
  name = G4_TOLUENE
  specific = 4
FEATURE [App::DocumentObjectGroupPython] C_element115  label="C_element : 062"  # scripted group (container) (typed FeaturePython)
  n = 2
  ref = C_element
FEATURE [App::DocumentObjectGroupPython] H_element105  label="H_element : 056"  # scripted group (container) (typed FeaturePython)
  n = 1
  ref = H_element
FEATURE [App::DocumentObjectGroupPython] Cl_element028  label="Cl_element : 014"  # scripted group (container) (typed FeaturePython)
  n = 3
  ref = Cl_element
FEATURE [App::DocumentObjectGroupPython] G4_TRICHLOROETHYLENE  # scripted group (container) (typed FeaturePython)
  Dunit = g/cm3
  Dvalue = 1.46
  Group = -> [C_element115,H_element105,Cl_element028]
  conduct = 2
  density = 1
  expand = 3
  formula = G4_TRICHLOROETHYLENE
  name = G4_TRICHLOROETHYLENE
  specific = 4
FEATURE [App::DocumentObjectGroupPython] C_element116  label="C_element : 063"  # scripted group (container) (typed FeaturePython)
  n = 6
  ref = C_element
FEATURE [App::DocumentObjectGroupPython] H_element106  label="H_element : 15"  # scripted group (container) (typed FeaturePython)
  n = 15
  ref = H_element
FEATURE [App::DocumentObjectGroupPython] O_element099  label="O_element : 053"  # scripted group (container) (typed FeaturePython)
  n = 4
  ref = O_element
FEATURE [App::DocumentObjectGroupPython] P_element012  label="P_element : 1"  # scripted group (container) (typed FeaturePython)
  n = 1
  ref = P_element
FEATURE [App::DocumentObjectGroupPython] G4_TRIETHYL_PHOSPHATE  # scripted group (container) (typed FeaturePython)
  Dunit = g/cm3
  Dvalue = 1.07
  Group = -> [C_element116,H_element106,O_element099,P_element012]
  conduct = 2
  density = 1
  expand = 3
  formula = G4_TRIETHYL_PHOSPHATE
  name = G4_TRIETHYL_PHOSPHATE
  specific = 4
FEATURE [App::DocumentObjectGroupPython] W_element003  label="W_element : 003"  # scripted group (container) (typed FeaturePython)
  n = 1
  ref = W_element
FEATURE [App::DocumentObjectGroupPython] F_element017  label="F_element : 6"  # scripted group (container) (typed FeaturePython)
  n = 6
  ref = F_element
FEATURE [App::DocumentObjectGroupPython] G4_TUNGSTEN_HEXAFLUORIDE  # scripted group (container) (typed FeaturePython)
  Dunit = g/cm3
  Dvalue = 2.4
  Group = -> [W_element003,F_element017]
  conduct = 2
  density = 1
  expand = 3
  formula = G4_TUNGSTEN_HEXAFLUORIDE
  name = G4_TUNGSTEN_HEXAFLUORIDE
  specific = 4
FEATURE [App::DocumentObjectGroupPython] U_element001  label="U_element : 1"  # scripted group (container) (typed FeaturePython)
  n = 1
  ref = U_element
FEATURE [App::DocumentObjectGroupPython] C_element117  label="C_element : 064"  # scripted group (container) (typed FeaturePython)
  n = 2
  ref = C_element
FEATURE [App::DocumentObjectGroupPython] G4_URANIUM_DICARBIDE  # scripted group (container) (typed FeaturePython)
  Dunit = g/cm3
  Dvalue = 11.28
  Group = -> [U_element001,C_element117]
  conduct = 2
  density = 1
  expand = 3
  formula = G4_URANIUM_DICARBIDE
  name = G4_URANIUM_DICARBIDE
  specific = 4
FEATURE [App::DocumentObjectGroupPython] U_element002  label="U_element : 002"  # scripted group (container) (typed FeaturePython)
  n = 1
  ref = U_element
FEATURE [App::DocumentObjectGroupPython] C_element118  label="C_element : 065"  # scripted group (container) (typed FeaturePython)
  n = 1
  ref = C_element
FEATURE [App::DocumentObjectGroupPython] G4_URANIUM_MONOCARBIDE  # scripted group (container) (typed FeaturePython)
  Dunit = g/cm3
  Dvalue = 13.63
  Group = -> [U_element002,C_element118]
  conduct = 2
  density = 1
  expand = 3
  formula = G4_URANIUM_MONOCARBIDE
  name = G4_URANIUM_MONOCARBIDE
  specific = 4
FEATURE [App::DocumentObjectGroupPython] U_element003  label="U_element : 003"  # scripted group (container) (typed FeaturePython)
  n = 1
  ref = U_element
FEATURE [App::DocumentObjectGroupPython] O_element100  label="O_element : 054"  # scripted group (container) (typed FeaturePython)
  n = 2
  ref = O_element
FEATURE [App::DocumentObjectGroupPython] G4_URANIUM_OXIDE  # scripted group (container) (typed FeaturePython)
  Dunit = g/cm3
  Dvalue = 10.96
  Group = -> [U_element003,O_element100]
  conduct = 2
  density = 1
  expand = 3
  formula = G4_URANIUM_OXIDE
  name = G4_URANIUM_OXIDE
  specific = 4
FEATURE [App::DocumentObjectGroupPython] C_element119  label="C_element : 066"  # scripted group (container) (typed FeaturePython)
  n = 1
  ref = C_element
FEATURE [App::DocumentObjectGroupPython] H_element107  label="H_element : 057"  # scripted group (container) (typed FeaturePython)
  n = 4
  ref = H_element
FEATURE [App::DocumentObjectGroupPython] N_element046  label="N_element : 019"  # scripted group (container) (typed FeaturePython)
  n = 2
  ref = N_element
FEATURE [App::DocumentObjectGroupPython] O_element101  label="O_element : 055"  # scripted group (container) (typed FeaturePython)
  n = 1
  ref = O_element
FEATURE [App::DocumentObjectGroupPython] G4_UREA  # scripted group (container) (typed FeaturePython)
  Dunit = g/cm3
  Dvalue = 1.323
  Group = -> [C_element119,H_element107,N_element046,O_element101]
  conduct = 2
  density = 1
  expand = 3
  formula = G4_UREA
  name = G4_UREA
  specific = 4
FEATURE [App::DocumentObjectGroupPython] C_element120  label="C_element : 067"  # scripted group (container) (typed FeaturePython)
  n = 5
  ref = C_element
FEATURE [App::DocumentObjectGroupPython] H_element108  label="H_element : 058"  # scripted group (container) (typed FeaturePython)
  n = 11
  ref = H_element
FEATURE [App::DocumentObjectGroupPython] N_element047  label="N_element : 020"  # scripted group (container) (typed FeaturePython)
  n = 1
  ref = N_element
FEATURE [App::DocumentObjectGroupPython] O_element102  label="O_element : 056"  # scripted group (container) (typed FeaturePython)
  n = 2
  ref = O_element
FEATURE [App::DocumentObjectGroupPython] G4_VALINE  # scripted group (container) (typed FeaturePython)
  Dunit = g/cm3
  Dvalue = 1.23
  Group = -> [C_element120,H_element108,N_element047,O_element102]
  conduct = 2
  density = 1
  expand = 3
  formula = G4_VALINE
  name = G4_VALINE
  specific = 4
FEATURE [App::DocumentObjectGroupPython] H_element109  label="H_element : 0.009"  # scripted group (container) (typed FeaturePython)
  n = 0.009417
FEATURE [App::DocumentObjectGroupPython] C_element121  label="C_element : 0.281"  # scripted group (container) (typed FeaturePython)
  n = 0.280555
FEATURE [App::DocumentObjectGroupPython] F_element018  label="F_element : 0.710"  # scripted group (container) (typed FeaturePython)
  n = 0.710028
FEATURE [App::DocumentObjectGroupPython] G4_VITON  # scripted group (container) (typed FeaturePython)
  Dunit = g/cm3
  Dvalue = 1.8
  Group = -> [H_element109,C_element121,F_element018]
  conduct = 2
  density = 1
  expand = 3
  formula = G4_VITON
  name = G4_VITON
  specific = 4
FEATURE [App::DocumentObjectGroupPython] H_element110  label="H_element : 059"  # scripted group (container) (typed FeaturePython)
  n = 2
  ref = H_element
FEATURE [App::DocumentObjectGroupPython] O_element103  label="O_element : 057"  # scripted group (container) (typed FeaturePython)
  n = 1
  ref = O_element
FEATURE [App::DocumentObjectGroupPython] G4_WATER  # scripted group (container) (typed FeaturePython)
  Dunit = g/cm3
  Dvalue = 1
  Group = -> [H_element110,O_element103]
  conduct = 2
  density = 1
  expand = 3
  formula = G4_WATER
  name = G4_WATER
  specific = 4
FEATURE [App::DocumentObjectGroupPython] H_element111  label="H_element : 060"  # scripted group (container) (typed FeaturePython)
  n = 2
  ref = H_element
FEATURE [App::DocumentObjectGroupPython] O_element104  label="O_element : 058"  # scripted group (container) (typed FeaturePython)
  n = 1
  ref = O_element
FEATURE [App::DocumentObjectGroupPython] G4_WATER_VAPOR  # scripted group (container) (typed FeaturePython)
  Dunit = g/cm3
  Dvalue = 0.000756182
  Group = -> [H_element111,O_element104]
  conduct = 2
  density = 1
  expand = 3
  formula = G4_WATER_VAPOR
  name = G4_WATER_VAPOR
  specific = 4
FEATURE [App::DocumentObjectGroupPython] C_element122  label="C_element : 068"  # scripted group (container) (typed FeaturePython)
  n = 8
  ref = C_element
FEATURE [App::DocumentObjectGroupPython] H_element112  label="H_element : 061"  # scripted group (container) (typed FeaturePython)
  n = 10
  ref = H_element
FEATURE [App::DocumentObjectGroupPython] G4_XYLENE  # scripted group (container) (typed FeaturePython)
  Dunit = g/cm3
  Dvalue = 0.87
  Group = -> [C_element122,H_element112]
  conduct = 2
  density = 1
  expand = 3
  formula = G4_XYLENE
  name = G4_XYLENE
  specific = 4
FEATURE [App::DocumentObjectGroupPython] C_element123  label="C_element : 069"  # scripted group (container) (typed FeaturePython)
  n = 1
  ref = C_element
FEATURE [App::DocumentObjectGroupPython] G4_GRAPHITE  # scripted group (container) (typed FeaturePython)
  Dunit = g/cm3
  Dvalue = 2.21
  Group = -> [C_element123]
  conduct = 2
  density = 1
  expand = 3
  formula = G4_GRAPHITE
  name = G4_GRAPHITE
  specific = 4
FEATURE [App::DocumentObjectGroupPython] NIST  # scripted group (container) (typed FeaturePython)
  Group = -> [G4_A_150_TISSUE,G4_ACETONE,G4_ACETYLENE,G4_ADENINE,G4_ADIPOSE_TISSUE_ICRP,G4_AIR,G4_ALANINE,G4_ALUMINUM_OXIDE,G4_AMBER,G4_AMMONIA,G4_ANILINE,G4_ANTHRACENE,G4_B_100_BONE,G4_BAKELITE,G4_BARIUM_FLUORIDE,G4_BARIUM_SULFATE,G4_BENZENE,G4_BERYLLIUM_OXIDE,G4_BGO,G4_BLOOD_ICRP,G4_BONE_COMPACT_ICRU,G4_BONE_CORTICAL_ICRP,G4_BORON_CARBIDE,G4_BORON_OXIDE,G4_BRAIN_ICRP,G4_BUTANE,G4_N_BUTYL_ALCOHOL,G4_C_552,+152 more]
FEATURE [App::DocumentObjectGroupPython] H_element113  label="H_element : 062"  # scripted group (container) (typed FeaturePython)
  n = 1
  ref = H_element
FEATURE [App::DocumentObjectGroupPython] G4_H  # scripted group (container) (typed FeaturePython)
  Dunit = g/cm3
  Dvalue = 8.3748e-05
  Group = -> [H_element113]
  conduct = 2
  density = 1
  expand = 3
  formula = H
  name = G4_H
  specific = 4
FEATURE [App::DocumentObjectGroupPython] He_element001  label="He_element : 1"  # scripted group (container) (typed FeaturePython)
  n = 1
  ref = He_element
FEATURE [App::DocumentObjectGroupPython] G4_He  # scripted group (container) (typed FeaturePython)
  Dunit = g/cm3
  Dvalue = 0.000166322
  Group = -> [He_element001]
  conduct = 2
  density = 1
  expand = 3
  formula = He
  name = G4_He
  specific = 4
FEATURE [App::DocumentObjectGroupPython] Li_element008  label="Li_element : 008"  # scripted group (container) (typed FeaturePython)
  n = 1
  ref = Li_element
FEATURE [App::DocumentObjectGroupPython] G4_Li  # scripted group (container) (typed FeaturePython)
  Dunit = g/cm3
  Dvalue = 0.534
  Group = -> [Li_element008]
  conduct = 2
  density = 1
  expand = 3
  formula = Li
  name = G4_Li
  specific = 4
FEATURE [App::DocumentObjectGroupPython] Be_element002  label="Be_element : 002"  # scripted group (container) (typed FeaturePython)
  n = 1
  ref = Be_element
FEATURE [App::DocumentObjectGroupPython] G4_Be  # scripted group (container) (typed FeaturePython)
  Dunit = g/cm3
  Dvalue = 1.848
  Group = -> [Be_element002]
  conduct = 2
  density = 1
  expand = 3
  formula = Be
  name = G4_Be
  specific = 4
FEATURE [App::DocumentObjectGroupPython] B_element007  label="B_element : 007"  # scripted group (container) (typed FeaturePython)
  n = 1
  ref = B_element
FEATURE [App::DocumentObjectGroupPython] G4_B  # scripted group (container) (typed FeaturePython)
  Dunit = g/cm3
  Dvalue = 2.37
  Group = -> [B_element007]
  conduct = 2
  density = 1
  expand = 3
  formula = B
  name = G4_B
  specific = 4
FEATURE [App::DocumentObjectGroupPython] C_element124  label="C_element : 070"  # scripted group (container) (typed FeaturePython)
  n = 1
  ref = C_element
FEATURE [App::DocumentObjectGroupPython] G4_C  # scripted group (container) (typed FeaturePython)
  Dunit = g/cm3
  Dvalue = 2
  Group = -> [C_element124]
  conduct = 2
  density = 1
  expand = 3
  formula = C
  name = G4_C
  specific = 4
FEATURE [App::DocumentObjectGroupPython] N_element048  label="N_element : 021"  # scripted group (container) (typed FeaturePython)
  n = 1
  ref = N_element
FEATURE [App::DocumentObjectGroupPython] G4_N  # scripted group (container) (typed FeaturePython)
  Dunit = g/cm3
  Dvalue = 0.0011652
  Group = -> [N_element048]
  conduct = 2
  density = 1
  expand = 3
  formula = N
  name = G4_N
  specific = 4
FEATURE [App::DocumentObjectGroupPython] O_element105  label="O_element : 059"  # scripted group (container) (typed FeaturePython)
  n = 1
  ref = O_element
FEATURE [App::DocumentObjectGroupPython] G4_O  # scripted group (container) (typed FeaturePython)
  Dunit = g/cm3
  Dvalue = 0.00133151
  Group = -> [O_element105]
  conduct = 2
  density = 1
  expand = 3
  formula = O
  name = G4_O
  specific = 4
FEATURE [App::DocumentObjectGroupPython] F_element019  label="F_element : 008"  # scripted group (container) (typed FeaturePython)
  n = 1
  ref = F_element
FEATURE [App::DocumentObjectGroupPython] G4_F  # scripted group (container) (typed FeaturePython)
  Dunit = g/cm3
  Dvalue = 0.00158029
  Group = -> [F_element019]
  conduct = 2
  density = 1
  expand = 3
  formula = F
  name = G4_F
  specific = 4
FEATURE [App::DocumentObjectGroupPython] Ne_element001  label="Ne_element : 1"  # scripted group (container) (typed FeaturePython)
  n = 1
  ref = Ne_element
FEATURE [App::DocumentObjectGroupPython] G4_Ne  # scripted group (container) (typed FeaturePython)
  Dunit = g/cm3
  Dvalue = 0.000838505
  Group = -> [Ne_element001]
  conduct = 2
  density = 1
  expand = 3
  formula = Ne
  name = G4_Ne
  specific = 4
FEATURE [App::DocumentObjectGroupPython] Na_element020  label="Na_element : 005"  # scripted group (container) (typed FeaturePython)
  n = 1
  ref = Na_element
FEATURE [App::DocumentObjectGroupPython] G4_Na  # scripted group (container) (typed FeaturePython)
  Dunit = g/cm3
  Dvalue = 0.971
  Group = -> [Na_element020]
  conduct = 2
  density = 1
  expand = 3
  formula = Na
  name = G4_Na
  specific = 4
FEATURE [App::DocumentObjectGroupPython] Mg_element011  label="Mg_element : 005"  # scripted group (container) (typed FeaturePython)
  n = 1
  ref = Mg_element
FEATURE [App::DocumentObjectGroupPython] G4_Mg  # scripted group (container) (typed FeaturePython)
  Dunit = g/cm3
  Dvalue = 1.74
  Group = -> [Mg_element011]
  conduct = 2
  density = 1
  expand = 3
  formula = Mg
  name = G4_Mg
  specific = 4
FEATURE [App::DocumentObjectGroupPython] Al_element004  label="Al_element : 1"  # scripted group (container) (typed FeaturePython)
  n = 1
  ref = Al_element
FEATURE [App::DocumentObjectGroupPython] G4_Al  # scripted group (container) (typed FeaturePython)
  Dunit = g/cm3
  Dvalue = 2.699
  Group = -> [Al_element004]
  conduct = 2
  density = 1
  expand = 3
  formula = Al
  name = G4_Al
  specific = 4
FEATURE [App::DocumentObjectGroupPython] Si_element007  label="Si_element : 002"  # scripted group (container) (typed FeaturePython)
  n = 1
  ref = Si_element
FEATURE [App::DocumentObjectGroupPython] G4_Si  # scripted group (container) (typed FeaturePython)
  Dunit = g/cm3
  Dvalue = 2.33
  Group = -> [Si_element007]
  conduct = 2
  density = 1
  expand = 3
  formula = Si
  name = G4_Si
  specific = 4
FEATURE [App::DocumentObjectGroupPython] P_element013  label="P_element : 002"  # scripted group (container) (typed FeaturePython)
  n = 1
  ref = P_element
FEATURE [App::DocumentObjectGroupPython] G4_P  # scripted group (container) (typed FeaturePython)
  Dunit = g/cm3
  Dvalue = 2.2
  Group = -> [P_element013]
  conduct = 2
  density = 1
  expand = 3
  formula = P
  name = G4_P
  specific = 4
FEATURE [App::DocumentObjectGroupPython] S_element023  label="S_element : 007"  # scripted group (container) (typed FeaturePython)
  n = 1
  ref = S_element
FEATURE [App::DocumentObjectGroupPython] G4_S  # scripted group (container) (typed FeaturePython)
  Dunit = g/cm3
  Dvalue = 2
  Group = -> [S_element023]
  conduct = 2
  density = 1
  expand = 3
  formula = S
  name = G4_S
  specific = 4
FEATURE [App::DocumentObjectGroupPython] Cl_element029  label="Cl_element : 015"  # scripted group (container) (typed FeaturePython)
  n = 1
  ref = Cl_element
FEATURE [App::DocumentObjectGroupPython] G4_Cl  # scripted group (container) (typed FeaturePython)
  Dunit = g/cm3
  Dvalue = 0.00299473
  Group = -> [Cl_element029]
  conduct = 2
  density = 1
  expand = 3
  formula = Cl
  name = G4_Cl
  specific = 4
FEATURE [App::DocumentObjectGroupPython] Ar_element002  label="Ar_element : 1"  # scripted group (container) (typed FeaturePython)
  n = 1
  ref = Ar_element
FEATURE [App::DocumentObjectGroupPython] G4_Ar  # scripted group (container) (typed FeaturePython)
  Dunit = g/cm3
  Dvalue = 0.00166201
  Group = -> [Ar_element002]
  conduct = 2
  density = 1
  expand = 3
  formula = Ar
  name = G4_Ar
  specific = 4
FEATURE [App::DocumentObjectGroupPython] K_element013  label="K_element : 003"  # scripted group (container) (typed FeaturePython)
  n = 1
  ref = K_element
FEATURE [App::DocumentObjectGroupPython] G4_K  # scripted group (container) (typed FeaturePython)
  Dunit = g/cm3
  Dvalue = 0.862
  Group = -> [K_element013]
  conduct = 2
  density = 1
  expand = 3
  formula = K
  name = G4_K
  specific = 4
FEATURE [App::DocumentObjectGroupPython] Ca_element014  label="Ca_element : 007"  # scripted group (container) (typed FeaturePython)
  n = 1
  ref = Ca_element
FEATURE [App::DocumentObjectGroupPython] G4_Ca  # scripted group (container) (typed FeaturePython)
  Dunit = g/cm3
  Dvalue = 1.55
  Group = -> [Ca_element014]
  conduct = 2
  density = 1
  expand = 3
  formula = Ca
  name = G4_Ca
  specific = 4
FEATURE [App::DocumentObjectGroupPython] Sc_element001  label="Sc_element : 1"  # scripted group (container) (typed FeaturePython)
  n = 1
  ref = Sc_element
FEATURE [App::DocumentObjectGroupPython] G4_Sc  # scripted group (container) (typed FeaturePython)
  Dunit = g/cm3
  Dvalue = 2.989
  Group = -> [Sc_element001]
  conduct = 2
  density = 1
  expand = 3
  formula = Sc
  name = G4_Sc
  specific = 4
FEATURE [App::DocumentObjectGroupPython] Ti_element004  label="Ti_element : 002"  # scripted group (container) (typed FeaturePython)
  n = 1
  ref = Ti_element
FEATURE [App::DocumentObjectGroupPython] G4_Ti  # scripted group (container) (typed FeaturePython)
  Dunit = g/cm3
  Dvalue = 4.54
  Group = -> [Ti_element004]
  conduct = 2
  density = 1
  expand = 3
  formula = Ti
  name = G4_Ti
  specific = 4
FEATURE [App::DocumentObjectGroupPython] V_element001  label="V_element : 1"  # scripted group (container) (typed FeaturePython)
  n = 1
  ref = V_element
FEATURE [App::DocumentObjectGroupPython] G4_V  # scripted group (container) (typed FeaturePython)
  Dunit = g/cm3
  Dvalue = 6.11
  Group = -> [V_element001]
  conduct = 2
  density = 1
  expand = 3
  formula = V
  name = G4_V
  specific = 4
FEATURE [App::DocumentObjectGroupPython] Cr_element001  label="Cr_element : 1"  # scripted group (container) (typed FeaturePython)
  n = 1
  ref = Cr_element
FEATURE [App::DocumentObjectGroupPython] G4_Cr  # scripted group (container) (typed FeaturePython)
  Dunit = g/cm3
  Dvalue = 7.18
  Group = -> [Cr_element001]
  conduct = 2
  density = 1
  expand = 3
  formula = Cr
  name = G4_Cr
  specific = 4
FEATURE [App::DocumentObjectGroupPython] Mn_element001  label="Mn_element : 1"  # scripted group (container) (typed FeaturePython)
  n = 1
  ref = Mn_element
FEATURE [App::DocumentObjectGroupPython] G4_Mn  # scripted group (container) (typed FeaturePython)
  Dunit = g/cm3
  Dvalue = 7.44
  Group = -> [Mn_element001]
  conduct = 2
  density = 1
  expand = 3
  formula = Mn
  name = G4_Mn
  specific = 4
FEATURE [App::DocumentObjectGroupPython] Fe_element007  label="Fe_element : 004"  # scripted group (container) (typed FeaturePython)
  n = 1
  ref = Fe_element
FEATURE [App::DocumentObjectGroupPython] G4_Fe  # scripted group (container) (typed FeaturePython)
  Dunit = g/cm3
  Dvalue = 7.874
  Group = -> [Fe_element007]
  conduct = 2
  density = 1
  expand = 3
  formula = Fe
  name = G4_Fe
  specific = 4
FEATURE [App::DocumentObjectGroupPython] Co_element001  label="Co_element : 1"  # scripted group (container) (typed FeaturePython)
  n = 1
  ref = Co_element
FEATURE [App::DocumentObjectGroupPython] G4_Co  # scripted group (container) (typed FeaturePython)
  Dunit = g/cm3
  Dvalue = 8.9
  Group = -> [Co_element001]
  conduct = 2
  density = 1
  expand = 3
  formula = Co
  name = G4_Co
  specific = 4
FEATURE [App::DocumentObjectGroupPython] Ni_element001  label="Ni_element : 1"  # scripted group (container) (typed FeaturePython)
  n = 1
  ref = Ni_element
FEATURE [App::DocumentObjectGroupPython] G4_Ni  # scripted group (container) (typed FeaturePython)
  Dunit = g/cm3
  Dvalue = 8.902
  Group = -> [Ni_element001]
  conduct = 2
  density = 1
  expand = 3
  formula = Ni
  name = G4_Ni
  specific = 4
FEATURE [App::DocumentObjectGroupPython] Cu_element001  label="Cu_element : 1"  # scripted group (container) (typed FeaturePython)
  n = 1
  ref = Cu_element
FEATURE [App::DocumentObjectGroupPython] G4_Cu  # scripted group (container) (typed FeaturePython)
  Dunit = g/cm3
  Dvalue = 8.96
  Group = -> [Cu_element001]
  conduct = 2
  density = 1
  expand = 3
  formula = Cu
  name = G4_Cu
  specific = 4
FEATURE [App::DocumentObjectGroupPython] Zn_element001  label="Zn_element : 1"  # scripted group (container) (typed FeaturePython)
  n = 1
  ref = Zn_element
FEATURE [App::DocumentObjectGroupPython] G4_Zn  # scripted group (container) (typed FeaturePython)
  Dunit = g/cm3
  Dvalue = 7.133
  Group = -> [Zn_element001]
  conduct = 2
  density = 1
  expand = 3
  formula = Zn
  name = G4_Zn
  specific = 4
FEATURE [App::DocumentObjectGroupPython] Ga_element002  label="Ga_element : 002"  # scripted group (container) (typed FeaturePython)
  n = 1
  ref = Ga_element
FEATURE [App::DocumentObjectGroupPython] G4_Ga  # scripted group (container) (typed FeaturePython)
  Dunit = g/cm3
  Dvalue = 5.904
  Group = -> [Ga_element002]
  conduct = 2
  density = 1
  expand = 3
  formula = Ga
  name = G4_Ga
  specific = 4
FEATURE [App::DocumentObjectGroupPython] Ge_element002  label="Ge_element : 1"  # scripted group (container) (typed FeaturePython)
  n = 1
  ref = Ge_element
FEATURE [App::DocumentObjectGroupPython] G4_Ge  # scripted group (container) (typed FeaturePython)
  Dunit = g/cm3
  Dvalue = 5.323
  Group = -> [Ge_element002]
  conduct = 2
  density = 1
  expand = 3
  formula = Ge
  name = G4_Ge
  specific = 4
FEATURE [App::DocumentObjectGroupPython] As_element003  label="As_element : 002"  # scripted group (container) (typed FeaturePython)
  n = 1
  ref = As_element
FEATURE [App::DocumentObjectGroupPython] G4_As  # scripted group (container) (typed FeaturePython)
  Dunit = g/cm3
  Dvalue = 5.73
  Group = -> [As_element003]
  conduct = 2
  density = 1
  expand = 3
  formula = As
  name = G4_As
  specific = 4
FEATURE [App::DocumentObjectGroupPython] Se_element001  label="Se_element : 1"  # scripted group (container) (typed FeaturePython)
  n = 1
  ref = Se_element
FEATURE [App::DocumentObjectGroupPython] G4_Se  # scripted group (container) (typed FeaturePython)
  Dunit = g/cm3
  Dvalue = 4.5
  Group = -> [Se_element001]
  conduct = 2
  density = 1
  expand = 3
  formula = Se
  name = G4_Se
  specific = 4
FEATURE [App::DocumentObjectGroupPython] Br_element007  label="Br_element : 004"  # scripted group (container) (typed FeaturePython)
  n = 1
  ref = Br_element
FEATURE [App::DocumentObjectGroupPython] G4_Br  # scripted group (container) (typed FeaturePython)
  Dunit = g/cm3
  Dvalue = 0.0070721
  Group = -> [Br_element007]
  conduct = 2
  density = 1
  expand = 3
  formula = Br
  name = G4_Br
  specific = 4
FEATURE [App::DocumentObjectGroupPython] Kr_element001  label="Kr_element : 1"  # scripted group (container) (typed FeaturePython)
  n = 1
  ref = Kr_element
FEATURE [App::DocumentObjectGroupPython] G4_Kr  # scripted group (container) (typed FeaturePython)
  Dunit = g/cm3
  Dvalue = 0.00347832
  Group = -> [Kr_element001]
  conduct = 2
  density = 1
  expand = 3
  formula = Kr
  name = G4_Kr
  specific = 4
FEATURE [App::DocumentObjectGroupPython] Rb_element001  label="Rb_element : 1"  # scripted group (container) (typed FeaturePython)
  n = 1
  ref = Rb_element
FEATURE [App::DocumentObjectGroupPython] G4_Rb  # scripted group (container) (typed FeaturePython)
  Dunit = g/cm3
  Dvalue = 1.532
  Group = -> [Rb_element001]
  conduct = 2
  density = 1
  expand = 3
  formula = Rb
  name = G4_Rb
  specific = 4
FEATURE [App::DocumentObjectGroupPython] Sr_element001  label="Sr_element : 1"  # scripted group (container) (typed FeaturePython)
  n = 1
  ref = Sr_element
FEATURE [App::DocumentObjectGroupPython] G4_Sr  # scripted group (container) (typed FeaturePython)
  Dunit = g/cm3
  Dvalue = 2.54
  Group = -> [Sr_element001]
  conduct = 2
  density = 1
  expand = 3
  formula = Sr
  name = G4_Sr
  specific = 4
FEATURE [App::DocumentObjectGroupPython] Y_element001  label="Y_element : 1"  # scripted group (container) (typed FeaturePython)
  n = 1
  ref = Y_element
FEATURE [App::DocumentObjectGroupPython] G4_Y  # scripted group (container) (typed FeaturePython)
  Dunit = g/cm3
  Dvalue = 4.469
  Group = -> [Y_element001]
  conduct = 2
  density = 1
  expand = 3
  formula = Y
  name = G4_Y
  specific = 4
FEATURE [App::DocumentObjectGroupPython] Zr_element001  label="Zr_element : 1"  # scripted group (container) (typed FeaturePython)
  n = 1
  ref = Zr_element
FEATURE [App::DocumentObjectGroupPython] G4_Zr  # scripted group (container) (typed FeaturePython)
  Dunit = g/cm3
  Dvalue = 6.506
  Group = -> [Zr_element001]
  conduct = 2
  density = 1
  expand = 3
  formula = Zr
  name = G4_Zr
  specific = 4
FEATURE [App::DocumentObjectGroupPython] Nb_element001  label="Nb_element : 1"  # scripted group (container) (typed FeaturePython)
  n = 1
  ref = Nb_element
FEATURE [App::DocumentObjectGroupPython] G4_Nb  # scripted group (container) (typed FeaturePython)
  Dunit = g/cm3
  Dvalue = 8.57
  Group = -> [Nb_element001]
  conduct = 2
  density = 1
  expand = 3
  formula = Nb
  name = G4_Nb
  specific = 4
FEATURE [App::DocumentObjectGroupPython] Mo_element001  label="Mo_element : 1"  # scripted group (container) (typed FeaturePython)
  n = 1
  ref = Mo_element
FEATURE [App::DocumentObjectGroupPython] G4_Mo  # scripted group (container) (typed FeaturePython)
  Dunit = g/cm3
  Dvalue = 10.22
  Group = -> [Mo_element001]
  conduct = 2
  density = 1
  expand = 3
  formula = Mo
  name = G4_Mo
  specific = 4
FEATURE [App::DocumentObjectGroupPython] Tc_element001  label="Tc_element : 1"  # scripted group (container) (typed FeaturePython)
  n = 1
  ref = Tc_element
FEATURE [App::DocumentObjectGroupPython] G4_Tc  # scripted group (container) (typed FeaturePython)
  Dunit = g/cm3
  Dvalue = 11.5
  Group = -> [Tc_element001]
  conduct = 2
  density = 1
  expand = 3
  formula = Tc
  name = G4_Tc
  specific = 4
FEATURE [App::DocumentObjectGroupPython] Ru_element001  label="Ru_element : 1"  # scripted group (container) (typed FeaturePython)
  n = 1
  ref = Ru_element
FEATURE [App::DocumentObjectGroupPython] G4_Ru  # scripted group (container) (typed FeaturePython)
  Dunit = g/cm3
  Dvalue = 12.41
  Group = -> [Ru_element001]
  conduct = 2
  density = 1
  expand = 3
  formula = Ru
  name = G4_Ru
  specific = 4
FEATURE [App::DocumentObjectGroupPython] Rh_element001  label="Rh_element : 1"  # scripted group (container) (typed FeaturePython)
  n = 1
  ref = Rh_element
FEATURE [App::DocumentObjectGroupPython] G4_Rh  # scripted group (container) (typed FeaturePython)
  Dunit = g/cm3
  Dvalue = 12.41
  Group = -> [Rh_element001]
  conduct = 2
  density = 1
  expand = 3
  formula = Rh
  name = G4_Rh
  specific = 4
FEATURE [App::DocumentObjectGroupPython] Pd_element001  label="Pd_element : 1"  # scripted group (container) (typed FeaturePython)
  n = 1
  ref = Pd_element
FEATURE [App::DocumentObjectGroupPython] G4_Pd  # scripted group (container) (typed FeaturePython)
  Dunit = g/cm3
  Dvalue = 12.02
  Group = -> [Pd_element001]
  conduct = 2
  density = 1
  expand = 3
  formula = Pd
  name = G4_Pd
  specific = 4
FEATURE [App::DocumentObjectGroupPython] Ag_element006  label="Ag_element : 004"  # scripted group (container) (typed FeaturePython)
  n = 1
  ref = Ag_element
FEATURE [App::DocumentObjectGroupPython] G4_Ag  # scripted group (container) (typed FeaturePython)
  Dunit = g/cm3
  Dvalue = 10.5
  Group = -> [Ag_element006]
  conduct = 2
  density = 1
  expand = 3
  formula = Ag
  name = G4_Ag
  specific = 4
FEATURE [App::DocumentObjectGroupPython] Cd_element003  label="Cd_element : 003"  # scripted group (container) (typed FeaturePython)
  n = 1
  ref = Cd_element
FEATURE [App::DocumentObjectGroupPython] G4_Cd  # scripted group (container) (typed FeaturePython)
  Dunit = g/cm3
  Dvalue = 8.65
  Group = -> [Cd_element003]
  conduct = 2
  density = 1
  expand = 3
  formula = Cd
  name = G4_Cd
  specific = 4
FEATURE [App::DocumentObjectGroupPython] In_element001  label="In_element : 1"  # scripted group (container) (typed FeaturePython)
  n = 1
  ref = In_element
FEATURE [App::DocumentObjectGroupPython] G4_In  # scripted group (container) (typed FeaturePython)
  Dunit = g/cm3
  Dvalue = 7.31
  Group = -> [In_element001]
  conduct = 2
  density = 1
  expand = 3
  formula = In
  name = G4_In
  specific = 4
FEATURE [App::DocumentObjectGroupPython] Sn_element001  label="Sn_element : 1"  # scripted group (container) (typed FeaturePython)
  n = 1
  ref = Sn_element
FEATURE [App::DocumentObjectGroupPython] G4_Sn  # scripted group (container) (typed FeaturePython)
  Dunit = g/cm3
  Dvalue = 7.31
  Group = -> [Sn_element001]
  conduct = 2
  density = 1
  expand = 3
  formula = Sn
  name = G4_Sn
  specific = 4
FEATURE [App::DocumentObjectGroupPython] Sb_element001  label="Sb_element : 1"  # scripted group (container) (typed FeaturePython)
  n = 1
  ref = Sb_element
FEATURE [App::DocumentObjectGroupPython] G4_Sb  # scripted group (container) (typed FeaturePython)
  Dunit = g/cm3
  Dvalue = 6.691
  Group = -> [Sb_element001]
  conduct = 2
  density = 1
  expand = 3
  formula = Sb
  name = G4_Sb
  specific = 4
FEATURE [App::DocumentObjectGroupPython] Te_element002  label="Te_element : 002"  # scripted group (container) (typed FeaturePython)
  n = 1
  ref = Te_element
FEATURE [App::DocumentObjectGroupPython] G4_Te  # scripted group (container) (typed FeaturePython)
  Dunit = g/cm3
  Dvalue = 6.24
  Group = -> [Te_element002]
  conduct = 2
  density = 1
  expand = 3
  formula = Te
  name = G4_Te
  specific = 4
FEATURE [App::DocumentObjectGroupPython] I_element010  label="I_element : 006"  # scripted group (container) (typed FeaturePython)
  n = 1
  ref = I_element
FEATURE [App::DocumentObjectGroupPython] G4_I  # scripted group (container) (typed FeaturePython)
  Dunit = g/cm3
  Dvalue = 4.93
  Group = -> [I_element010]
  conduct = 2
  density = 1
  expand = 3
  formula = I
  name = G4_I
  specific = 4
FEATURE [App::DocumentObjectGroupPython] Xe_element001  label="Xe_element : 1"  # scripted group (container) (typed FeaturePython)
  n = 1
  ref = Xe_element
FEATURE [App::DocumentObjectGroupPython] G4_Xe  # scripted group (container) (typed FeaturePython)
  Dunit = g/cm3
  Dvalue = 0.00548536
  Group = -> [Xe_element001]
  conduct = 2
  density = 1
  expand = 3
  formula = Xe
  name = G4_Xe
  specific = 4
FEATURE [App::DocumentObjectGroupPython] Cs_element003  label="Cs_element : 003"  # scripted group (container) (typed FeaturePython)
  n = 1
  ref = Cs_element
FEATURE [App::DocumentObjectGroupPython] G4_Cs  # scripted group (container) (typed FeaturePython)
  Dunit = g/cm3
  Dvalue = 1.873
  Group = -> [Cs_element003]
  conduct = 2
  density = 1
  expand = 3
  formula = Cs
  name = G4_Cs
  specific = 4
FEATURE [App::DocumentObjectGroupPython] Ba_element003  label="Ba_element : 003"  # scripted group (container) (typed FeaturePython)
  n = 1
  ref = Ba_element
FEATURE [App::DocumentObjectGroupPython] G4_Ba  # scripted group (container) (typed FeaturePython)
  Dunit = g/cm3
  Dvalue = 3.5
  Group = -> [Ba_element003]
  conduct = 2
  density = 1
  expand = 3
  formula = Ba
  name = G4_Ba
  specific = 4
FEATURE [App::DocumentObjectGroupPython] La_element003  label="La_element : 003"  # scripted group (container) (typed FeaturePython)
  n = 1
  ref = La_element
FEATURE [App::DocumentObjectGroupPython] G4_La  # scripted group (container) (typed FeaturePython)
  Dunit = g/cm3
  Dvalue = 6.154
  Group = -> [La_element003]
  conduct = 2
  density = 1
  expand = 3
  formula = La
  name = G4_La
  specific = 4
FEATURE [App::DocumentObjectGroupPython] Ce_element002  label="Ce_element : 1"  # scripted group (container) (typed FeaturePython)
  n = 1
  ref = Ce_element
FEATURE [App::DocumentObjectGroupPython] G4_Ce  # scripted group (container) (typed FeaturePython)
  Dunit = g/cm3
  Dvalue = 6.657
  Group = -> [Ce_element002]
  conduct = 2
  density = 1
  expand = 3
  formula = Ce
  name = G4_Ce
  specific = 4
FEATURE [App::DocumentObjectGroupPython] Pr_element001  label="Pr_element : 1"  # scripted group (container) (typed FeaturePython)
  n = 1
  ref = Pr_element
FEATURE [App::DocumentObjectGroupPython] G4_Pr  # scripted group (container) (typed FeaturePython)
  Dunit = g/cm3
  Dvalue = 6.71
  Group = -> [Pr_element001]
  conduct = 2
  density = 1
  expand = 3
  formula = Pr
  name = G4_Pr
  specific = 4
FEATURE [App::DocumentObjectGroupPython] Nd_element001  label="Nd_element : 1"  # scripted group (container) (typed FeaturePython)
  n = 1
  ref = Nd_element
FEATURE [App::DocumentObjectGroupPython] G4_Nd  # scripted group (container) (typed FeaturePython)
  Dunit = g/cm3
  Dvalue = 6.9
  Group = -> [Nd_element001]
  conduct = 2
  density = 1
  expand = 3
  formula = Nd
  name = G4_Nd
  specific = 4
FEATURE [App::DocumentObjectGroupPython] Pm_element001  label="Pm_element : 1"  # scripted group (container) (typed FeaturePython)
  n = 1
  ref = Pm_element
FEATURE [App::DocumentObjectGroupPython] G4_Pm  # scripted group (container) (typed FeaturePython)
  Dunit = g/cm3
  Dvalue = 7.22
  Group = -> [Pm_element001]
  conduct = 2
  density = 1
  expand = 3
  formula = Pm
  name = G4_Pm
  specific = 4
FEATURE [App::DocumentObjectGroupPython] Sm_element001  label="Sm_element : 1"  # scripted group (container) (typed FeaturePython)
  n = 1
  ref = Sm_element
FEATURE [App::DocumentObjectGroupPython] G4_Sm  # scripted group (container) (typed FeaturePython)
  Dunit = g/cm3
  Dvalue = 7.46
  Group = -> [Sm_element001]
  conduct = 2
  density = 1
  expand = 3
  formula = Sm
  name = G4_Sm
  specific = 4
FEATURE [App::DocumentObjectGroupPython] Eu_element001  label="Eu_element : 1"  # scripted group (container) (typed FeaturePython)
  n = 1
  ref = Eu_element
FEATURE [App::DocumentObjectGroupPython] G4_Eu  # scripted group (container) (typed FeaturePython)
  Dunit = g/cm3
  Dvalue = 5.243
  Group = -> [Eu_element001]
  conduct = 2
  density = 1
  expand = 3
  formula = Eu
  name = G4_Eu
  specific = 4
FEATURE [App::DocumentObjectGroupPython] Gd_element002  label="Gd_element : 1"  # scripted group (container) (typed FeaturePython)
  n = 1
  ref = Gd_element
FEATURE [App::DocumentObjectGroupPython] G4_Gd  # scripted group (container) (typed FeaturePython)
  Dunit = g/cm3
  Dvalue = 7.9004
  Group = -> [Gd_element002]
  conduct = 2
  density = 1
  expand = 3
  formula = Gd
  name = G4_Gd
  specific = 4
FEATURE [App::DocumentObjectGroupPython] Tb_element001  label="Tb_element : 1"  # scripted group (container) (typed FeaturePython)
  n = 1
  ref = Tb_element
FEATURE [App::DocumentObjectGroupPython] G4_Tb  # scripted group (container) (typed FeaturePython)
  Dunit = g/cm3
  Dvalue = 8.229
  Group = -> [Tb_element001]
  conduct = 2
  density = 1
  expand = 3
  formula = Tb
  name = G4_Tb
  specific = 4
FEATURE [App::DocumentObjectGroupPython] Dy_element001  label="Dy_element : 1"  # scripted group (container) (typed FeaturePython)
  n = 1
  ref = Dy_element
FEATURE [App::DocumentObjectGroupPython] G4_Dy  # scripted group (container) (typed FeaturePython)
  Dunit = g/cm3
  Dvalue = 8.55
  Group = -> [Dy_element001]
  conduct = 2
  density = 1
  expand = 3
  formula = Dy
  name = G4_Dy
  specific = 4
FEATURE [App::DocumentObjectGroupPython] Ho_element001  label="Ho_element : 1"  # scripted group (container) (typed FeaturePython)
  n = 1
  ref = Ho_element
FEATURE [App::DocumentObjectGroupPython] G4_Ho  # scripted group (container) (typed FeaturePython)
  Dunit = g/cm3
  Dvalue = 8.795
  Group = -> [Ho_element001]
  conduct = 2
  density = 1
  expand = 3
  formula = Ho
  name = G4_Ho
  specific = 4
FEATURE [App::DocumentObjectGroupPython] Er_element001  label="Er_element : 1"  # scripted group (container) (typed FeaturePython)
  n = 1
  ref = Er_element
FEATURE [App::DocumentObjectGroupPython] G4_Er  # scripted group (container) (typed FeaturePython)
  Dunit = g/cm3
  Dvalue = 9.066
  Group = -> [Er_element001]
  conduct = 2
  density = 1
  expand = 3
  formula = Er
  name = G4_Er
  specific = 4
FEATURE [App::DocumentObjectGroupPython] Tm_element001  label="Tm_element : 1"  # scripted group (container) (typed FeaturePython)
  n = 1
  ref = Tm_element
FEATURE [App::DocumentObjectGroupPython] G4_Tm  # scripted group (container) (typed FeaturePython)
  Dunit = g/cm3
  Dvalue = 9.321
  Group = -> [Tm_element001]
  conduct = 2
  density = 1
  expand = 3
  formula = Tm
  name = G4_Tm
  specific = 4
FEATURE [App::DocumentObjectGroupPython] Yb_element001  label="Yb_element : 1"  # scripted group (container) (typed FeaturePython)
  n = 1
  ref = Yb_element
FEATURE [App::DocumentObjectGroupPython] G4_Yb  # scripted group (container) (typed FeaturePython)
  Dunit = g/cm3
  Dvalue = 6.73
  Group = -> [Yb_element001]
  conduct = 2
  density = 1
  expand = 3
  formula = Yb
  name = G4_Yb
  specific = 4
FEATURE [App::DocumentObjectGroupPython] Lu_element001  label="Lu_element : 1"  # scripted group (container) (typed FeaturePython)
  n = 1
  ref = Lu_element
FEATURE [App::DocumentObjectGroupPython] G4_Lu  # scripted group (container) (typed FeaturePython)
  Dunit = g/cm3
  Dvalue = 9.84
  Group = -> [Lu_element001]
  conduct = 2
  density = 1
  expand = 3
  formula = Lu
  name = G4_Lu
  specific = 4
FEATURE [App::DocumentObjectGroupPython] Hf_element001  label="Hf_element : 1"  # scripted group (container) (typed FeaturePython)
  n = 1
  ref = Hf_element
FEATURE [App::DocumentObjectGroupPython] G4_Hf  # scripted group (container) (typed FeaturePython)
  Dunit = g/cm3
  Dvalue = 13.31
  Group = -> [Hf_element001]
  conduct = 2
  density = 1
  expand = 3
  formula = Hf
  name = G4_Hf
  specific = 4
FEATURE [App::DocumentObjectGroupPython] Ta_element001  label="Ta_element : 1"  # scripted group (container) (typed FeaturePython)
  n = 1
  ref = Ta_element
FEATURE [App::DocumentObjectGroupPython] G4_Ta  # scripted group (container) (typed FeaturePython)
  Dunit = g/cm3
  Dvalue = 16.654
  Group = -> [Ta_element001]
  conduct = 2
  density = 1
  expand = 3
  formula = Ta
  name = G4_Ta
  specific = 4
FEATURE [App::DocumentObjectGroupPython] W_element004  label="W_element : 004"  # scripted group (container) (typed FeaturePython)
  n = 1
  ref = W_element
FEATURE [App::DocumentObjectGroupPython] G4_W  # scripted group (container) (typed FeaturePython)
  Dunit = g/cm3
  Dvalue = 19.3
  Group = -> [W_element004]
  conduct = 2
  density = 1
  expand = 3
  formula = W
  name = G4_W
  specific = 4
FEATURE [App::DocumentObjectGroupPython] Re_element001  label="Re_element : 1"  # scripted group (container) (typed FeaturePython)
  n = 1
  ref = Re_element
FEATURE [App::DocumentObjectGroupPython] G4_Re  # scripted group (container) (typed FeaturePython)
  Dunit = g/cm3
  Dvalue = 21.02
  Group = -> [Re_element001]
  conduct = 2
  density = 1
  expand = 3
  formula = Re
  name = G4_Re
  specific = 4
FEATURE [App::DocumentObjectGroupPython] Os_element001  label="Os_element : 1"  # scripted group (container) (typed FeaturePython)
  n = 1
  ref = Os_element
FEATURE [App::DocumentObjectGroupPython] G4_Os  # scripted group (container) (typed FeaturePython)
  Dunit = g/cm3
  Dvalue = 22.57
  Group = -> [Os_element001]
  conduct = 2
  density = 1
  expand = 3
  formula = Os
  name = G4_Os
  specific = 4
FEATURE [App::DocumentObjectGroupPython] Ir_element001  label="Ir_element : 1"  # scripted group (container) (typed FeaturePython)
  n = 1
  ref = Ir_element
FEATURE [App::DocumentObjectGroupPython] G4_Ir  # scripted group (container) (typed FeaturePython)
  Dunit = g/cm3
  Dvalue = 22.42
  Group = -> [Ir_element001]
  conduct = 2
  density = 1
  expand = 3
  formula = Ir
  name = G4_Ir
  specific = 4
FEATURE [App::DocumentObjectGroupPython] Pt_element001  label="Pt_element : 1"  # scripted group (container) (typed FeaturePython)
  n = 1
  ref = Pt_element
FEATURE [App::DocumentObjectGroupPython] G4_Pt  # scripted group (container) (typed FeaturePython)
  Dunit = g/cm3
  Dvalue = 21.45
  Group = -> [Pt_element001]
  conduct = 2
  density = 1
  expand = 3
  formula = Pt
  name = G4_Pt
  specific = 4
FEATURE [App::DocumentObjectGroupPython] Au_element001  label="Au_element : 1"  # scripted group (container) (typed FeaturePython)
  n = 1
  ref = Au_element
FEATURE [App::DocumentObjectGroupPython] G4_Au  # scripted group (container) (typed FeaturePython)
  Dunit = g/cm3
  Dvalue = 19.32
  Group = -> [Au_element001]
  conduct = 2
  density = 1
  expand = 3
  formula = Au
  name = G4_Au
  specific = 4
FEATURE [App::DocumentObjectGroupPython] Hg_element002  label="Hg_element : 002"  # scripted group (container) (typed FeaturePython)
  n = 1
  ref = Hg_element
FEATURE [App::DocumentObjectGroupPython] G4_Hg  # scripted group (container) (typed FeaturePython)
  Dunit = g/cm3
  Dvalue = 13.546
  Group = -> [Hg_element002]
  conduct = 2
  density = 1
  expand = 3
  formula = Hg
  name = G4_Hg
  specific = 4
FEATURE [App::DocumentObjectGroupPython] Tl_element002  label="Tl_element : 002"  # scripted group (container) (typed FeaturePython)
  n = 1
  ref = Tl_element
FEATURE [App::DocumentObjectGroupPython] G4_Tl  # scripted group (container) (typed FeaturePython)
  Dunit = g/cm3
  Dvalue = 11.72
  Group = -> [Tl_element002]
  conduct = 2
  density = 1
  expand = 3
  formula = Tl
  name = G4_Tl
  specific = 4
FEATURE [App::DocumentObjectGroupPython] Pb_element003  label="Pb_element : 1"  # scripted group (container) (typed FeaturePython)
  n = 1
  ref = Pb_element
FEATURE [App::DocumentObjectGroupPython] G4_Pb  # scripted group (container) (typed FeaturePython)
  Dunit = g/cm3
  Dvalue = 11.35
  Group = -> [Pb_element003]
  conduct = 2
  density = 1
  expand = 3
  formula = Pb
  name = G4_Pb
  specific = 4
FEATURE [App::DocumentObjectGroupPython] Bi_element002  label="Bi_element : 1"  # scripted group (container) (typed FeaturePython)
  n = 1
  ref = Bi_element
FEATURE [App::DocumentObjectGroupPython] G4_Bi  # scripted group (container) (typed FeaturePython)
  Dunit = g/cm3
  Dvalue = 9.747
  Group = -> [Bi_element002]
  conduct = 2
  density = 1
  expand = 3
  formula = Bi
  name = G4_Bi
  specific = 4
FEATURE [App::DocumentObjectGroupPython] Po_element001  label="Po_element : 1"  # scripted group (container) (typed FeaturePython)
  n = 1
  ref = Po_element
FEATURE [App::DocumentObjectGroupPython] G4_Po  # scripted group (container) (typed FeaturePython)
  Dunit = g/cm3
  Dvalue = 9.32
  Group = -> [Po_element001]
  conduct = 2
  density = 1
  expand = 3
  formula = Po
  name = G4_Po
  specific = 4
FEATURE [App::DocumentObjectGroupPython] At_element001  label="At_element : 1"  # scripted group (container) (typed FeaturePython)
  n = 1
  ref = At_element
FEATURE [App::DocumentObjectGroupPython] G4_At  # scripted group (container) (typed FeaturePython)
  Dunit = g/cm3
  Dvalue = 9.32
  Group = -> [At_element001]
  conduct = 2
  density = 1
  expand = 3
  formula = At
  name = G4_At
  specific = 4
FEATURE [App::DocumentObjectGroupPython] Rn_element001  label="Rn_element : 1"  # scripted group (container) (typed FeaturePython)
  n = 1
  ref = Rn_element
FEATURE [App::DocumentObjectGroupPython] G4_Rn  # scripted group (container) (typed FeaturePython)
  Dunit = g/cm3
  Dvalue = 0.00900662
  Group = -> [Rn_element001]
  conduct = 2
  density = 1
  expand = 3
  formula = Rn
  name = G4_Rn
  specific = 4
FEATURE [App::DocumentObjectGroupPython] Fr_element001  label="Fr_element : 1"  # scripted group (container) (typed FeaturePython)
  n = 1
  ref = Fr_element
FEATURE [App::DocumentObjectGroupPython] G4_Fr  # scripted group (container) (typed FeaturePython)
  Dunit = g/cm3
  Dvalue = 1
  Group = -> [Fr_element001]
  conduct = 2
  density = 1
  expand = 3
  formula = Fr
  name = G4_Fr
  specific = 4
FEATURE [App::DocumentObjectGroupPython] Ra_element001  label="Ra_element : 1"  # scripted group (container) (typed FeaturePython)
  n = 1
  ref = Ra_element
FEATURE [App::DocumentObjectGroupPython] G4_Ra  # scripted group (container) (typed FeaturePython)
  Dunit = g/cm3
  Dvalue = 5
  Group = -> [Ra_element001]
  conduct = 2
  density = 1
  expand = 3
  formula = Ra
  name = G4_Ra
  specific = 4
FEATURE [App::DocumentObjectGroupPython] Ac_element001  label="Ac_element : 1"  # scripted group (container) (typed FeaturePython)
  n = 1
  ref = Ac_element
FEATURE [App::DocumentObjectGroupPython] G4_Ac  # scripted group (container) (typed FeaturePython)
  Dunit = g/cm3
  Dvalue = 10.07
  Group = -> [Ac_element001]
  conduct = 2
  density = 1
  expand = 3
  formula = Ac
  name = G4_Ac
  specific = 4
FEATURE [App::DocumentObjectGroupPython] Th_element001  label="Th_element : 1"  # scripted group (container) (typed FeaturePython)
  n = 1
  ref = Th_element
FEATURE [App::DocumentObjectGroupPython] G4_Th  # scripted group (container) (typed FeaturePython)
  Dunit = g/cm3
  Dvalue = 11.72
  Group = -> [Th_element001]
  conduct = 2
  density = 1
  expand = 3
  formula = Th
  name = G4_Th
  specific = 4
FEATURE [App::DocumentObjectGroupPython] Pa_element001  label="Pa_element : 1"  # scripted group (container) (typed FeaturePython)
  n = 1
  ref = Pa_element
FEATURE [App::DocumentObjectGroupPython] G4_Pa  # scripted group (container) (typed FeaturePython)
  Dunit = g/cm3
  Dvalue = 15.37
  Group = -> [Pa_element001]
  conduct = 2
  density = 1
  expand = 3
  formula = Pa
  name = G4_Pa
  specific = 4
FEATURE [App::DocumentObjectGroupPython] U_element004  label="U_element : 004"  # scripted group (container) (typed FeaturePython)
  n = 1
  ref = U_element
FEATURE [App::DocumentObjectGroupPython] G4_U  # scripted group (container) (typed FeaturePython)
  Dunit = g/cm3
  Dvalue = 18.95
  Group = -> [U_element004]
  conduct = 2
  density = 1
  expand = 3
  formula = U
  name = G4_U
  specific = 4
FEATURE [App::DocumentObjectGroupPython] Np_element001  label="Np_element : 1"  # scripted group (container) (typed FeaturePython)
  n = 1
  ref = Np_element
FEATURE [App::DocumentObjectGroupPython] G4_Np  # scripted group (container) (typed FeaturePython)
  Dunit = g/cm3
  Dvalue = 20.25
  Group = -> [Np_element001]
  conduct = 2
  density = 1
  expand = 3
  formula = Np
  name = G4_Np
  specific = 4
FEATURE [App::DocumentObjectGroupPython] Pu_element002  label="Pu_element : 002"  # scripted group (container) (typed FeaturePython)
  n = 1
  ref = Pu_element
FEATURE [App::DocumentObjectGroupPython] G4_Pu  # scripted group (container) (typed FeaturePython)
  Dunit = g/cm3
  Dvalue = 19.84
  Group = -> [Pu_element002]
  conduct = 2
  density = 1
  expand = 3
  formula = Pu
  name = G4_Pu
  specific = 4
FEATURE [App::DocumentObjectGroupPython] Am_element001  label="Am_element : 1"  # scripted group (container) (typed FeaturePython)
  n = 1
  ref = Am_element
FEATURE [App::DocumentObjectGroupPython] G4_Am  # scripted group (container) (typed FeaturePython)
  Dunit = g/cm3
  Dvalue = 13.67
  Group = -> [Am_element001]
  conduct = 2
  density = 1
  expand = 3
  formula = Am
  name = G4_Am
  specific = 4
FEATURE [App::DocumentObjectGroupPython] Cm_element001  label="Cm_element : 1"  # scripted group (container) (typed FeaturePython)
  n = 1
  ref = Cm_element
FEATURE [App::DocumentObjectGroupPython] G4_Cm  # scripted group (container) (typed FeaturePython)
  Dunit = g/cm3
  Dvalue = 13.51
  Group = -> [Cm_element001]
  conduct = 2
  density = 1
  expand = 3
  formula = Cm
  name = G4_Cm
  specific = 4
FEATURE [App::DocumentObjectGroupPython] Bk_element001  label="Bk_element : 1"  # scripted group (container) (typed FeaturePython)
  n = 1
  ref = Bk_element
FEATURE [App::DocumentObjectGroupPython] G4_Bk  # scripted group (container) (typed FeaturePython)
  Dunit = g/cm3
  Dvalue = 14
  Group = -> [Bk_element001]
  conduct = 2
  density = 1
  expand = 3
  formula = Bk
  name = G4_Bk
  specific = 4
FEATURE [App::DocumentObjectGroupPython] Cf_element001  label="Cf_element : 1"  # scripted group (container) (typed FeaturePython)
  n = 1
  ref = Cf_element
FEATURE [App::DocumentObjectGroupPython] G4_Cf  # scripted group (container) (typed FeaturePython)
  Dunit = g/cm3
  Dvalue = 10
  Group = -> [Cf_element001]
  conduct = 2
  density = 1
  expand = 3
  formula = Cf
  name = G4_Cf
  specific = 4
FEATURE [App::DocumentObjectGroupPython] Element  # scripted group (container) (typed FeaturePython)
  Group = -> [G4_H,G4_He,G4_Li,G4_Be,G4_B,G4_C,G4_N,G4_O,G4_F,G4_Ne,G4_Na,G4_Mg,G4_Al,G4_Si,G4_P,G4_S,G4_Cl,G4_Ar,G4_K,G4_Ca,G4_Sc,G4_Ti,G4_V,G4_Cr,G4_Mn,G4_Fe,G4_Co,G4_Ni,G4_Cu,G4_Zn,G4_Ga,G4_Ge,G4_As,G4_Se,G4_Br,G4_Kr,G4_Rb,G4_Sr,G4_Y,G4_Zr,G4_Nb,G4_Mo,G4_Tc,G4_Ru,G4_Rh,G4_Pd,G4_Ag,G4_Cd,G4_In,G4_Sn,G4_Sb,G4_Te,G4_I,G4_Xe,G4_Cs,G4_Ba,G4_La,G4_Ce,G4_Pr,G4_Nd,G4_Pm,G4_Sm,G4_Eu,G4_Gd,G4_Tb,G4_Dy,G4_Ho,G4_Er,+30 more]
FEATURE [App::DocumentObjectGroupPython] H_element114  label="H_element : 063"  # scripted group (container) (typed FeaturePython)
  n = 2
  ref = H_element
FEATURE [App::DocumentObjectGroupPython] G4_lH2  # scripted group (container) (typed FeaturePython)
  Dunit = g/cm3
  Dvalue = 0.0708
  Group = -> [H_element114]
  conduct = 2
  density = 1
  expand = 3
  formula = G4_lH2
  name = G4_lH2
  specific = 4
FEATURE [App::DocumentObjectGroupPython] N_element049  label="N_element : 022"  # scripted group (container) (typed FeaturePython)
  n = 2
  ref = N_element
FEATURE [App::DocumentObjectGroupPython] G4_lN2  # scripted group (container) (typed FeaturePython)
  Dunit = g/cm3
  Dvalue = 0.807
  Group = -> [N_element049]
  conduct = 2
  density = 1
  expand = 3
  formula = G4_lN2
  name = G4_lN2
  specific = 4
FEATURE [App::DocumentObjectGroupPython] O_element106  label="O_element : 060"  # scripted group (container) (typed FeaturePython)
  n = 2
  ref = O_element
FEATURE [App::DocumentObjectGroupPython] G4_lO2  # scripted group (container) (typed FeaturePython)
  Dunit = g/cm3
  Dvalue = 1.141
  Group = -> [O_element106]
  conduct = 2
  density = 1
  expand = 3
  formula = G4_lO2
  name = G4_lO2
  specific = 4
FEATURE [App::DocumentObjectGroupPython] Ar  label="Ar : 1"  # scripted group (container) (typed FeaturePython)
  n = 1
  ref = Ar
FEATURE [App::DocumentObjectGroupPython] G4_lAr  # scripted group (container) (typed FeaturePython)
  Dunit = g/cm3
  Dvalue = 1.396
  Group = -> [Ar]
  conduct = 2
  density = 1
  expand = 3
  formula = G4_lAr
  name = G4_lAr
  specific = 4
FEATURE [App::DocumentObjectGroupPython] Br  label="Br : 1"  # scripted group (container) (typed FeaturePython)
  n = 1
  ref = Br
FEATURE [App::DocumentObjectGroupPython] G4_lBr  # scripted group (container) (typed FeaturePython)
  Dunit = g/cm3
  Dvalue = 3.1028
  Group = -> [Br]
  conduct = 2
  density = 1
  expand = 3
  formula = G4_lBr
  name = G4_lBr
  specific = 4
FEATURE [App::DocumentObjectGroupPython] Kr  label="Kr : 1"  # scripted group (container) (typed FeaturePython)
  n = 1
  ref = Kr
FEATURE [App::DocumentObjectGroupPython] G4_lKr  # scripted group (container) (typed FeaturePython)
  Dunit = g/cm3
  Dvalue = 2.418
  Group = -> [Kr]
  conduct = 2
  density = 1
  expand = 3
  formula = G4_lKr
  name = G4_lKr
  specific = 4
FEATURE [App::DocumentObjectGroupPython] Xe  label="Xe : 1"  # scripted group (container) (typed FeaturePython)
  n = 1
  ref = Xe
FEATURE [App::DocumentObjectGroupPython] G4_lXe  # scripted group (container) (typed FeaturePython)
  Dunit = g/cm3
  Dvalue = 2.953
  Group = -> [Xe]
  conduct = 2
  density = 1
  expand = 3
  formula = G4_lXe
  name = G4_lXe
  specific = 4
FEATURE [App::DocumentObjectGroupPython] O_element107  label="O_element : 061"  # scripted group (container) (typed FeaturePython)
  n = 4
  ref = O_element
FEATURE [App::DocumentObjectGroupPython] Pb_element004  label="Pb_element : 002"  # scripted group (container) (typed FeaturePython)
  n = 1
  ref = Pb_element
FEATURE [App::DocumentObjectGroupPython] W_element005  label="W_element : 005"  # scripted group (container) (typed FeaturePython)
  n = 1
  ref = W_element
FEATURE [App::DocumentObjectGroupPython] G4_PbWO4  # scripted group (container) (typed FeaturePython)
  Dunit = g/cm3
  Dvalue = 8.28
  Group = -> [O_element107,Pb_element004,W_element005]
  conduct = 2
  density = 1
  expand = 3
  formula = G4_PbWO4
  name = G4_PbWO4
  specific = 4
FEATURE [App::DocumentObjectGroupPython] alactic  label="alactic : 1"  # scripted group (container) (typed FeaturePython)
  n = 1
  ref = alactic
FEATURE [App::DocumentObjectGroupPython] G4_Galactic  # scripted group (container) (typed FeaturePython)
  Dunit = g/cm3
  Dvalue = 0
  Group = -> [alactic]
  conduct = 2
  density = 1
  expand = 3
  formula = G4_Galactic
  name = G4_Galactic
  specific = 4
FEATURE [App::DocumentObjectGroupPython] RAPHITE_POROUS  label="RAPHITE_POROUS : 1"  # scripted group (container) (typed FeaturePython)
  n = 1
  ref = RAPHITE_POROUS
FEATURE [App::DocumentObjectGroupPython] G4_GRAPHITE_POROUS  # scripted group (container) (typed FeaturePython)
  Dunit = g/cm3
  Dvalue = 1.7
  Group = -> [RAPHITE_POROUS]
  conduct = 2
  density = 1
  expand = 3
  formula = G4_GRAPHITE_POROUS
  name = G4_GRAPHITE_POROUS
  specific = 4
FEATURE [App::DocumentObjectGroupPython] H_element115  label="H_element : 0.150"  # scripted group (container) (typed FeaturePython)
  n = 0.080538
FEATURE [App::DocumentObjectGroupPython] C_element125  label="C_element : 0.600"  # scripted group (container) (typed FeaturePython)
  n = 0.599848
FEATURE [App::DocumentObjectGroupPython] O_element108  label="O_element : 0.320"  # scripted group (container) (typed FeaturePython)
  n = 0.319614
FEATURE [App::DocumentObjectGroupPython] G4_LUCITE  # scripted group (container) (typed FeaturePython)
  Dunit = g/cm3
  Dvalue = 1.19
  Group = -> [H_element115,C_element125,O_element108]
  conduct = 2
  density = 1
  expand = 3
  formula = G4_LUCITE
  name = G4_LUCITE
  specific = 4
FEATURE [App::DocumentObjectGroupPython] Cu_element002  label="Cu_element : 62"  # scripted group (container) (typed FeaturePython)
  n = 62
  ref = Cu_element
FEATURE [App::DocumentObjectGroupPython] Zn_element002  label="Zn_element : 35"  # scripted group (container) (typed FeaturePython)
  n = 35
  ref = Zn_element
FEATURE [App::DocumentObjectGroupPython] Pb_element005  label="Pb_element : 3"  # scripted group (container) (typed FeaturePython)
  n = 3
  ref = Pb_element
FEATURE [App::DocumentObjectGroupPython] G4_BRASS  # scripted group (container) (typed FeaturePython)
  Dunit = g/cm3
  Dvalue = 8.52
  Group = -> [Cu_element002,Zn_element002,Pb_element005]
  conduct = 2
  density = 1
  expand = 3
  formula = G4_BRASS
  name = G4_BRASS
  specific = 4
FEATURE [App::DocumentObjectGroupPython] Cu_element003  label="Cu_element : 89"  # scripted group (container) (typed FeaturePython)
  n = 89
  ref = Cu_element
FEATURE [App::DocumentObjectGroupPython] Zn_element003  label="Zn_element : 9"  # scripted group (container) (typed FeaturePython)
  n = 9
  ref = Zn_element
FEATURE [App::DocumentObjectGroupPython] Pb_element006  label="Pb_element : 2"  # scripted group (container) (typed FeaturePython)
  n = 2
  ref = Pb_element
FEATURE [App::DocumentObjectGroupPython] G4_BRONZE  # scripted group (container) (typed FeaturePython)
  Dunit = g/cm3
  Dvalue = 8.82
  Group = -> [Cu_element003,Zn_element003,Pb_element006]
  conduct = 2
  density = 1
  expand = 3
  formula = G4_BRONZE
  name = G4_BRONZE
  specific = 4
FEATURE [App::DocumentObjectGroupPython] Fe_element008  label="Fe_element : 74"  # scripted group (container) (typed FeaturePython)
  n = 74
  ref = Fe_element
FEATURE [App::DocumentObjectGroupPython] Cr_element002  label="Cr_element : 18"  # scripted group (container) (typed FeaturePython)
  n = 18
  ref = Cr_element
FEATURE [App::DocumentObjectGroupPython] Ni_element002  label="Ni_element : 8"  # scripted group (container) (typed FeaturePython)
  n = 8
  ref = Ni_element
FEATURE [App::DocumentObjectGroupPython] G4_STAINLESS_STEEL  label="G4_STAINLESS-STEEL"  # scripted group (container) (typed FeaturePython)
  Dunit = g/cm3
  Dvalue = 8
  Group = -> [Fe_element008,Cr_element002,Ni_element002]
  conduct = 2
  density = 1
  expand = 3
  formula = G4_STAINLESS-STEEL
  name = G4_STAINLESS-STEEL
  specific = 4
FEATURE [App::DocumentObjectGroupPython] H_element116  label="H_element : 064"  # scripted group (container) (typed FeaturePython)
  n = 18
  ref = H_element
FEATURE [App::DocumentObjectGroupPython] C_element126  label="C_element : 071"  # scripted group (container) (typed FeaturePython)
  n = 12
  ref = C_element
FEATURE [App::DocumentObjectGroupPython] O_element109  label="O_element : 062"  # scripted group (container) (typed FeaturePython)
  n = 7
  ref = O_element
FEATURE [App::DocumentObjectGroupPython] G4_CR39  # scripted group (container) (typed FeaturePython)
  Dunit = g/cm3
  Dvalue = 1.32
  Group = -> [H_element116,C_element126,O_element109]
  conduct = 2
  density = 1
  expand = 3
  formula = G4_CR39
  name = G4_CR39
  specific = 4
FEATURE [App::DocumentObjectGroupPython] H_element117  label="H_element : 38"  # scripted group (container) (typed FeaturePython)
  n = 38
  ref = H_element
FEATURE [App::DocumentObjectGroupPython] C_element127  label="C_element : 072"  # scripted group (container) (typed FeaturePython)
  n = 18
  ref = C_element
FEATURE [App::DocumentObjectGroupPython] O_element110  label="O_element : 063"  # scripted group (container) (typed FeaturePython)
  n = 1
  ref = O_element
FEATURE [App::DocumentObjectGroupPython] G4_OCTADECANOL  # scripted group (container) (typed FeaturePython)
  Dunit = g/cm3
  Dvalue = 0.812
  Group = -> [H_element117,C_element127,O_element110]
  conduct = 2
  density = 1
  expand = 3
  formula = G4_OCTADECANOL
  name = G4_OCTADECANOL
  specific = 4
FEATURE [App::DocumentObjectGroupPython] HEP  # scripted group (container) (typed FeaturePython)
  Group = -> [G4_lH2,G4_lN2,G4_lO2,G4_lAr,G4_lBr,G4_lKr,G4_lXe,G4_PbWO4,G4_Galactic,G4_GRAPHITE_POROUS,G4_LUCITE,G4_BRASS,G4_BRONZE,G4_STAINLESS_STEEL,G4_CR39,G4_OCTADECANOL]
FEATURE [App::DocumentObjectGroupPython] C_element128  label="C_element : 073"  # scripted group (container) (typed FeaturePython)
  n = 14
  ref = C_element
FEATURE [App::DocumentObjectGroupPython] H_element118  label="H_element : 065"  # scripted group (container) (typed FeaturePython)
  n = 10
  ref = H_element
FEATURE [App::DocumentObjectGroupPython] O_element111  label="O_element : 064"  # scripted group (container) (typed FeaturePython)
  n = 2
  ref = O_element
FEATURE [App::DocumentObjectGroupPython] N_element050  label="N_element : 023"  # scripted group (container) (typed FeaturePython)
  n = 2
  ref = N_element
FEATURE [App::DocumentObjectGroupPython] G4_KEVLAR  # scripted group (container) (typed FeaturePython)
  Dunit = g/cm3
  Dvalue = 1.44
  Group = -> [C_element128,H_element118,O_element111,N_element050]
  conduct = 2
  density = 1
  expand = 3
  formula = G4_KEVLAR
  name = G4_KEVLAR
  specific = 4
FEATURE [App::DocumentObjectGroupPython] C_element129  label="C_element : 074"  # scripted group (container) (typed FeaturePython)
  n = 10
  ref = C_element
FEATURE [App::DocumentObjectGroupPython] H_element119  label="H_element : 066"  # scripted group (container) (typed FeaturePython)
  n = 8
  ref = H_element
FEATURE [App::DocumentObjectGroupPython] O_element112  label="O_element : 065"  # scripted group (container) (typed FeaturePython)
  n = 4
  ref = O_element
FEATURE [App::DocumentObjectGroupPython] G4_DACRON  # scripted group (container) (typed FeaturePython)
  Dunit = g/cm3
  Dvalue = 1.4
  Group = -> [C_element129,H_element119,O_element112]
  conduct = 2
  density = 1
  expand = 3
  formula = G4_DACRON
  name = G4_DACRON
  specific = 4
FEATURE [App::DocumentObjectGroupPython] C_element130  label="C_element : 075"  # scripted group (container) (typed FeaturePython)
  n = 4
  ref = C_element
FEATURE [App::DocumentObjectGroupPython] H_element120  label="H_element : 067"  # scripted group (container) (typed FeaturePython)
  n = 5
  ref = H_element
FEATURE [App::DocumentObjectGroupPython] Cl_element030  label="Cl_element : 016"  # scripted group (container) (typed FeaturePython)
  n = 1
  ref = Cl_element
FEATURE [App::DocumentObjectGroupPython] G4_NEOPRENE  # scripted group (container) (typed FeaturePython)
  Dunit = g/cm3
  Dvalue = 1.23
  Group = -> [C_element130,H_element120,Cl_element030]
  conduct = 2
  density = 1
  expand = 3
  formula = G4_NEOPRENE
  name = G4_NEOPRENE
  specific = 4
FEATURE [App::DocumentObjectGroupPython] Space  # scripted group (container) (typed FeaturePython)
  Group = -> [G4_KEVLAR,G4_DACRON,G4_NEOPRENE]
FEATURE [App::DocumentObjectGroupPython] H_element121  label="H_element : 068"  # scripted group (container) (typed FeaturePython)
  n = 5
  ref = H_element
FEATURE [App::DocumentObjectGroupPython] C_element131  label="C_element : 076"  # scripted group (container) (typed FeaturePython)
  n = 4
  ref = C_element
FEATURE [App::DocumentObjectGroupPython] N_element051  label="N_element : 3"  # scripted group (container) (typed FeaturePython)
  n = 3
  ref = N_element
FEATURE [App::DocumentObjectGroupPython] O_element113  label="O_element : 066"  # scripted group (container) (typed FeaturePython)
  n = 1
  ref = O_element
FEATURE [App::DocumentObjectGroupPython] G4_CYTOSINE  # scripted group (container) (typed FeaturePython)
  Dunit = g/cm3
  Dvalue = 1.55
  Group = -> [H_element121,C_element131,N_element051,O_element113]
  conduct = 2
  density = 1
  expand = 3
  formula = G4_CYTOSINE
  name = G4_CYTOSINE
  specific = 4
FEATURE [App::DocumentObjectGroupPython] H_element122  label="H_element : 069"  # scripted group (container) (typed FeaturePython)
  n = 6
  ref = H_element
FEATURE [App::DocumentObjectGroupPython] C_element132  label="C_element : 077"  # scripted group (container) (typed FeaturePython)
  n = 5
  ref = C_element
FEATURE [App::DocumentObjectGroupPython] N_element052  label="N_element : 024"  # scripted group (container) (typed FeaturePython)
  n = 2
  ref = N_element
FEATURE [App::DocumentObjectGroupPython] O_element114  label="O_element : 067"  # scripted group (container) (typed FeaturePython)
  n = 2
  ref = O_element
FEATURE [App::DocumentObjectGroupPython] G4_THYMINE  # scripted group (container) (typed FeaturePython)
  Dunit = g/cm3
  Dvalue = 1.23
  Group = -> [H_element122,C_element132,N_element052,O_element114]
  conduct = 2
  density = 1
  expand = 3
  formula = G4_THYMINE
  name = G4_THYMINE
  specific = 4
FEATURE [App::DocumentObjectGroupPython] H_element123  label="H_element : 070"  # scripted group (container) (typed FeaturePython)
  n = 4
  ref = H_element
FEATURE [App::DocumentObjectGroupPython] C_element133  label="C_element : 078"  # scripted group (container) (typed FeaturePython)
  n = 4
  ref = C_element
FEATURE [App::DocumentObjectGroupPython] N_element053  label="N_element : 025"  # scripted group (container) (typed FeaturePython)
  n = 2
  ref = N_element
FEATURE [App::DocumentObjectGroupPython] O_element115  label="O_element : 068"  # scripted group (container) (typed FeaturePython)
  n = 2
  ref = O_element
FEATURE [App::DocumentObjectGroupPython] G4_URACIL  # scripted group (container) (typed FeaturePython)
  Dunit = g/cm3
  Dvalue = 1.32
  Group = -> [H_element123,C_element133,N_element053,O_element115]
  conduct = 2
  density = 1
  expand = 3
  formula = G4_URACIL
  name = G4_URACIL
  specific = 4
FEATURE [App::DocumentObjectGroupPython] H_element124  label="H_element : 071"  # scripted group (container) (typed FeaturePython)
  n = 4
  ref = H_element
FEATURE [App::DocumentObjectGroupPython] C_element134  label="C_element : 079"  # scripted group (container) (typed FeaturePython)
  n = 5
  ref = C_element
FEATURE [App::DocumentObjectGroupPython] N_element054  label="N_element : 026"  # scripted group (container) (typed FeaturePython)
  n = 5
  ref = N_element
FEATURE [App::DocumentObjectGroupPython] G4_DNA_ADENINE  # scripted group (container) (typed FeaturePython)
  Dunit = g/cm3
  Dvalue = 1
  Group = -> [H_element124,C_element134,N_element054]
  conduct = 2
  density = 1
  expand = 3
  formula = G4_DNA_ADENINE
  name = G4_DNA_ADENINE
  specific = 4
FEATURE [App::DocumentObjectGroupPython] H_element125  label="H_element : 072"  # scripted group (container) (typed FeaturePython)
  n = 4
  ref = H_element
FEATURE [App::DocumentObjectGroupPython] C_element135  label="C_element : 080"  # scripted group (container) (typed FeaturePython)
  n = 5
  ref = C_element
FEATURE [App::DocumentObjectGroupPython] N_element055  label="N_element : 027"  # scripted group (container) (typed FeaturePython)
  n = 5
  ref = N_element
FEATURE [App::DocumentObjectGroupPython] O_element116  label="O_element : 069"  # scripted group (container) (typed FeaturePython)
  n = 1
  ref = O_element
FEATURE [App::DocumentObjectGroupPython] G4_DNA_GUANINE  # scripted group (container) (typed FeaturePython)
  Dunit = g/cm3
  Dvalue = 1
  Group = -> [H_element125,C_element135,N_element055,O_element116]
  conduct = 2
  density = 1
  expand = 3
  formula = G4_DNA_GUANINE
  name = G4_DNA_GUANINE
  specific = 4
FEATURE [App::DocumentObjectGroupPython] H_element126  label="H_element : 073"  # scripted group (container) (typed FeaturePython)
  n = 4
  ref = H_element
FEATURE [App::DocumentObjectGroupPython] C_element136  label="C_element : 081"  # scripted group (container) (typed FeaturePython)
  n = 4
  ref = C_element
FEATURE [App::DocumentObjectGroupPython] N_element056  label="N_element : 028"  # scripted group (container) (typed FeaturePython)
  n = 3
  ref = N_element
FEATURE [App::DocumentObjectGroupPython] O_element117  label="O_element : 070"  # scripted group (container) (typed FeaturePython)
  n = 1
  ref = O_element
FEATURE [App::DocumentObjectGroupPython] G4_DNA_CYTOSINE  # scripted group (container) (typed FeaturePython)
  Dunit = g/cm3
  Dvalue = 1
  Group = -> [H_element126,C_element136,N_element056,O_element117]
  conduct = 2
  density = 1
  expand = 3
  formula = G4_DNA_CYTOSINE
  name = G4_DNA_CYTOSINE
  specific = 4
FEATURE [App::DocumentObjectGroupPython] H_element127  label="H_element : 074"  # scripted group (container) (typed FeaturePython)
  n = 5
  ref = H_element
FEATURE [App::DocumentObjectGroupPython] C_element137  label="C_element : 082"  # scripted group (container) (typed FeaturePython)
  n = 5
  ref = C_element
FEATURE [App::DocumentObjectGroupPython] N_element057  label="N_element : 029"  # scripted group (container) (typed FeaturePython)
  n = 2
  ref = N_element
FEATURE [App::DocumentObjectGroupPython] O_element118  label="O_element : 071"  # scripted group (container) (typed FeaturePython)
  n = 2
  ref = O_element
FEATURE [App::DocumentObjectGroupPython] G4_DNA_THYMINE  # scripted group (container) (typed FeaturePython)
  Dunit = g/cm3
  Dvalue = 1
  Group = -> [H_element127,C_element137,N_element057,O_element118]
  conduct = 2
  density = 1
  expand = 3
  formula = G4_DNA_THYMINE
  name = G4_DNA_THYMINE
  specific = 4
FEATURE [App::DocumentObjectGroupPython] H_element128  label="H_element : 075"  # scripted group (container) (typed FeaturePython)
  n = 3
  ref = H_element
FEATURE [App::DocumentObjectGroupPython] C_element138  label="C_element : 083"  # scripted group (container) (typed FeaturePython)
  n = 4
  ref = C_element
FEATURE [App::DocumentObjectGroupPython] N_element058  label="N_element : 030"  # scripted group (container) (typed FeaturePython)
  n = 2
  ref = N_element
FEATURE [App::DocumentObjectGroupPython] O_element119  label="O_element : 072"  # scripted group (container) (typed FeaturePython)
  n = 2
  ref = O_element
FEATURE [App::DocumentObjectGroupPython] G4_DNA_URACIL  # scripted group (container) (typed FeaturePython)
  Dunit = g/cm3
  Dvalue = 1
  Group = -> [H_element128,C_element138,N_element058,O_element119]
  conduct = 2
  density = 1
  expand = 3
  formula = G4_DNA_URACIL
  name = G4_DNA_URACIL
  specific = 4
FEATURE [App::DocumentObjectGroupPython] H_element129  label="H_element : 076"  # scripted group (container) (typed FeaturePython)
  n = 10
  ref = H_element
FEATURE [App::DocumentObjectGroupPython] C_element139  label="C_element : 084"  # scripted group (container) (typed FeaturePython)
  n = 10
  ref = C_element
FEATURE [App::DocumentObjectGroupPython] N_element059  label="N_element : 031"  # scripted group (container) (typed FeaturePython)
  n = 5
  ref = N_element
FEATURE [App::DocumentObjectGroupPython] O_element120  label="O_element : 073"  # scripted group (container) (typed FeaturePython)
  n = 4
  ref = O_element
FEATURE [App::DocumentObjectGroupPython] G4_DNA_ADENOSINE  # scripted group (container) (typed FeaturePython)
  Dunit = g/cm3
  Dvalue = 1
  Group = -> [H_element129,C_element139,N_element059,O_element120]
  conduct = 2
  density = 1
  expand = 3
  formula = G4_DNA_ADENOSINE
  name = G4_DNA_ADENOSINE
  specific = 4
FEATURE [App::DocumentObjectGroupPython] H_element130  label="H_element : 077"  # scripted group (container) (typed FeaturePython)
  n = 10
  ref = H_element
FEATURE [App::DocumentObjectGroupPython] C_element140  label="C_element : 085"  # scripted group (container) (typed FeaturePython)
  n = 10
  ref = C_element
FEATURE [App::DocumentObjectGroupPython] N_element060  label="N_element : 032"  # scripted group (container) (typed FeaturePython)
  n = 5
  ref = N_element
FEATURE [App::DocumentObjectGroupPython] O_element121  label="O_element : 074"  # scripted group (container) (typed FeaturePython)
  n = 5
  ref = O_element
FEATURE [App::DocumentObjectGroupPython] G4_DNA_GUANOSINE  # scripted group (container) (typed FeaturePython)
  Dunit = g/cm3
  Dvalue = 1
  Group = -> [H_element130,C_element140,N_element060,O_element121]
  conduct = 2
  density = 1
  expand = 3
  formula = G4_DNA_GUANOSINE
  name = G4_DNA_GUANOSINE
  specific = 4
FEATURE [App::DocumentObjectGroupPython] H_element131  label="H_element : 078"  # scripted group (container) (typed FeaturePython)
  n = 10
  ref = H_element
FEATURE [App::DocumentObjectGroupPython] C_element141  label="C_element : 086"  # scripted group (container) (typed FeaturePython)
  n = 9
  ref = C_element
FEATURE [App::DocumentObjectGroupPython] N_element061  label="N_element : 033"  # scripted group (container) (typed FeaturePython)
  n = 3
  ref = N_element
FEATURE [App::DocumentObjectGroupPython] O_element122  label="O_element : 075"  # scripted group (container) (typed FeaturePython)
  n = 5
  ref = O_element
FEATURE [App::DocumentObjectGroupPython] G4_DNA_CYTIDINE  # scripted group (container) (typed FeaturePython)
  Dunit = g/cm3
  Dvalue = 1
  Group = -> [H_element131,C_element141,N_element061,O_element122]
  conduct = 2
  density = 1
  expand = 3
  formula = G4_DNA_CYTIDINE
  name = G4_DNA_CYTIDINE
  specific = 4
FEATURE [App::DocumentObjectGroupPython] H_element132  label="H_element : 079"  # scripted group (container) (typed FeaturePython)
  n = 9
  ref = H_element
FEATURE [App::DocumentObjectGroupPython] C_element142  label="C_element : 087"  # scripted group (container) (typed FeaturePython)
  n = 9
  ref = C_element
FEATURE [App::DocumentObjectGroupPython] N_element062  label="N_element : 034"  # scripted group (container) (typed FeaturePython)
  n = 2
  ref = N_element
FEATURE [App::DocumentObjectGroupPython] O_element123  label="O_element : 076"  # scripted group (container) (typed FeaturePython)
  n = 6
  ref = O_element
FEATURE [App::DocumentObjectGroupPython] G4_DNA_URIDINE  # scripted group (container) (typed FeaturePython)
  Dunit = g/cm3
  Dvalue = 1
  Group = -> [H_element132,C_element142,N_element062,O_element123]
  conduct = 2
  density = 1
  expand = 3
  formula = G4_DNA_URIDINE
  name = G4_DNA_URIDINE
  specific = 4
FEATURE [App::DocumentObjectGroupPython] H_element133  label="H_element : 080"  # scripted group (container) (typed FeaturePython)
  n = 11
  ref = H_element
FEATURE [App::DocumentObjectGroupPython] C_element143  label="C_element : 088"  # scripted group (container) (typed FeaturePython)
  n = 10
  ref = C_element
FEATURE [App::DocumentObjectGroupPython] N_element063  label="N_element : 035"  # scripted group (container) (typed FeaturePython)
  n = 2
  ref = N_element
FEATURE [App::DocumentObjectGroupPython] O_element124  label="O_element : 077"  # scripted group (container) (typed FeaturePython)
  n = 6
  ref = O_element
FEATURE [App::DocumentObjectGroupPython] G4_DNA_METHYLURIDINE  # scripted group (container) (typed FeaturePython)
  Dunit = g/cm3
  Dvalue = 1
  Group = -> [H_element133,C_element143,N_element063,O_element124]
  conduct = 2
  density = 1
  expand = 3
  formula = G4_DNA_METHYLURIDINE
  name = G4_DNA_METHYLURIDINE
  specific = 4
FEATURE [App::DocumentObjectGroupPython] P_element014  label="P_element : 003"  # scripted group (container) (typed FeaturePython)
  n = 1
  ref = P_element
FEATURE [App::DocumentObjectGroupPython] O_element125  label="O_element : 078"  # scripted group (container) (typed FeaturePython)
  n = 3
  ref = O_element
FEATURE [App::DocumentObjectGroupPython] G4_DNA_MONOPHOSPHATE  # scripted group (container) (typed FeaturePython)
  Dunit = g/cm3
  Dvalue = 1
  Group = -> [P_element014,O_element125]
  conduct = 2
  density = 1
  expand = 3
  formula = G4_DNA_MONOPHOSPHATE
  name = G4_DNA_MONOPHOSPHATE
  specific = 4
FEATURE [App::DocumentObjectGroupPython] H_element134  label="H_element : 081"  # scripted group (container) (typed FeaturePython)
  n = 10
  ref = H_element
FEATURE [App::DocumentObjectGroupPython] C_element144  label="C_element : 089"  # scripted group (container) (typed FeaturePython)
  n = 10
  ref = C_element
FEATURE [App::DocumentObjectGroupPython] N_element064  label="N_element : 036"  # scripted group (container) (typed FeaturePython)
  n = 5
  ref = N_element
FEATURE [App::DocumentObjectGroupPython] O_element126  label="O_element : 079"  # scripted group (container) (typed FeaturePython)
  n = 7
  ref = O_element
FEATURE [App::DocumentObjectGroupPython] P_element015  label="P_element : 004"  # scripted group (container) (typed FeaturePython)
  n = 1
  ref = P_element
FEATURE [App::DocumentObjectGroupPython] G4_DNA_A  # scripted group (container) (typed FeaturePython)
  Dunit = g/cm3
  Dvalue = 1
  Group = -> [H_element134,C_element144,N_element064,O_element126,P_element015]
  conduct = 2
  density = 1
  expand = 3
  formula = G4_DNA_A
  name = G4_DNA_A
  specific = 4
FEATURE [App::DocumentObjectGroupPython] H_element135  label="H_element : 082"  # scripted group (container) (typed FeaturePython)
  n = 10
  ref = H_element
FEATURE [App::DocumentObjectGroupPython] C_element145  label="C_element : 090"  # scripted group (container) (typed FeaturePython)
  n = 10
  ref = C_element
FEATURE [App::DocumentObjectGroupPython] N_element065  label="N_element : 037"  # scripted group (container) (typed FeaturePython)
  n = 5
  ref = N_element
FEATURE [App::DocumentObjectGroupPython] O_element127  label="O_element : 8"  # scripted group (container) (typed FeaturePython)
  n = 8
  ref = O_element
FEATURE [App::DocumentObjectGroupPython] P_element016  label="P_element : 005"  # scripted group (container) (typed FeaturePython)
  n = 1
  ref = P_element
FEATURE [App::DocumentObjectGroupPython] G4_DNA_G  # scripted group (container) (typed FeaturePython)
  Dunit = g/cm3
  Dvalue = 1
  Group = -> [H_element135,C_element145,N_element065,O_element127,P_element016]
  conduct = 2
  density = 1
  expand = 3
  formula = G4_DNA_G
  name = G4_DNA_G
  specific = 4
FEATURE [App::DocumentObjectGroupPython] H_element136  label="H_element : 083"  # scripted group (container) (typed FeaturePython)
  n = 10
  ref = H_element
FEATURE [App::DocumentObjectGroupPython] C_element146  label="C_element : 091"  # scripted group (container) (typed FeaturePython)
  n = 9
  ref = C_element
FEATURE [App::DocumentObjectGroupPython] N_element066  label="N_element : 038"  # scripted group (container) (typed FeaturePython)
  n = 3
  ref = N_element
FEATURE [App::DocumentObjectGroupPython] O_element128  label="O_element : 080"  # scripted group (container) (typed FeaturePython)
  n = 8
  ref = O_element
FEATURE [App::DocumentObjectGroupPython] P_element017  label="P_element : 006"  # scripted group (container) (typed FeaturePython)
  n = 1
  ref = P_element
FEATURE [App::DocumentObjectGroupPython] G4_DNA_C  # scripted group (container) (typed FeaturePython)
  Dunit = g/cm3
  Dvalue = 1
  Group = -> [H_element136,C_element146,N_element066,O_element128,P_element017]
  conduct = 2
  density = 1
  expand = 3
  formula = G4_DNA_C
  name = G4_DNA_C
  specific = 4
FEATURE [App::DocumentObjectGroupPython] H_element137  label="H_element : 084"  # scripted group (container) (typed FeaturePython)
  n = 9
  ref = H_element
FEATURE [App::DocumentObjectGroupPython] C_element147  label="C_element : 092"  # scripted group (container) (typed FeaturePython)
  n = 9
  ref = C_element
FEATURE [App::DocumentObjectGroupPython] N_element067  label="N_element : 039"  # scripted group (container) (typed FeaturePython)
  n = 2
  ref = N_element
FEATURE [App::DocumentObjectGroupPython] O_element129  label="O_element : 9"  # scripted group (container) (typed FeaturePython)
  n = 9
  ref = O_element
FEATURE [App::DocumentObjectGroupPython] P_element018  label="P_element : 007"  # scripted group (container) (typed FeaturePython)
  n = 1
  ref = P_element
FEATURE [App::DocumentObjectGroupPython] G4_DNA_U  # scripted group (container) (typed FeaturePython)
  Dunit = g/cm3
  Dvalue = 1
  Group = -> [H_element137,C_element147,N_element067,O_element129,P_element018]
  conduct = 2
  density = 1
  expand = 3
  formula = G4_DNA_U
  name = G4_DNA_U
  specific = 4
FEATURE [App::DocumentObjectGroupPython] H_element138  label="H_element : 085"  # scripted group (container) (typed FeaturePython)
  n = 11
  ref = H_element
FEATURE [App::DocumentObjectGroupPython] C_element148  label="C_element : 093"  # scripted group (container) (typed FeaturePython)
  n = 10
  ref = C_element
FEATURE [App::DocumentObjectGroupPython] N_element068  label="N_element : 040"  # scripted group (container) (typed FeaturePython)
  n = 2
  ref = N_element
FEATURE [App::DocumentObjectGroupPython] O_element130  label="O_element : 081"  # scripted group (container) (typed FeaturePython)
  n = 9
  ref = O_element
FEATURE [App::DocumentObjectGroupPython] P_element019  label="P_element : 008"  # scripted group (container) (typed FeaturePython)
  n = 1
  ref = P_element
FEATURE [App::DocumentObjectGroupPython] G4_DNA_MU  # scripted group (container) (typed FeaturePython)
  Dunit = g/cm3
  Dvalue = 1
  Group = -> [H_element138,C_element148,N_element068,O_element130,P_element019]
  conduct = 2
  density = 1
  expand = 3
  formula = G4_DNA_MU
  name = G4_DNA_MU
  specific = 4
FEATURE [App::DocumentObjectGroupPython] BioChemical  # scripted group (container) (typed FeaturePython)
  Group = -> [G4_CYTOSINE,G4_THYMINE,G4_URACIL,G4_DNA_ADENINE,G4_DNA_GUANINE,G4_DNA_CYTOSINE,G4_DNA_THYMINE,G4_DNA_URACIL,G4_DNA_ADENOSINE,G4_DNA_GUANOSINE,G4_DNA_CYTIDINE,G4_DNA_URIDINE,G4_DNA_METHYLURIDINE,G4_DNA_MONOPHOSPHATE,G4_DNA_A,G4_DNA_G,G4_DNA_C,G4_DNA_U,G4_DNA_MU]
FEATURE [App::DocumentObjectGroupPython] G4Materials  # scripted group (container) (typed FeaturePython)
  Group = -> [NIST,Element,HEP,Space,BioChemical]
  version = 1
FEATURE [App::DocumentObjectGroupPython] Geant4  # scripted group (container) (typed FeaturePython)
  Group = -> [G4Isotopes,G4Elements,G4Materials]
FEATURE [App::DocumentObjectGroupPython] Materials  # scripted group (container) (typed FeaturePython)
  Group = -> [Geant4]
FEATURE [Part::FeaturePython] GDMLBox_WorldBox  # WARN: FeaturePython — macro-defined, semantics opaque (R4)
  lunit = 2
  material = 5
  x = 273
  y = 273
  z = 130
FEATURE [Part::FeaturePython] GDMLBox_Box  # WARN: FeaturePython — macro-defined, semantics opaque (R4)
  Placement = pos=(20,0,0) rot=(0,0,1;0rad)
  lunit = 2
  material = 0
  x = 10
  y = 10
  z = 10
FEATURE [Part::FeaturePython] GDMLTube  # WARN: FeaturePython — macro-defined, semantics opaque (R4)
  Placement = pos=(17,-4,0) rot=(0,0,1;0rad)
  aunit = 1
  deltaphi = 90
  lunit = 2
  material = 0
  rmax = 7
  rmin = 5
  startphi = 0
  z = 7
FEATURE [App::Part] LV_Tube
  Group = -> [GDMLTube]
  Origin = -> Origin003
  SkinSurface = 0
FEATURE [App::Part] LV_Box
  Group = -> [GDMLBox_Box,LV_Tube]
  Origin = -> Origin002
FEATURE [Part::FeaturePython] Array  # Draft array (typed FeaturePython)
  AlwaysSyncPlacement = false
  Angle = 180
  ArrayType = 1
  Axis = (0,0,1)
  Base = -> LV_Box
  Center = (0,0,0)
  Count = 5
  ExpandArray = false
  Fuse = false
  IntervalAxis = (0,0,0)
  IntervalX = (100,0,0)
  IntervalY = (0,100,0)
  IntervalZ = (0,0,100)
  NumberCircles = 3
  NumberPolar = 5
  NumberX = 2
  NumberY = 2
  NumberZ = 1
  PlacementList = 5 placements: [(0,0,0),(0,0,0),(0,0,0),(0,0,0),(0,0,0)]
  RadialDistance = 50
  ScaleList = (5) [(1,1,1),(1,1,1),(1,1,1),(1,1,1),(1,1,1)]
  Symmetry = 1
  TangentialDistance = 25
FEATURE [App::Part] Part  label="experiment"
  Group = -> [LV_Box,Array]
  Origin = -> Origin001
FEATURE [App::Part] worldVOL
  Group = -> [GDMLBox_WorldBox,Part]
  Origin = -> Origin
